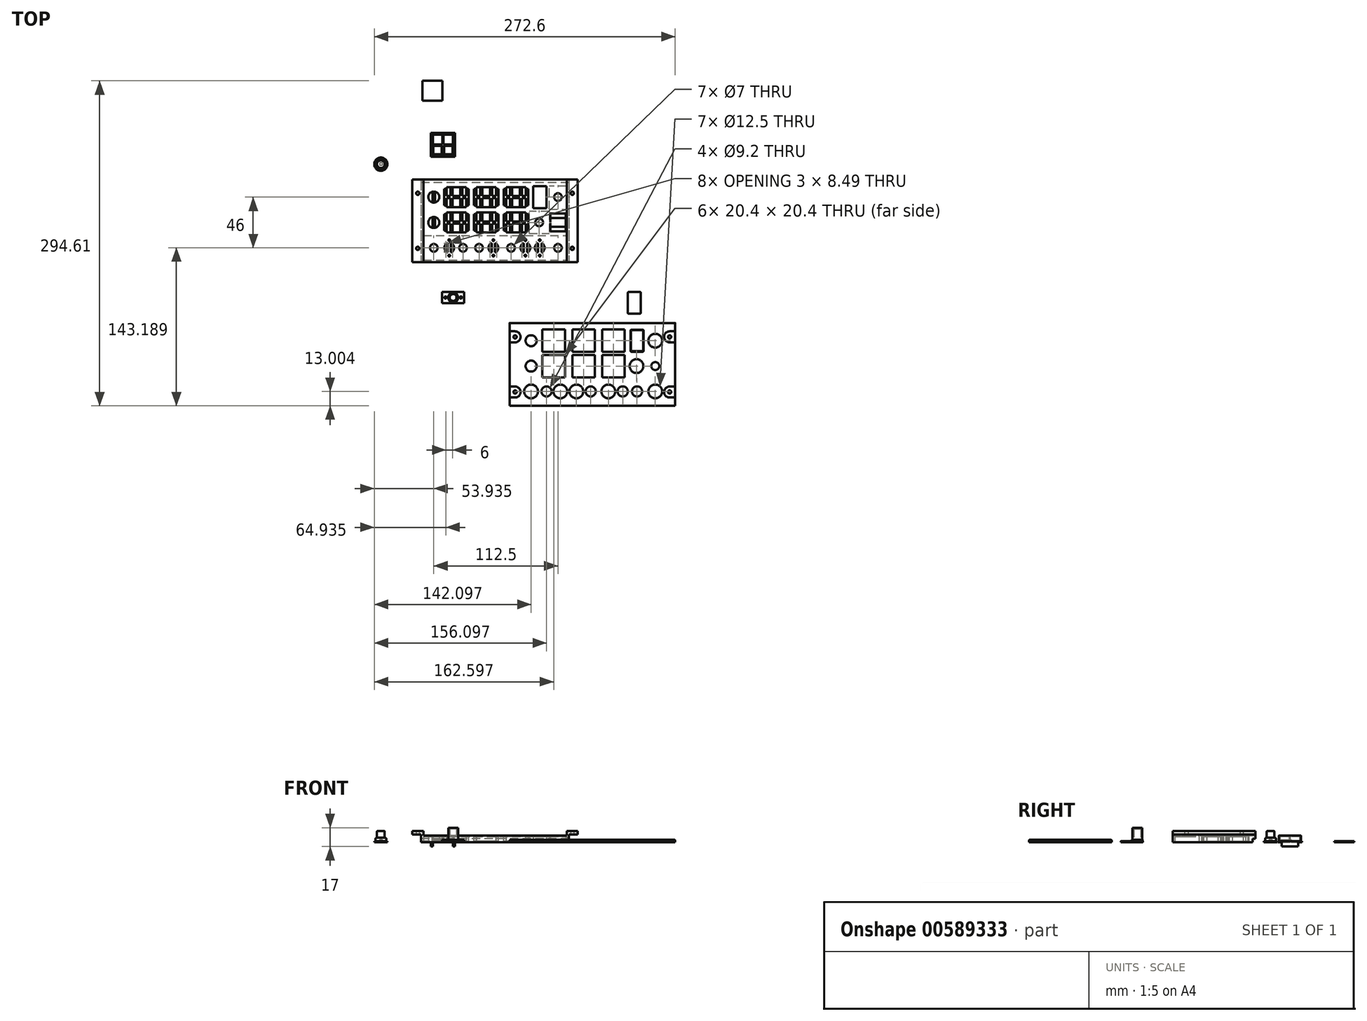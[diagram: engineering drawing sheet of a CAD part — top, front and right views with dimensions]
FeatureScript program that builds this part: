
annotation { "Feature Type Name" : "Feature", "Feature Type Description" : "" }
export const myFeature = defineFeature(function(context is Context, id is Id, definition is map)
    precondition{}
    {
        {
            var Q0;
            Q0=qCreatedBy(makeId("Top.planeOp"),FACE);
            var sketch = newSketch(context, id + "F0", { "sketchPlane" : qUnion([Q0])});
            skLineSegment(sketch, "E0.bottom", {"start": v(0.5, -57.04) * mm, "end": v(-149.5, -57.04) * mm});
            skLineSegment(sketch, "E0.top", {"start": v(0.5, 17.96) * mm, "end": v(-149.5, 17.96) * mm});
            skLineSegment(sketch, "E0.left", {"start": v(0.5, -57.04) * mm, "end": v(0.5, 17.96) * mm});
            skLineSegment(sketch, "E0.right", {"start": v(-149.5, -57.04) * mm, "end": v(-149.5, 17.96) * mm});
            skLineSegment(sketch, "E1.bottom", {"start": v(-99.5, -8.04) * mm, "end": v(-119.5, -8.04) * mm, "construction": true});
            skLineSegment(sketch, "E1.top", {"start": v(-99.5, 11.96) * mm, "end": v(-119.5, 11.96) * mm, "construction": true});
            skLineSegment(sketch, "E1.left", {"start": v(-99.5, -8.04) * mm, "end": v(-99.5, 11.96) * mm, "construction": true});
            skLineSegment(sketch, "E1.right", {"start": v(-119.5, -8.04) * mm, "end": v(-119.5, 11.96) * mm, "construction": true});
            skPoint(sketch, "E1.middle", {"position": v(-109.5, 1.96) * mm});
            skLineSegment(sketch, "E2.bottom", {"start": v(-99.5, -31.04) * mm, "end": v(-119.5, -31.04) * mm, "construction": true});
            skLineSegment(sketch, "E2.top", {"start": v(-99.5, -11.04) * mm, "end": v(-119.5, -11.04) * mm, "construction": true});
            skLineSegment(sketch, "E2.left", {"start": v(-99.5, -31.04) * mm, "end": v(-99.5, -11.04) * mm, "construction": true});
            skLineSegment(sketch, "E2.right", {"start": v(-119.5, -31.04) * mm, "end": v(-119.5, -11.04) * mm, "construction": true});
            skPoint(sketch, "E2.middle", {"position": v(-109.5, -21.04) * mm});
            skCircle(sketch, "E3", {"center": v(-103.5, -44.04) * mm, "radius": 3.5 * mm});
            skCircle(sketch, "E4", {"center": v(-89, -44.04) * mm, "radius": 3.5 * mm});
            skLineSegment(sketch, "E5.bottom", {"start": v(-149.5, 17.96) * mm, "end": v(-141.5, 17.96) * mm, "construction": true});
            skLineSegment(sketch, "E5.top", {"start": v(-149.5, -57.04) * mm, "end": v(-141.5, -57.04) * mm, "construction": true});
            skLineSegment(sketch, "E5.left", {"start": v(-149.5, 17.96) * mm, "end": v(-149.5, -57.04) * mm, "construction": true});
            skLineSegment(sketch, "E5.right", {"start": v(-141.5, 17.96) * mm, "end": v(-141.5, -57.04) * mm, "construction": true});
            skLineSegment(sketch, "E6.bottom", {"start": v(0.5, -57.04) * mm, "end": v(-7.5, -57.04) * mm, "construction": true});
            skLineSegment(sketch, "E6.top", {"start": v(0.5, 17.96) * mm, "end": v(-7.5, 17.96) * mm, "construction": true});
            skLineSegment(sketch, "E6.left", {"start": v(0.5, -57.04) * mm, "end": v(0.5, 17.96) * mm, "construction": true});
            skLineSegment(sketch, "E6.right", {"start": v(-7.5, -57.04) * mm, "end": v(-7.5, 17.96) * mm, "construction": true});
            skCircle(sketch, "E7", {"center": v(-116, -44.04) * mm, "radius": 4.5 * mm});
            skCircle(sketch, "E8", {"center": v(-76, -44.04) * mm, "radius": 4.5 * mm});
            skCircle(sketch, "E9", {"center": v(-60, -44.04) * mm, "radius": 3.5 * mm});
            skCircle(sketch, "E10", {"center": v(-47, -44.04) * mm, "radius": 4.5 * mm});
            skCircle(sketch, "E11", {"center": v(-34, -44.04) * mm, "radius": 4.5 * mm});
            skCircle(sketch, "E12", {"center": v(-17.5, -44.04) * mm, "radius": 3.5 * mm});
            skCircle(sketch, "E13", {"center": v(-34.5, -21.04) * mm, "radius": 3.5 * mm});
            skLineSegment(sketch, "E14.bottom", {"start": v(-28, -8.04) * mm, "end": v(-40, -8.04) * mm});
            skLineSegment(sketch, "E14.top", {"start": v(-28, 11.96) * mm, "end": v(-40, 11.96) * mm});
            skLineSegment(sketch, "E14.left", {"start": v(-28, -8.04) * mm, "end": v(-28, 11.96) * mm});
            skLineSegment(sketch, "E14.right", {"start": v(-40, -8.04) * mm, "end": v(-40, 11.96) * mm});
            skPoint(sketch, "E14.middle", {"position": v(-34, 1.96) * mm});
            skCircle(sketch, "E15", {"center": v(-17.5, 1.96) * mm, "radius": 3.5 * mm});
            skCircle(sketch, "E16", {"center": v(-17.5, -21.04) * mm, "radius": 5 * mm, "construction": true});
            skPoint(sketch, "E17.centerSnap0", {"position": v(-119.5, -21.04) * mm});
            skLineSegment(sketch, "E18.bottom", {"start": v(-100.5, -7.04) * mm, "end": v(-118.5, -7.04) * mm});
            skLineSegment(sketch, "E18.top", {"start": v(-100.5, 10.96) * mm, "end": v(-118.5, 10.96) * mm});
            skLineSegment(sketch, "E18.left", {"start": v(-100.5, -7.04) * mm, "end": v(-100.5, 10.96) * mm});
            skLineSegment(sketch, "E18.right", {"start": v(-118.5, -7.04) * mm, "end": v(-118.5, 10.96) * mm});
            skLineSegment(sketch, "E19.bottom", {"start": v(-100.5, -30.04) * mm, "end": v(-118.5, -30.04) * mm});
            skLineSegment(sketch, "E19.top", {"start": v(-100.5, -12.04) * mm, "end": v(-118.5, -12.04) * mm});
            skLineSegment(sketch, "E19.left", {"start": v(-100.5, -30.04) * mm, "end": v(-100.5, -12.04) * mm});
            skLineSegment(sketch, "E19.right", {"start": v(-118.5, -30.04) * mm, "end": v(-118.5, -12.04) * mm});
            skLineSegment(sketch, "E20.bottom", {"start": v(-100.5, 0.96) * mm, "end": v(-104, 0.96) * mm});
            skLineSegment(sketch, "E20.top", {"start": v(-100.5, 2.96) * mm, "end": v(-104, 2.96) * mm});
            skLineSegment(sketch, "E20.left", {"start": v(-100.5, 0.96) * mm, "end": v(-100.5, 2.96) * mm});
            skLineSegment(sketch, "E20.right", {"start": v(-118.5, 0.96) * mm, "end": v(-118.5, 2.96) * mm});
            skLineSegment(sketch, "E21.bottom", {"start": v(-113, -7.04) * mm, "end": v(-115, -7.04) * mm});
            skLineSegment(sketch, "E21.top", {"start": v(-113, 10.96) * mm, "end": v(-115, 10.96) * mm});
            skLineSegment(sketch, "E21.left", {"start": v(-113, -7.04) * mm, "end": v(-113, 0.96) * mm});
            skLineSegment(sketch, "E21.right", {"start": v(-115, -7.04) * mm, "end": v(-115, 0.96) * mm});
            skPoint(sketch, "E21.middle", {"position": v(-114, 1.96) * mm});
            skLineSegment(sketch, "E22.bottom", {"start": v(-104, -7.04) * mm, "end": v(-106, -7.04) * mm});
            skLineSegment(sketch, "E22.top", {"start": v(-104, 10.96) * mm, "end": v(-106, 10.96) * mm});
            skLineSegment(sketch, "E22.left", {"start": v(-104, -7.04) * mm, "end": v(-104, 0.96) * mm});
            skLineSegment(sketch, "E22.right", {"start": v(-106, -7.04) * mm, "end": v(-106, 0.96) * mm});
            skPoint(sketch, "E22.middle", {"position": v(-105, 1.96) * mm});
            skLineSegment(sketch, "E23.trimOffspring", {"start": v(-115, 2.96) * mm, "end": v(-115, 10.96) * mm});
            skLineSegment(sketch, "E24.trimOffspring", {"start": v(-115, 2.96) * mm, "end": v(-118.5, 2.96) * mm});
            skLineSegment(sketch, "E25.trimOffspring", {"start": v(-113, 2.96) * mm, "end": v(-113, 10.96) * mm});
            skLineSegment(sketch, "E26.trimOffspring", {"start": v(-115, 0.96) * mm, "end": v(-118.5, 0.96) * mm});
            skLineSegment(sketch, "E27.trimOffspring", {"start": v(-106, 2.96) * mm, "end": v(-106, 10.96) * mm});
            skLineSegment(sketch, "E28.trimOffspring", {"start": v(-106, 2.96) * mm, "end": v(-113, 2.96) * mm});
            skLineSegment(sketch, "E29.trimOffspring", {"start": v(-104, 2.96) * mm, "end": v(-104, 10.96) * mm});
            skLineSegment(sketch, "E30.trimOffspring", {"start": v(-106, 0.96) * mm, "end": v(-113, 0.96) * mm});
            skLineSegment(sketch, "E31.bottom", {"start": v(-100.5, -22.04) * mm, "end": v(-104, -22.04) * mm});
            skLineSegment(sketch, "E31.top", {"start": v(-100.5, -20.04) * mm, "end": v(-104, -20.04) * mm});
            skLineSegment(sketch, "E31.left", {"start": v(-100.5, -22.04) * mm, "end": v(-100.5, -20.04) * mm});
            skLineSegment(sketch, "E31.right", {"start": v(-118.5, -22.04) * mm, "end": v(-118.5, -20.04) * mm});
            skLineSegment(sketch, "E32.bottom", {"start": v(-113, -30.04) * mm, "end": v(-115, -30.04) * mm});
            skLineSegment(sketch, "E32.top", {"start": v(-113, -12.04) * mm, "end": v(-115, -12.04) * mm});
            skLineSegment(sketch, "E32.left", {"start": v(-113, -30.04) * mm, "end": v(-113, -22.04) * mm});
            skLineSegment(sketch, "E32.right", {"start": v(-115, -30.04) * mm, "end": v(-115, -22.04) * mm});
            skPoint(sketch, "E32.middle", {"position": v(-114, -21.04) * mm});
            skLineSegment(sketch, "E33.bottom", {"start": v(-104, -30.04) * mm, "end": v(-106, -30.04) * mm});
            skLineSegment(sketch, "E33.top", {"start": v(-104, -12.04) * mm, "end": v(-106, -12.04) * mm});
            skLineSegment(sketch, "E33.left", {"start": v(-104, -30.04) * mm, "end": v(-104, -22.04) * mm});
            skLineSegment(sketch, "E33.right", {"start": v(-106, -30.04) * mm, "end": v(-106, -22.04) * mm});
            skPoint(sketch, "E33.middle", {"position": v(-105, -21.04) * mm});
            skLineSegment(sketch, "E34.trimOffspring", {"start": v(-115, -20.04) * mm, "end": v(-115, -12.04) * mm});
            skLineSegment(sketch, "E35.trimOffspring", {"start": v(-115, -20.04) * mm, "end": v(-118.5, -20.04) * mm});
            skLineSegment(sketch, "E36.trimOffspring", {"start": v(-113, -20.04) * mm, "end": v(-113, -12.04) * mm});
            skLineSegment(sketch, "E37.trimOffspring", {"start": v(-115, -22.04) * mm, "end": v(-118.5, -22.04) * mm});
            skLineSegment(sketch, "E38.trimOffspring", {"start": v(-106, -20.04) * mm, "end": v(-106, -12.04) * mm});
            skLineSegment(sketch, "E39.trimOffspring", {"start": v(-106, -20.04) * mm, "end": v(-113, -20.04) * mm});
            skLineSegment(sketch, "E40.trimOffspring", {"start": v(-104, -20.04) * mm, "end": v(-104, -12.04) * mm});
            skLineSegment(sketch, "E41.trimOffspring", {"start": v(-106, -22.04) * mm, "end": v(-113, -22.04) * mm});
            skPoint(sketch, "E42.middle", {"position": v(-130, 1.96) * mm});
            skPoint(sketch, "E43.middle", {"position": v(-130, -21.04) * mm});
            skLineSegment(sketch, "E44.left", {"start": v(-129, -2.94) * mm, "end": v(-129, 6.86) * mm});
            skLineSegment(sketch, "E44.right", {"start": v(-131, -2.94) * mm, "end": v(-131, 6.86) * mm});
            skLineSegment(sketch, "E45.left", {"start": v(-129, -25.94) * mm, "end": v(-129, -16.14) * mm});
            skLineSegment(sketch, "E45.right", {"start": v(-131, -25.94) * mm, "end": v(-131, -16.14) * mm});
            skCircle(sketch, "E46", {"center": v(-144.5, 5.46) * mm, "radius": 1.5 * mm});
            skPoint(sketch, "E46.centerSnap0", {"position": v(-145.5, 17.96) * mm});
            skCircle(sketch, "E47", {"center": v(-144.5, -44.54) * mm, "radius": 1.5 * mm});
            skCircle(sketch, "E48", {"center": v(-4.5, 5.46) * mm, "radius": 1.5 * mm});
            skCircle(sketch, "E49", {"center": v(-4.5, -44.54) * mm, "radius": 1.5 * mm});
            skLineSegment(sketch, "E50.1.0.0", {"start": v(-73.5, 2.96) * mm, "end": v(-77, 2.96) * mm});
            skLineSegment(sketch, "E50.1.0.1", {"start": v(-79, -30.04) * mm, "end": v(-79, -22.04) * mm});
            skLineSegment(sketch, "E50.1.0.2", {"start": v(-79, -22.04) * mm, "end": v(-86, -22.04) * mm});
            skLineSegment(sketch, "E50.1.0.3", {"start": v(-88, -30.04) * mm, "end": v(-88, -22.04) * mm});
            skLineSegment(sketch, "E50.1.0.4", {"start": v(-72.5, -8.04) * mm, "end": v(-72.5, 11.96) * mm, "construction": true});
            skLineSegment(sketch, "E50.1.0.5", {"start": v(-72.5, -8.04) * mm, "end": v(-92.5, -8.04) * mm, "construction": true});
            skLineSegment(sketch, "E50.1.0.6", {"start": v(-72.5, -31.04) * mm, "end": v(-92.5, -31.04) * mm, "construction": true});
            skLineSegment(sketch, "E50.1.0.7", {"start": v(-73.5, -30.04) * mm, "end": v(-73.5, -12.04) * mm});
            skLineSegment(sketch, "E50.1.0.8", {"start": v(-73.5, -7.04) * mm, "end": v(-91.5, -7.04) * mm});
            skLineSegment(sketch, "E50.1.0.9", {"start": v(-79, 2.96) * mm, "end": v(-86, 2.96) * mm});
            skLineSegment(sketch, "E50.1.0.10", {"start": v(-79, -20.04) * mm, "end": v(-86, -20.04) * mm});
            skLineSegment(sketch, "E50.1.0.11", {"start": v(-88, 2.96) * mm, "end": v(-91.5, 2.96) * mm});
            skLineSegment(sketch, "E50.1.0.12", {"start": v(-77, -30.04) * mm, "end": v(-77, -22.04) * mm});
            skLineSegment(sketch, "E50.1.0.13", {"start": v(-86, 2.96) * mm, "end": v(-86, 10.96) * mm});
            skLineSegment(sketch, "E50.1.0.14", {"start": v(-77, -20.04) * mm, "end": v(-77, -12.04) * mm});
            skLineSegment(sketch, "E50.1.0.15", {"start": v(-88, -20.04) * mm, "end": v(-88, -12.04) * mm});
            skLineSegment(sketch, "E50.1.0.16", {"start": v(-79, 2.96) * mm, "end": v(-79, 10.96) * mm});
            skPoint(sketch, "E50.1.0.17", {"position": v(-82.5, -21.04) * mm});
            skLineSegment(sketch, "E50.1.0.18", {"start": v(-73.5, -22.04) * mm, "end": v(-77, -22.04) * mm});
            skLineSegment(sketch, "E50.1.0.19", {"start": v(-88, 0.96) * mm, "end": v(-91.5, 0.96) * mm});
            skLineSegment(sketch, "E50.1.0.20", {"start": v(-72.5, 11.96) * mm, "end": v(-92.5, 11.96) * mm, "construction": true});
            skLineSegment(sketch, "E50.1.0.21", {"start": v(-88, -22.04) * mm, "end": v(-91.5, -22.04) * mm});
            skLineSegment(sketch, "E50.1.0.22", {"start": v(-91.5, -7.04) * mm, "end": v(-91.5, 10.96) * mm});
            skLineSegment(sketch, "E50.1.0.23", {"start": v(-72.5, -11.04) * mm, "end": v(-92.5, -11.04) * mm, "construction": true});
            skLineSegment(sketch, "E50.1.0.24", {"start": v(-92.5, -31.04) * mm, "end": v(-92.5, -11.04) * mm, "construction": true});
            skLineSegment(sketch, "E50.1.0.25", {"start": v(-79, -20.04) * mm, "end": v(-79, -12.04) * mm});
            skLineSegment(sketch, "E50.1.0.26", {"start": v(-92.5, -8.04) * mm, "end": v(-92.5, 11.96) * mm, "construction": true});
            skLineSegment(sketch, "E50.1.0.27", {"start": v(-88, 2.96) * mm, "end": v(-88, 10.96) * mm});
            skLineSegment(sketch, "E50.1.0.28", {"start": v(-72.5, -31.04) * mm, "end": v(-72.5, -11.04) * mm, "construction": true});
            skLineSegment(sketch, "E50.1.0.29", {"start": v(-73.5, -7.04) * mm, "end": v(-73.5, 10.96) * mm});
            skLineSegment(sketch, "E50.1.0.30", {"start": v(-73.5, -30.04) * mm, "end": v(-91.5, -30.04) * mm});
            skLineSegment(sketch, "E50.1.0.31", {"start": v(-77, -7.04) * mm, "end": v(-77, 0.96) * mm});
            skLineSegment(sketch, "E50.1.0.32", {"start": v(-79, -7.04) * mm, "end": v(-79, 0.96) * mm});
            skLineSegment(sketch, "E50.1.0.33", {"start": v(-86, -20.04) * mm, "end": v(-86, -12.04) * mm});
            skLineSegment(sketch, "E50.1.0.34", {"start": v(-73.5, 0.96) * mm, "end": v(-77, 0.96) * mm});
            skLineSegment(sketch, "E50.1.0.35", {"start": v(-73.5, -12.04) * mm, "end": v(-91.5, -12.04) * mm});
            skLineSegment(sketch, "E50.1.0.36", {"start": v(-86, -30.04) * mm, "end": v(-86, -22.04) * mm});
            skLineSegment(sketch, "E50.1.0.37", {"start": v(-77, 2.96) * mm, "end": v(-77, 10.96) * mm});
            skLineSegment(sketch, "E50.1.0.38", {"start": v(-88, -7.04) * mm, "end": v(-88, 0.96) * mm});
            skLineSegment(sketch, "E50.1.0.39", {"start": v(-91.5, -30.04) * mm, "end": v(-91.5, -12.04) * mm});
            skLineSegment(sketch, "E50.1.0.40", {"start": v(-73.5, 10.96) * mm, "end": v(-91.5, 10.96) * mm});
            skLineSegment(sketch, "E50.1.0.41", {"start": v(-73.5, -20.04) * mm, "end": v(-77, -20.04) * mm});
            skPoint(sketch, "E50.1.0.42", {"position": v(-82.5, 1.96) * mm});
            skPoint(sketch, "E50.1.0.43", {"position": v(-92.5, -21.04) * mm});
            skLineSegment(sketch, "E50.1.0.44", {"start": v(-79, 0.96) * mm, "end": v(-86, 0.96) * mm});
            skLineSegment(sketch, "E50.1.0.45", {"start": v(-86, -7.04) * mm, "end": v(-86, 0.96) * mm});
            skLineSegment(sketch, "E50.1.0.46", {"start": v(-73.5, -12.04) * mm, "end": v(-91.5, -12.04) * mm});
            skLineSegment(sketch, "E50.1.0.47", {"start": v(-73.5, -30.04) * mm, "end": v(-73.5, -12.04) * mm});
            skLineSegment(sketch, "E50.1.0.48", {"start": v(-73.5, -30.04) * mm, "end": v(-91.5, -30.04) * mm});
            skPoint(sketch, "E50.1.0.49", {"position": v(-82.5, -21.04) * mm});
            skPoint(sketch, "E50.1.0.50", {"position": v(-82.5, 1.96) * mm});
            skLineSegment(sketch, "E50.1.0.51", {"start": v(-88, -20.04) * mm, "end": v(-91.5, -20.04) * mm});
            skLineSegment(sketch, "E50.1.0.52", {"start": v(-91.5, -30.04) * mm, "end": v(-91.5, -12.04) * mm});
            skPoint(sketch, "E50.1.0.53", {"position": v(-87, 1.96) * mm});
            skLineSegment(sketch, "E50.1.0.54", {"start": v(-91.5, -22.04) * mm, "end": v(-91.5, -20.04) * mm});
            skLineSegment(sketch, "E50.1.0.55", {"start": v(-86, -12.04) * mm, "end": v(-88, -12.04) * mm});
            skLineSegment(sketch, "E50.1.0.56", {"start": v(-91.5, 0.96) * mm, "end": v(-91.5, 2.96) * mm});
            skLineSegment(sketch, "E50.1.0.57", {"start": v(-86, 10.96) * mm, "end": v(-88, 10.96) * mm});
            skLineSegment(sketch, "E50.1.0.58", {"start": v(-86, -30.04) * mm, "end": v(-88, -30.04) * mm});
            skLineSegment(sketch, "E50.1.0.59", {"start": v(-73.5, -22.04) * mm, "end": v(-73.5, -20.04) * mm});
            skPoint(sketch, "E50.1.0.60", {"position": v(-78, -21.04) * mm});
            skLineSegment(sketch, "E50.1.0.61", {"start": v(-77, -7.04) * mm, "end": v(-79, -7.04) * mm});
            skPoint(sketch, "E50.1.0.62", {"position": v(-87, -21.04) * mm});
            skPoint(sketch, "E50.1.0.63", {"position": v(-82.5, -21.04) * mm});
            skLineSegment(sketch, "E50.1.0.64", {"start": v(-77, -30.04) * mm, "end": v(-79, -30.04) * mm});
            skLineSegment(sketch, "E50.1.0.65", {"start": v(-73.5, 0.96) * mm, "end": v(-73.5, 2.96) * mm});
            skPoint(sketch, "E50.1.0.66", {"position": v(-82.5, 1.96) * mm});
            skLineSegment(sketch, "E50.1.0.67", {"start": v(-86, -7.04) * mm, "end": v(-88, -7.04) * mm});
            skLineSegment(sketch, "E50.1.0.68", {"start": v(-77, 10.96) * mm, "end": v(-79, 10.96) * mm});
            skPoint(sketch, "E50.1.0.69", {"position": v(-78, 1.96) * mm});
            skLineSegment(sketch, "E50.1.0.70", {"start": v(-77, -12.04) * mm, "end": v(-79, -12.04) * mm});
            skPoint(sketch, "E50.1.0.71", {"position": v(-82.5, -21.04) * mm});
            skPoint(sketch, "E50.1.0.72", {"position": v(-82.5, -21.04) * mm});
            skLineSegment(sketch, "E50.2.0.0", {"start": v(-46.5, 2.96) * mm, "end": v(-50, 2.96) * mm});
            skLineSegment(sketch, "E50.2.0.1", {"start": v(-52, -30.04) * mm, "end": v(-52, -22.04) * mm});
            skLineSegment(sketch, "E50.2.0.2", {"start": v(-52, -22.04) * mm, "end": v(-59, -22.04) * mm});
            skLineSegment(sketch, "E50.2.0.3", {"start": v(-61, -30.04) * mm, "end": v(-61, -22.04) * mm});
            skLineSegment(sketch, "E50.2.0.4", {"start": v(-45.5, -8.04) * mm, "end": v(-45.5, 11.96) * mm, "construction": true});
            skLineSegment(sketch, "E50.2.0.5", {"start": v(-45.5, -8.04) * mm, "end": v(-65.5, -8.04) * mm, "construction": true});
            skLineSegment(sketch, "E50.2.0.6", {"start": v(-45.5, -31.04) * mm, "end": v(-65.5, -31.04) * mm, "construction": true});
            skLineSegment(sketch, "E50.2.0.7", {"start": v(-46.5, -30.04) * mm, "end": v(-46.5, -12.04) * mm});
            skLineSegment(sketch, "E50.2.0.8", {"start": v(-46.5, -7.04) * mm, "end": v(-64.5, -7.04) * mm});
            skLineSegment(sketch, "E50.2.0.9", {"start": v(-52, 2.96) * mm, "end": v(-59, 2.96) * mm});
            skLineSegment(sketch, "E50.2.0.10", {"start": v(-52, -20.04) * mm, "end": v(-59, -20.04) * mm});
            skLineSegment(sketch, "E50.2.0.11", {"start": v(-61, 2.96) * mm, "end": v(-64.5, 2.96) * mm});
            skLineSegment(sketch, "E50.2.0.12", {"start": v(-50, -30.04) * mm, "end": v(-50, -22.04) * mm});
            skLineSegment(sketch, "E50.2.0.13", {"start": v(-59, 2.96) * mm, "end": v(-59, 10.96) * mm});
            skLineSegment(sketch, "E50.2.0.14", {"start": v(-50, -20.04) * mm, "end": v(-50, -12.04) * mm});
            skLineSegment(sketch, "E50.2.0.15", {"start": v(-61, -20.04) * mm, "end": v(-61, -12.04) * mm});
            skLineSegment(sketch, "E50.2.0.16", {"start": v(-52, 2.96) * mm, "end": v(-52, 10.96) * mm});
            skPoint(sketch, "E50.2.0.17", {"position": v(-55.5, -21.04) * mm});
            skLineSegment(sketch, "E50.2.0.18", {"start": v(-46.5, -22.04) * mm, "end": v(-50, -22.04) * mm});
            skLineSegment(sketch, "E50.2.0.19", {"start": v(-61, 0.96) * mm, "end": v(-64.5, 0.96) * mm});
            skLineSegment(sketch, "E50.2.0.20", {"start": v(-45.5, 11.96) * mm, "end": v(-65.5, 11.96) * mm, "construction": true});
            skLineSegment(sketch, "E50.2.0.21", {"start": v(-61, -22.04) * mm, "end": v(-64.5, -22.04) * mm});
            skLineSegment(sketch, "E50.2.0.22", {"start": v(-64.5, -7.04) * mm, "end": v(-64.5, 10.96) * mm});
            skLineSegment(sketch, "E50.2.0.23", {"start": v(-45.5, -11.04) * mm, "end": v(-65.5, -11.04) * mm, "construction": true});
            skLineSegment(sketch, "E50.2.0.24", {"start": v(-65.5, -31.04) * mm, "end": v(-65.5, -11.04) * mm, "construction": true});
            skLineSegment(sketch, "E50.2.0.25", {"start": v(-52, -20.04) * mm, "end": v(-52, -12.04) * mm});
            skLineSegment(sketch, "E50.2.0.26", {"start": v(-65.5, -8.04) * mm, "end": v(-65.5, 11.96) * mm, "construction": true});
            skLineSegment(sketch, "E50.2.0.27", {"start": v(-61, 2.96) * mm, "end": v(-61, 10.96) * mm});
            skLineSegment(sketch, "E50.2.0.28", {"start": v(-45.5, -31.04) * mm, "end": v(-45.5, -11.04) * mm, "construction": true});
            skLineSegment(sketch, "E50.2.0.29", {"start": v(-46.5, -7.04) * mm, "end": v(-46.5, 10.96) * mm});
            skLineSegment(sketch, "E50.2.0.30", {"start": v(-46.5, -30.04) * mm, "end": v(-64.5, -30.04) * mm});
            skLineSegment(sketch, "E50.2.0.31", {"start": v(-50, -7.04) * mm, "end": v(-50, 0.96) * mm});
            skLineSegment(sketch, "E50.2.0.32", {"start": v(-52, -7.04) * mm, "end": v(-52, 0.96) * mm});
            skLineSegment(sketch, "E50.2.0.33", {"start": v(-59, -20.04) * mm, "end": v(-59, -12.04) * mm});
            skLineSegment(sketch, "E50.2.0.34", {"start": v(-46.5, 0.96) * mm, "end": v(-50, 0.96) * mm});
            skLineSegment(sketch, "E50.2.0.35", {"start": v(-46.5, -12.04) * mm, "end": v(-64.5, -12.04) * mm});
            skLineSegment(sketch, "E50.2.0.36", {"start": v(-59, -30.04) * mm, "end": v(-59, -22.04) * mm});
            skLineSegment(sketch, "E50.2.0.37", {"start": v(-50, 2.96) * mm, "end": v(-50, 10.96) * mm});
            skLineSegment(sketch, "E50.2.0.38", {"start": v(-61, -7.04) * mm, "end": v(-61, 0.96) * mm});
            skLineSegment(sketch, "E50.2.0.39", {"start": v(-64.5, -30.04) * mm, "end": v(-64.5, -12.04) * mm});
            skLineSegment(sketch, "E50.2.0.40", {"start": v(-46.5, 10.96) * mm, "end": v(-64.5, 10.96) * mm});
            skLineSegment(sketch, "E50.2.0.41", {"start": v(-46.5, -20.04) * mm, "end": v(-50, -20.04) * mm});
            skPoint(sketch, "E50.2.0.42", {"position": v(-55.5, 1.96) * mm});
            skPoint(sketch, "E50.2.0.43", {"position": v(-65.5, -21.04) * mm});
            skLineSegment(sketch, "E50.2.0.44", {"start": v(-52, 0.96) * mm, "end": v(-59, 0.96) * mm});
            skLineSegment(sketch, "E50.2.0.45", {"start": v(-59, -7.04) * mm, "end": v(-59, 0.96) * mm});
            skLineSegment(sketch, "E50.2.0.46", {"start": v(-46.5, -12.04) * mm, "end": v(-64.5, -12.04) * mm});
            skLineSegment(sketch, "E50.2.0.47", {"start": v(-46.5, -30.04) * mm, "end": v(-46.5, -12.04) * mm});
            skLineSegment(sketch, "E50.2.0.48", {"start": v(-46.5, -30.04) * mm, "end": v(-64.5, -30.04) * mm});
            skPoint(sketch, "E50.2.0.49", {"position": v(-55.5, -21.04) * mm});
            skPoint(sketch, "E50.2.0.50", {"position": v(-55.5, 1.96) * mm});
            skLineSegment(sketch, "E50.2.0.51", {"start": v(-61, -20.04) * mm, "end": v(-64.5, -20.04) * mm});
            skLineSegment(sketch, "E50.2.0.52", {"start": v(-64.5, -30.04) * mm, "end": v(-64.5, -12.04) * mm});
            skPoint(sketch, "E50.2.0.53", {"position": v(-60, 1.96) * mm});
            skLineSegment(sketch, "E50.2.0.54", {"start": v(-64.5, -22.04) * mm, "end": v(-64.5, -20.04) * mm});
            skLineSegment(sketch, "E50.2.0.55", {"start": v(-59, -12.04) * mm, "end": v(-61, -12.04) * mm});
            skLineSegment(sketch, "E50.2.0.56", {"start": v(-64.5, 0.96) * mm, "end": v(-64.5, 2.96) * mm});
            skLineSegment(sketch, "E50.2.0.57", {"start": v(-59, 10.96) * mm, "end": v(-61, 10.96) * mm});
            skLineSegment(sketch, "E50.2.0.58", {"start": v(-59, -30.04) * mm, "end": v(-61, -30.04) * mm});
            skLineSegment(sketch, "E50.2.0.59", {"start": v(-46.5, -22.04) * mm, "end": v(-46.5, -20.04) * mm});
            skPoint(sketch, "E50.2.0.60", {"position": v(-51, -21.04) * mm});
            skLineSegment(sketch, "E50.2.0.61", {"start": v(-50, -7.04) * mm, "end": v(-52, -7.04) * mm});
            skPoint(sketch, "E50.2.0.62", {"position": v(-60, -21.04) * mm});
            skPoint(sketch, "E50.2.0.63", {"position": v(-55.5, -21.04) * mm});
            skLineSegment(sketch, "E50.2.0.64", {"start": v(-50, -30.04) * mm, "end": v(-52, -30.04) * mm});
            skLineSegment(sketch, "E50.2.0.65", {"start": v(-46.5, 0.96) * mm, "end": v(-46.5, 2.96) * mm});
            skPoint(sketch, "E50.2.0.66", {"position": v(-55.5, 1.96) * mm});
            skLineSegment(sketch, "E50.2.0.67", {"start": v(-59, -7.04) * mm, "end": v(-61, -7.04) * mm});
            skLineSegment(sketch, "E50.2.0.68", {"start": v(-50, 10.96) * mm, "end": v(-52, 10.96) * mm});
            skPoint(sketch, "E50.2.0.69", {"position": v(-51, 1.96) * mm});
            skLineSegment(sketch, "E50.2.0.70", {"start": v(-50, -12.04) * mm, "end": v(-52, -12.04) * mm});
            skPoint(sketch, "E50.2.0.71", {"position": v(-55.5, -21.04) * mm});
            skPoint(sketch, "E50.2.0.72", {"position": v(-55.5, -21.04) * mm});
            skLineSegment(sketch, "E50.direction1", {"start": v(-119.5, -31.04) * mm, "end": v(-92.5, -31.04) * mm, "construction": true});
            skCircle(sketch, "E51", {"center": v(-130, 1.96) * mm, "radius": 5 * mm});
            skCircle(sketch, "E52", {"center": v(-130, -21.04) * mm, "radius": 5 * mm});
            skLineSegment(sketch, "E53.bottom", {"start": v(-32.5, -8.04) * mm, "end": v(-35.5, -8.04) * mm});
            skLineSegment(sketch, "E53.top", {"start": v(-32.5, 11.96) * mm, "end": v(-35.5, 11.96) * mm});
            skLineSegment(sketch, "E53.left", {"start": v(-32.5, -8.04) * mm, "end": v(-32.5, 11.96) * mm});
            skLineSegment(sketch, "E53.right", {"start": v(-35.5, -8.04) * mm, "end": v(-35.5, 11.96) * mm});
            skLineSegment(sketch, "E54.bottom", {"start": v(-10.5, -29.04) * mm, "end": v(-24.5, -29.04) * mm});
            skLineSegment(sketch, "E54.top", {"start": v(-10.5, -13.04) * mm, "end": v(-24.5, -13.04) * mm});
            skLineSegment(sketch, "E54.left", {"start": v(-10.5, -29.04) * mm, "end": v(-10.5, -13.04) * mm});
            skLineSegment(sketch, "E54.right", {"start": v(-24.5, -29.04) * mm, "end": v(-24.5, -13.04) * mm});
            skLineSegment(sketch, "E55.bottom", {"start": v(-10.5, -25.04) * mm, "end": v(-24.5, -25.04) * mm});
            skLineSegment(sketch, "E55.top", {"start": v(-10.5, -17.04) * mm, "end": v(-24.5, -17.04) * mm});
            skLineSegment(sketch, "E55.left", {"start": v(-10.5, -25.04) * mm, "end": v(-10.5, -17.04) * mm});
            skLineSegment(sketch, "E55.right", {"start": v(-24.5, -25.04) * mm, "end": v(-24.5, -17.04) * mm});
            skLineSegment(sketch, "E56.bottom", {"start": v(-27.5, -28.04) * mm, "end": v(-41.5, -28.04) * mm, "construction": true});
            skLineSegment(sketch, "E56.top", {"start": v(-27.5, -14.04) * mm, "end": v(-41.5, -14.04) * mm, "construction": true});
            skLineSegment(sketch, "E56.left", {"start": v(-27.5, -28.04) * mm, "end": v(-27.5, -14.04) * mm, "construction": true});
            skLineSegment(sketch, "E56.right", {"start": v(-41.5, -28.04) * mm, "end": v(-41.5, -14.04) * mm, "construction": true});
            skCircle(sketch, "E57", {"center": v(-34.5, -21.04) * mm, "radius": 6.25 * mm, "construction": true});
            skLineSegment(sketch, "E58.bottom", {"start": v(-10.5, 8.96) * mm, "end": v(-24.5, 8.96) * mm, "construction": true});
            skLineSegment(sketch, "E58.top", {"start": v(-10.5, -5.04) * mm, "end": v(-24.5, -5.04) * mm, "construction": true});
            skLineSegment(sketch, "E58.left", {"start": v(-10.5, 8.96) * mm, "end": v(-10.5, -5.04) * mm, "construction": true});
            skLineSegment(sketch, "E58.right", {"start": v(-24.5, 8.96) * mm, "end": v(-24.5, -5.04) * mm, "construction": true});
            skLineSegment(sketch, "E59.bottom", {"start": v(-111, -54.04) * mm, "end": v(-121, -54.04) * mm, "construction": true});
            skLineSegment(sketch, "E59.top", {"start": v(-111, -34.04) * mm, "end": v(-121, -34.04) * mm, "construction": true});
            skLineSegment(sketch, "E59.left", {"start": v(-111, -54.04) * mm, "end": v(-111, -34.04) * mm, "construction": true});
            skLineSegment(sketch, "E59.right", {"start": v(-121, -54.04) * mm, "end": v(-121, -34.04) * mm, "construction": true});
            skCircle(sketch, "E60", {"center": v(-116, -37.04) * mm, "radius": 0.8 * mm});
            skCircle(sketch, "E61", {"center": v(-116, -51.04) * mm, "radius": 0.8 * mm});
            skLineSegment(sketch, "E62.bottom", {"start": v(-71, -54.04) * mm, "end": v(-81, -54.04) * mm, "construction": true});
            skLineSegment(sketch, "E62.top", {"start": v(-71, -34.04) * mm, "end": v(-81, -34.04) * mm, "construction": true});
            skLineSegment(sketch, "E62.left", {"start": v(-71, -54.04) * mm, "end": v(-71, -34.04) * mm, "construction": true});
            skLineSegment(sketch, "E62.right", {"start": v(-81, -54.04) * mm, "end": v(-81, -34.04) * mm, "construction": true});
            skCircle(sketch, "E63", {"center": v(-76, -37.04) * mm, "radius": 0.8 * mm});
            skCircle(sketch, "E64", {"center": v(-76, -51.04) * mm, "radius": 0.8 * mm});
            skLineSegment(sketch, "E65.bottom", {"start": v(-42, -54.04) * mm, "end": v(-52, -54.04) * mm, "construction": true});
            skLineSegment(sketch, "E65.top", {"start": v(-42, -34.04) * mm, "end": v(-52, -34.04) * mm, "construction": true});
            skLineSegment(sketch, "E65.left", {"start": v(-42, -54.04) * mm, "end": v(-42, -34.04) * mm, "construction": true});
            skLineSegment(sketch, "E65.right", {"start": v(-52, -54.04) * mm, "end": v(-52, -34.04) * mm, "construction": true});
            skCircle(sketch, "E66", {"center": v(-47, -37.04) * mm, "radius": 0.8 * mm});
            skCircle(sketch, "E67", {"center": v(-47, -51.04) * mm, "radius": 0.8 * mm});
            skLineSegment(sketch, "E68.bottom", {"start": v(-29, -54.04) * mm, "end": v(-39, -54.04) * mm, "construction": true});
            skLineSegment(sketch, "E68.top", {"start": v(-29, -34.04) * mm, "end": v(-39, -34.04) * mm, "construction": true});
            skLineSegment(sketch, "E68.left", {"start": v(-29, -54.04) * mm, "end": v(-29, -34.04) * mm, "construction": true});
            skLineSegment(sketch, "E68.right", {"start": v(-39, -54.04) * mm, "end": v(-39, -34.04) * mm, "construction": true});
            skCircle(sketch, "E69", {"center": v(-34, -37.04) * mm, "radius": 0.8 * mm});
            skCircle(sketch, "E70", {"center": v(-34, -51.04) * mm, "radius": 0.8 * mm});
            skCircle(sketch, "E71", {"center": v(-130, -44.04) * mm, "radius": 3.5 * mm});
            skLineSegment(sketch, "E72.bottom", {"start": v(-126.5, -50.54) * mm, "end": v(-133.5, -50.54) * mm, "construction": true});
            skLineSegment(sketch, "E72.top", {"start": v(-126.5, -37.54) * mm, "end": v(-133.5, -37.54) * mm, "construction": true});
            skLineSegment(sketch, "E72.left", {"start": v(-126.5, -50.54) * mm, "end": v(-126.5, -37.54) * mm, "construction": true});
            skLineSegment(sketch, "E72.right", {"start": v(-133.5, -50.54) * mm, "end": v(-133.5, -37.54) * mm, "construction": true});
            skSolve(sketch);
        }
        {
            var Q0;
            Q0=qCreatedBy(makeId("Top.planeOp"),FACE);
            var sketch = newSketch(context, id + "F1", { "sketchPlane" : qUnion([Q0])});
            skLineSegment(sketch, "E73.bottom", {"start": v(88.66, -187.23) * mm, "end": v(-61.34, -187.23) * mm});
            skLineSegment(sketch, "E73.top", {"start": v(88.66, -112.23) * mm, "end": v(-61.34, -112.23) * mm});
            skLineSegment(sketch, "E73.left", {"start": v(88.66, -187.23) * mm, "end": v(88.66, -112.23) * mm});
            skLineSegment(sketch, "E73.right", {"start": v(-61.34, -187.23) * mm, "end": v(-61.34, -112.23) * mm});
            skLineSegment(sketch, "E74.bottom", {"start": v(-11.14, -138.43) * mm, "end": v(-31.54, -138.43) * mm});
            skLineSegment(sketch, "E74.top", {"start": v(-11.14, -118.03) * mm, "end": v(-31.54, -118.03) * mm});
            skLineSegment(sketch, "E74.left", {"start": v(-11.14, -138.43) * mm, "end": v(-11.14, -118.03) * mm});
            skLineSegment(sketch, "E74.right", {"start": v(-31.54, -138.43) * mm, "end": v(-31.54, -118.03) * mm});
            skLineSegment(sketch, "E75.bottom", {"start": v(-11.14, -161.43) * mm, "end": v(-31.54, -161.43) * mm});
            skLineSegment(sketch, "E75.top", {"start": v(-11.14, -141.03) * mm, "end": v(-31.54, -141.03) * mm});
            skLineSegment(sketch, "E75.left", {"start": v(-11.14, -161.43) * mm, "end": v(-11.14, -141.03) * mm});
            skLineSegment(sketch, "E75.right", {"start": v(-31.54, -161.43) * mm, "end": v(-31.54, -141.03) * mm});
            skCircle(sketch, "E76", {"center": v(-15.34, -174.23) * mm, "radius": 3.5 * mm, "construction": true});
            skCircle(sketch, "E77", {"center": v(-0.84, -174.23) * mm, "radius": 3.5 * mm, "construction": true});
            skLineSegment(sketch, "E78.bottom", {"start": v(-61.34, -112.23) * mm, "end": v(-53.34, -112.23) * mm, "construction": true});
            skLineSegment(sketch, "E78.top", {"start": v(-61.34, -187.23) * mm, "end": v(-53.34, -187.23) * mm, "construction": true});
            skLineSegment(sketch, "E78.left", {"start": v(-61.34, -112.23) * mm, "end": v(-61.34, -187.23) * mm, "construction": true});
            skLineSegment(sketch, "E78.right", {"start": v(-53.34, -112.23) * mm, "end": v(-53.34, -187.23) * mm, "construction": true});
            skLineSegment(sketch, "E79.bottom", {"start": v(88.66, -187.23) * mm, "end": v(80.66, -187.23) * mm, "construction": true});
            skLineSegment(sketch, "E79.top", {"start": v(88.66, -112.23) * mm, "end": v(80.66, -112.23) * mm, "construction": true});
            skLineSegment(sketch, "E79.left", {"start": v(88.66, -187.23) * mm, "end": v(88.66, -112.23) * mm, "construction": true});
            skLineSegment(sketch, "E79.right", {"start": v(80.66, -187.23) * mm, "end": v(80.66, -112.23) * mm, "construction": true});
            skCircle(sketch, "E80", {"center": v(-27.84, -174.23) * mm, "radius": 4.6 * mm});
            skCircle(sketch, "E81", {"center": v(12.16, -174.23) * mm, "radius": 4.6 * mm});
            skCircle(sketch, "E82", {"center": v(28.16, -174.23) * mm, "radius": 3.5 * mm, "construction": true});
            skCircle(sketch, "E83", {"center": v(41.16, -174.23) * mm, "radius": 4.6 * mm});
            skCircle(sketch, "E84", {"center": v(54.16, -174.23) * mm, "radius": 4.6 * mm});
            skCircle(sketch, "E85", {"center": v(70.66, -174.23) * mm, "radius": 3.5 * mm, "construction": true});
            skCircle(sketch, "E86", {"center": v(53.66, -151.23) * mm, "radius": 3.5 * mm, "construction": true});
            skLineSegment(sketch, "E87.bottom", {"start": v(60.16, -138.23) * mm, "end": v(48.16, -138.23) * mm});
            skLineSegment(sketch, "E87.top", {"start": v(60.16, -118.23) * mm, "end": v(48.16, -118.23) * mm});
            skLineSegment(sketch, "E87.left", {"start": v(60.16, -138.23) * mm, "end": v(60.16, -118.23) * mm});
            skLineSegment(sketch, "E87.right", {"start": v(48.16, -138.23) * mm, "end": v(48.16, -118.23) * mm});
            skPoint(sketch, "E87.middle", {"position": v(54.16, -128.23) * mm});
            skCircle(sketch, "E88", {"center": v(70.66, -128.23) * mm, "radius": 3.5 * mm, "construction": true});
            skCircle(sketch, "E89", {"center": v(70.66, -151.23) * mm, "radius": 3.6 * mm});
            skLineSegment(sketch, "E90.bottom", {"start": v(-36.84, -133.23) * mm, "end": v(-46.84, -133.23) * mm, "construction": true});
            skLineSegment(sketch, "E90.top", {"start": v(-36.84, -123.23) * mm, "end": v(-46.84, -123.23) * mm, "construction": true});
            skLineSegment(sketch, "E90.left", {"start": v(-36.84, -133.23) * mm, "end": v(-36.84, -123.23) * mm, "construction": true});
            skLineSegment(sketch, "E90.right", {"start": v(-46.84, -133.23) * mm, "end": v(-46.84, -123.23) * mm, "construction": true});
            skPoint(sketch, "E90.middle", {"position": v(-41.84, -128.23) * mm});
            skLineSegment(sketch, "E91.bottom", {"start": v(-40.84, -133.23) * mm, "end": v(-42.84, -133.23) * mm});
            skLineSegment(sketch, "E91.top", {"start": v(-40.84, -123.23) * mm, "end": v(-42.84, -123.23) * mm});
            skLineSegment(sketch, "E91.left", {"start": v(-40.84, -133.23) * mm, "end": v(-40.84, -123.23) * mm});
            skLineSegment(sketch, "E91.right", {"start": v(-42.84, -133.23) * mm, "end": v(-42.84, -123.23) * mm});
            skCircle(sketch, "E92", {"center": v(-56.34, -124.73) * mm, "radius": 1.5 * mm});
            skPoint(sketch, "E92.centerSnap0", {"position": v(-57.34, -112.23) * mm});
            skCircle(sketch, "E93", {"center": v(-41.84, -128.23) * mm, "radius": 5 * mm});
            skCircle(sketch, "E94", {"center": v(-15.34, -174.23) * mm, "radius": 6.25 * mm});
            skCircle(sketch, "E95", {"center": v(-0.84, -174.23) * mm, "radius": 6.25 * mm});
            skCircle(sketch, "E96", {"center": v(28.16, -174.23) * mm, "radius": 6.25 * mm});
            skCircle(sketch, "E97", {"center": v(70.66, -174.23) * mm, "radius": 6.25 * mm});
            skCircle(sketch, "E98", {"center": v(53.66, -151.23) * mm, "radius": 6.25 * mm});
            skCircle(sketch, "E99", {"center": v(70.66, -128.23) * mm, "radius": 6.25 * mm});
            skCircle(sketch, "E100", {"center": v(-56.34, -174.73) * mm, "radius": 1.5 * mm});
            skCircle(sketch, "E101", {"center": v(83.66, -124.73) * mm, "radius": 1.5 * mm});
            skCircle(sketch, "E102", {"center": v(83.66, -174.73) * mm, "radius": 1.5 * mm});
            skLineSegment(sketch, "E103.bottom", {"start": v(-53.34, -112.23) * mm, "end": v(-51.34, -112.23) * mm, "construction": true});
            skLineSegment(sketch, "E103.top", {"start": v(-53.34, -187.23) * mm, "end": v(-51.34, -187.23) * mm, "construction": true});
            skLineSegment(sketch, "E103.right", {"start": v(-51.34, -112.23) * mm, "end": v(-51.34, -187.23) * mm, "construction": true});
            skLineSegment(sketch, "E104.bottom", {"start": v(80.66, -112.23) * mm, "end": v(78.66, -112.23) * mm, "construction": true});
            skLineSegment(sketch, "E104.top", {"start": v(80.66, -187.23) * mm, "end": v(78.66, -187.23) * mm, "construction": true});
            skLineSegment(sketch, "E104.left", {"start": v(80.66, -112.23) * mm, "end": v(80.66, -187.23) * mm, "construction": true});
            skLineSegment(sketch, "E104.right", {"start": v(78.66, -112.23) * mm, "end": v(78.66, -187.23) * mm, "construction": true});
            skLineSegment(sketch, "E105.1.0.0", {"start": v(15.86, -138.43) * mm, "end": v(-4.54, -138.43) * mm});
            skLineSegment(sketch, "E105.1.0.1", {"start": v(15.86, -118.03) * mm, "end": v(-4.54, -118.03) * mm});
            skLineSegment(sketch, "E105.1.0.2", {"start": v(15.86, -138.43) * mm, "end": v(15.86, -118.03) * mm});
            skLineSegment(sketch, "E105.1.0.3", {"start": v(-4.54, -138.43) * mm, "end": v(-4.54, -118.03) * mm});
            skLineSegment(sketch, "E105.2.0.0", {"start": v(42.86, -138.43) * mm, "end": v(22.46, -138.43) * mm});
            skLineSegment(sketch, "E105.2.0.1", {"start": v(42.86, -118.03) * mm, "end": v(22.46, -118.03) * mm});
            skLineSegment(sketch, "E105.2.0.2", {"start": v(42.86, -138.43) * mm, "end": v(42.86, -118.03) * mm});
            skLineSegment(sketch, "E105.2.0.3", {"start": v(22.46, -138.43) * mm, "end": v(22.46, -118.03) * mm});
            skLineSegment(sketch, "E105.direction1", {"start": v(-31.54, -138.43) * mm, "end": v(-4.54, -138.43) * mm, "construction": true});
            skLineSegment(sketch, "E106.1.0.0", {"start": v(-4.54, -161.43) * mm, "end": v(-4.54, -141.03) * mm});
            skLineSegment(sketch, "E106.1.0.1", {"start": v(15.86, -161.43) * mm, "end": v(15.86, -141.03) * mm});
            skLineSegment(sketch, "E106.1.0.2", {"start": v(15.86, -141.03) * mm, "end": v(-4.54, -141.03) * mm});
            skLineSegment(sketch, "E106.1.0.3", {"start": v(15.86, -161.43) * mm, "end": v(-4.54, -161.43) * mm});
            skLineSegment(sketch, "E106.2.0.0", {"start": v(22.46, -161.43) * mm, "end": v(22.46, -141.03) * mm});
            skLineSegment(sketch, "E106.2.0.1", {"start": v(42.86, -161.43) * mm, "end": v(42.86, -141.03) * mm});
            skLineSegment(sketch, "E106.2.0.2", {"start": v(42.86, -141.03) * mm, "end": v(22.46, -141.03) * mm});
            skLineSegment(sketch, "E106.2.0.3", {"start": v(42.86, -161.43) * mm, "end": v(22.46, -161.43) * mm});
            skLineSegment(sketch, "E106.direction1", {"start": v(-31.54, -161.43) * mm, "end": v(-4.54, -161.43) * mm, "construction": true});
            skPoint(sketch, "E107", {"position": v(32.66, -151.23) * mm});
            skPoint(sketch, "E107.positionSnap0", {"position": v(32.66, -141.03) * mm});
            skPoint(sketch, "E107.positionSnap1", {"position": v(22.46, -151.23) * mm});
            skPoint(sketch, "E108", {"position": v(32.66, -128.23) * mm});
            skPoint(sketch, "E108.positionSnap0", {"position": v(32.66, -118.03) * mm});
            skPoint(sketch, "E108.positionSnap1", {"position": v(42.86, -128.23) * mm});
            skCircle(sketch, "E109", {"center": v(-41.84, -174.23) * mm, "radius": 6.25 * mm});
            skCircle(sketch, "E110", {"center": v(-41.84, -151.23) * mm, "radius": 5 * mm});
            skLineSegment(sketch, "E111.bottom", {"start": v(-40.84, -156.13) * mm, "end": v(-42.84, -156.13) * mm});
            skLineSegment(sketch, "E111.top", {"start": v(-40.84, -146.33) * mm, "end": v(-42.84, -146.33) * mm});
            skLineSegment(sketch, "E111.left", {"start": v(-40.84, -156.13) * mm, "end": v(-40.84, -146.33) * mm});
            skLineSegment(sketch, "E111.right", {"start": v(-42.84, -156.13) * mm, "end": v(-42.84, -146.33) * mm});
            skLineSegment(sketch, "E112", {"start": v(-61.34, -98.05) * mm, "end": v(-61.34, -82.14) * mm, "construction": true});
            skSolve(sketch);
        }
        {
            var Q0;
            Q0=makeQuery(id+"F0.imprint","IMPRINT",FACE,{"disambiguationData":[TD([[makeQuery(id+"F0.imprint","IMPRINT",EDGE,{"derivedFrom":sQuery(id+"F0.wireOp",EDGE,"E0.bottom")}),-1.0]])]});
            var Q1;
            Q1=makeQuery(id+"F0.imprint","IMPRINT",FACE,{"disambiguationData":[TD([[makeQuery(id+"F0.imprint","IMPRINT",EDGE,{"derivedFrom":sQuery(id+"F0.wireOp",EDGE,"E20.bottom")}),-1.0]])]});
            var Q2;
            Q2=makeQuery(id+"F0.imprint","IMPRINT",FACE,{"disambiguationData":[TD([[makeQuery(id+"F0.imprint","IMPRINT",EDGE,{"derivedFrom":sQuery(id+"F0.wireOp",EDGE,"E31.bottom")}),-1.0]])]});
            var Q3;
            Q3=makeQuery(id+"F0.imprint","IMPRINT",FACE,{"disambiguationData":[TD([[makeQuery(id+"F0.imprint","IMPRINT",EDGE,{"derivedFrom":sQuery(id+"F0.wireOp",EDGE,"7093700b-8509-4908-bad7-ce82e1b1d340.1.0.0")}),-1.0]])]});
            var Q4;
            Q4=makeQuery(id+"F0.imprint","IMPRINT",FACE,{"disambiguationData":[TD([[makeQuery(id+"F0.imprint","IMPRINT",EDGE,{"derivedFrom":sQuery(id+"F0.wireOp",EDGE,"7093700b-8509-4908-bad7-ce82e1b1d340.2.0.0")}),-1.0]])]});
            var Q5;
            {var subQ3=sQuery(id+"F0.wireOp",EDGE,"c973f7c2-3bf7-4545-afce-7af64f458de9.2.0.0");Q5=makeQuery(id+"F0.imprint","IMPRINT",FACE,{"disambiguationData":[TD([[makeQuery(id+"F0.imprint","IMPRINT",EDGE,{"derivedFrom":subQ3}),1.0]])]});}
            var Q6;
            {var subQ3=sQuery(id+"F0.wireOp",EDGE,"c973f7c2-3bf7-4545-afce-7af64f458de9.1.0.0");Q6=makeQuery(id+"F0.imprint","IMPRINT",FACE,{"disambiguationData":[TD([[makeQuery(id+"F0.imprint","IMPRINT",EDGE,{"derivedFrom":subQ3}),1.0]])]});}
            var Q7;
            Q7=makeQuery(id+"F0.imprint","IMPRINT",FACE,{"disambiguationData":[TD([[makeQuery(id+"F0.imprint","IMPRINT",EDGE,{"derivedFrom":sQuery(id+"F0.wireOp",EDGE,"E44.bottom")}),-1.0]])]});
            var Q8;
            Q8=makeQuery(id+"F0.imprint","IMPRINT",FACE,{"disambiguationData":[TD([[makeQuery(id+"F0.imprint","IMPRINT",EDGE,{"derivedFrom":sQuery(id+"F0.wireOp",EDGE,"E45.bottom")}),-1.0]])]});
            var Q9;
            {var subQ0=sQuery(id+"F0.wireOp",EDGE,"E44.left");Q9=makeQuery(id+"F0.imprint","IMPRINT",FACE,{"disambiguationData":[TD([[makeQuery(id+"F0.imprint","IMPRINT",EDGE,{"derivedFrom":subQ0}),1.0]])]});}
            var Q10;
            {var subQ0=sQuery(id+"F0.wireOp",EDGE,"E45.left");Q10=makeQuery(id+"F0.imprint","IMPRINT",FACE,{"disambiguationData":[TD([[makeQuery(id+"F0.imprint","IMPRINT",EDGE,{"derivedFrom":subQ0}),1.0]])]});}
            var Q11;
            Q11=makeQuery(id+"F0.imprint","IMPRINT",FACE,{"disambiguationData":[TD([[makeQuery(id+"F0.imprint","IMPRINT",EDGE,{"derivedFrom":sQuery(id+"F0.wireOp",EDGE,"E50.1.0.0")}),1.0]])]});
            var Q12;
            Q12=makeQuery(id+"F0.imprint","IMPRINT",FACE,{"disambiguationData":[TD([[makeQuery(id+"F0.imprint","IMPRINT",EDGE,{"derivedFrom":sQuery(id+"F0.wireOp",EDGE,"E50.1.0.1")}),-1.0]])]});
            var Q13;
            Q13=makeQuery(id+"F0.imprint","IMPRINT",FACE,{"disambiguationData":[TD([[makeQuery(id+"F0.imprint","IMPRINT",EDGE,{"derivedFrom":sQuery(id+"F0.wireOp",EDGE,"E50.2.0.0")}),1.0]])]});
            var Q14;
            Q14=makeQuery(id+"F0.imprint","IMPRINT",FACE,{"disambiguationData":[TD([[makeQuery(id+"F0.imprint","IMPRINT",EDGE,{"derivedFrom":sQuery(id+"F0.wireOp",EDGE,"E50.2.0.1")}),-1.0]])]});
            var Q15;
            Q15=makeQuery(id+"F0.imprint","IMPRINT",FACE,{"disambiguationData":[TD([[makeQuery(id+"F0.imprint","IMPRINT",EDGE,{"derivedFrom":sQuery(id+"F0.wireOp",EDGE,"E53.bottom")}),-1.0]])]});
            var Q16;
            Q16=makeQuery(id+"F0.imprint","IMPRINT",FACE,{"disambiguationData":[TD([[makeQuery(id+"F0.imprint","IMPRINT",EDGE,{"derivedFrom":sQuery(id+"F0.wireOp",EDGE,"E55.bottom")}),-1.0]])]});
            extrude(context, id + "F2", {"entities" : qUnion([Q0, Q1, Q2, Q3, Q4, Q5, Q6, Q7, Q8, Q9, Q10, Q11, Q12, Q13, Q14, Q15, Q16]), "depth" : 1 * mm});
        }
        {
            var Q0;
            Q0=makeQuery(id+"F2.opExtrude","CAP_FACE",FACE,{"disambiguationData":[OSD([sQuery(id+"F0.wireOp",EDGE,"E0.bottom"),sQuery(id+"F0.wireOp",EDGE,"E0.top"),sQuery(id+"F0.wireOp",EDGE,"E0.left"),sQuery(id+"F0.wireOp",EDGE,"E0.right"),sQuery(id+"F0.wireOp",EDGE,"6XQCNLW2-68Wz-nC9p-wT4x-b90YEvEmSNLj"),sQuery(id+"F0.wireOp",EDGE,"E3"),sQuery(id+"F0.wireOp",EDGE,"E4"),sQuery(id+"F0.wireOp",EDGE,"E7"),sQuery(id+"F0.wireOp",EDGE,"E8"),sQuery(id+"F0.wireOp",EDGE,"E9"),sQuery(id+"F0.wireOp",EDGE,"E10"),sQuery(id+"F0.wireOp",EDGE,"E11"),sQuery(id+"F0.wireOp",EDGE,"E12"),sQuery(id+"F0.wireOp",EDGE,"E13"),sQuery(id+"F0.wireOp",EDGE,"E14.bottom"),sQuery(id+"F0.wireOp",EDGE,"E14.top"),sQuery(id+"F0.wireOp",EDGE,"E14.left"),sQuery(id+"F0.wireOp",EDGE,"E14.right"),sQuery(id+"F0.wireOp",EDGE,"E15"),sQuery(id+"F0.wireOp",EDGE,"E16"),sQuery(id+"F0.wireOp",EDGE,"E18.bottom"),sQuery(id+"F0.wireOp",EDGE,"E18.top"),sQuery(id+"F0.wireOp",EDGE,"E18.left"),sQuery(id+"F0.wireOp",EDGE,"E18.right"),sQuery(id+"F0.wireOp",EDGE,"E20.bottom"),sQuery(id+"F0.wireOp",EDGE,"E20.top"),sQuery(id+"F0.wireOp",EDGE,"E21.left"),sQuery(id+"F0.wireOp",EDGE,"E21.right"),sQuery(id+"F0.wireOp",EDGE,"E22.left"),sQuery(id+"F0.wireOp",EDGE,"E22.right"),sQuery(id+"F0.wireOp",EDGE,"E23.trimOffspring"),sQuery(id+"F0.wireOp",EDGE,"E24.trimOffspring"),sQuery(id+"F0.wireOp",EDGE,"E25.trimOffspring"),sQuery(id+"F0.wireOp",EDGE,"E26.trimOffspring"),sQuery(id+"F0.wireOp",EDGE,"E27.trimOffspring"),sQuery(id+"F0.wireOp",EDGE,"E28.trimOffspring"),sQuery(id+"F0.wireOp",EDGE,"E29.trimOffspring"),sQuery(id+"F0.wireOp",EDGE,"E30.trimOffspring"),sQuery(id+"F0.wireOp",EDGE,"E19.bottom"),sQuery(id+"F0.wireOp",EDGE,"E19.top"),sQuery(id+"F0.wireOp",EDGE,"E19.left"),sQuery(id+"F0.wireOp",EDGE,"E19.right"),sQuery(id+"F0.wireOp",EDGE,"E31.bottom"),sQuery(id+"F0.wireOp",EDGE,"E31.top"),sQuery(id+"F0.wireOp",EDGE,"E32.left"),sQuery(id+"F0.wireOp",EDGE,"E32.right"),sQuery(id+"F0.wireOp",EDGE,"E33.left"),sQuery(id+"F0.wireOp",EDGE,"E33.right"),sQuery(id+"F0.wireOp",EDGE,"E34.trimOffspring"),sQuery(id+"F0.wireOp",EDGE,"E35.trimOffspring"),sQuery(id+"F0.wireOp",EDGE,"E36.trimOffspring"),sQuery(id+"F0.wireOp",EDGE,"E37.trimOffspring"),sQuery(id+"F0.wireOp",EDGE,"E38.trimOffspring"),sQuery(id+"F0.wireOp",EDGE,"E39.trimOffspring"),sQuery(id+"F0.wireOp",EDGE,"E40.trimOffspring"),sQuery(id+"F0.wireOp",EDGE,"E41.trimOffspring"),sQuery(id+"F0.wireOp",EDGE,"E42.bottom"),sQuery(id+"F0.wireOp",EDGE,"E42.top"),sQuery(id+"F0.wireOp",EDGE,"E42.left"),sQuery(id+"F0.wireOp",EDGE,"E42.right"),sQuery(id+"F0.wireOp",EDGE,"E43.bottom"),sQuery(id+"F0.wireOp",EDGE,"E43.top"),sQuery(id+"F0.wireOp",EDGE,"E43.left"),sQuery(id+"F0.wireOp",EDGE,"E43.right"),sQuery(id+"F0.wireOp",EDGE,"7093700b-8509-4908-bad7-ce82e1b1d340.1.0.0"),sQuery(id+"F0.wireOp",EDGE,"7093700b-8509-4908-bad7-ce82e1b1d340.1.0.2"),sQuery(id+"F0.wireOp",EDGE,"7093700b-8509-4908-bad7-ce82e1b1d340.1.0.3"),sQuery(id+"F0.wireOp",EDGE,"7093700b-8509-4908-bad7-ce82e1b1d340.1.0.5"),sQuery(id+"F0.wireOp",EDGE,"7093700b-8509-4908-bad7-ce82e1b1d340.1.0.6"),sQuery(id+"F0.wireOp",EDGE,"7093700b-8509-4908-bad7-ce82e1b1d340.1.0.7"),sQuery(id+"F0.wireOp",EDGE,"7093700b-8509-4908-bad7-ce82e1b1d340.1.0.8"),sQuery(id+"F0.wireOp",EDGE,"7093700b-8509-4908-bad7-ce82e1b1d340.1.0.9"),sQuery(id+"F0.wireOp",EDGE,"7093700b-8509-4908-bad7-ce82e1b1d340.1.0.12"),sQuery(id+"F0.wireOp",EDGE,"7093700b-8509-4908-bad7-ce82e1b1d340.1.0.13"),sQuery(id+"F0.wireOp",EDGE,"7093700b-8509-4908-bad7-ce82e1b1d340.1.0.14"),sQuery(id+"F0.wireOp",EDGE,"7093700b-8509-4908-bad7-ce82e1b1d340.1.0.15"),sQuery(id+"F0.wireOp",EDGE,"7093700b-8509-4908-bad7-ce82e1b1d340.1.0.16"),sQuery(id+"F0.wireOp",EDGE,"7093700b-8509-4908-bad7-ce82e1b1d340.1.0.17"),sQuery(id+"F0.wireOp",EDGE,"7093700b-8509-4908-bad7-ce82e1b1d340.1.0.18"),sQuery(id+"F0.wireOp",EDGE,"7093700b-8509-4908-bad7-ce82e1b1d340.1.0.19"),sQuery(id+"F0.wireOp",EDGE,"7093700b-8509-4908-bad7-ce82e1b1d340.1.0.20"),sQuery(id+"F0.wireOp",EDGE,"7093700b-8509-4908-bad7-ce82e1b1d340.1.0.21"),sQuery(id+"F0.wireOp",EDGE,"7093700b-8509-4908-bad7-ce82e1b1d340.2.0.0"),sQuery(id+"F0.wireOp",EDGE,"7093700b-8509-4908-bad7-ce82e1b1d340.2.0.2"),sQuery(id+"F0.wireOp",EDGE,"7093700b-8509-4908-bad7-ce82e1b1d340.2.0.3"),sQuery(id+"F0.wireOp",EDGE,"7093700b-8509-4908-bad7-ce82e1b1d340.2.0.5"),sQuery(id+"F0.wireOp",EDGE,"7093700b-8509-4908-bad7-ce82e1b1d340.2.0.6"),sQuery(id+"F0.wireOp",EDGE,"7093700b-8509-4908-bad7-ce82e1b1d340.2.0.7"),sQuery(id+"F0.wireOp",EDGE,"7093700b-8509-4908-bad7-ce82e1b1d340.2.0.8"),sQuery(id+"F0.wireOp",EDGE,"7093700b-8509-4908-bad7-ce82e1b1d340.2.0.9"),sQuery(id+"F0.wireOp",EDGE,"7093700b-8509-4908-bad7-ce82e1b1d340.2.0.12"),sQuery(id+"F0.wireOp",EDGE,"7093700b-8509-4908-bad7-ce82e1b1d340.2.0.13"),sQuery(id+"F0.wireOp",EDGE,"7093700b-8509-4908-bad7-ce82e1b1d340.2.0.14"),sQuery(id+"F0.wireOp",EDGE,"7093700b-8509-4908-bad7-ce82e1b1d340.2.0.15"),sQuery(id+"F0.wireOp",EDGE,"7093700b-8509-4908-bad7-ce82e1b1d340.2.0.16"),sQuery(id+"F0.wireOp",EDGE,"7093700b-8509-4908-bad7-ce82e1b1d340.2.0.17"),sQuery(id+"F0.wireOp",EDGE,"7093700b-8509-4908-bad7-ce82e1b1d340.2.0.18"),sQuery(id+"F0.wireOp",EDGE,"7093700b-8509-4908-bad7-ce82e1b1d340.2.0.19"),sQuery(id+"F0.wireOp",EDGE,"7093700b-8509-4908-bad7-ce82e1b1d340.2.0.20"),sQuery(id+"F0.wireOp",EDGE,"7093700b-8509-4908-bad7-ce82e1b1d340.2.0.21"),sQuery(id+"F0.wireOp",EDGE,"c973f7c2-3bf7-4545-afce-7af64f458de9.1.0.0"),sQuery(id+"F0.wireOp",EDGE,"c973f7c2-3bf7-4545-afce-7af64f458de9.1.0.1"),sQuery(id+"F0.wireOp",EDGE,"c973f7c2-3bf7-4545-afce-7af64f458de9.1.0.2"),sQuery(id+"F0.wireOp",EDGE,"c973f7c2-3bf7-4545-afce-7af64f458de9.1.0.4"),sQuery(id+"F0.wireOp",EDGE,"c973f7c2-3bf7-4545-afce-7af64f458de9.1.0.6"),sQuery(id+"F0.wireOp",EDGE,"c973f7c2-3bf7-4545-afce-7af64f458de9.1.0.7"),sQuery(id+"F0.wireOp",EDGE,"c973f7c2-3bf7-4545-afce-7af64f458de9.1.0.9"),sQuery(id+"F0.wireOp",EDGE,"c973f7c2-3bf7-4545-afce-7af64f458de9.1.0.10"),sQuery(id+"F0.wireOp",EDGE,"c973f7c2-3bf7-4545-afce-7af64f458de9.1.0.12"),sQuery(id+"F0.wireOp",EDGE,"c973f7c2-3bf7-4545-afce-7af64f458de9.1.0.14"),sQuery(id+"F0.wireOp",EDGE,"c973f7c2-3bf7-4545-afce-7af64f458de9.1.0.16"),sQuery(id+"F0.wireOp",EDGE,"c973f7c2-3bf7-4545-afce-7af64f458de9.1.0.18"),sQuery(id+"F0.wireOp",EDGE,"c973f7c2-3bf7-4545-afce-7af64f458de9.1.0.19"),sQuery(id+"F0.wireOp",EDGE,"c973f7c2-3bf7-4545-afce-7af64f458de9.1.0.20"),sQuery(id+"F0.wireOp",EDGE,"c973f7c2-3bf7-4545-afce-7af64f458de9.1.0.26"),sQuery(id+"F0.wireOp",EDGE,"c973f7c2-3bf7-4545-afce-7af64f458de9.1.0.28"),sQuery(id+"F0.wireOp",EDGE,"c973f7c2-3bf7-4545-afce-7af64f458de9.1.0.29"),sQuery(id+"F0.wireOp",EDGE,"c973f7c2-3bf7-4545-afce-7af64f458de9.1.0.30"),sQuery(id+"F0.wireOp",EDGE,"c973f7c2-3bf7-4545-afce-7af64f458de9.2.0.0"),sQuery(id+"F0.wireOp",EDGE,"c973f7c2-3bf7-4545-afce-7af64f458de9.2.0.1"),sQuery(id+"F0.wireOp",EDGE,"c973f7c2-3bf7-4545-afce-7af64f458de9.2.0.2"),sQuery(id+"F0.wireOp",EDGE,"c973f7c2-3bf7-4545-afce-7af64f458de9.2.0.4"),sQuery(id+"F0.wireOp",EDGE,"c973f7c2-3bf7-4545-afce-7af64f458de9.2.0.6"),sQuery(id+"F0.wireOp",EDGE,"c973f7c2-3bf7-4545-afce-7af64f458de9.2.0.7"),sQuery(id+"F0.wireOp",EDGE,"c973f7c2-3bf7-4545-afce-7af64f458de9.2.0.9"),sQuery(id+"F0.wireOp",EDGE,"c973f7c2-3bf7-4545-afce-7af64f458de9.2.0.10"),sQuery(id+"F0.wireOp",EDGE,"c973f7c2-3bf7-4545-afce-7af64f458de9.2.0.12"),sQuery(id+"F0.wireOp",EDGE,"c973f7c2-3bf7-4545-afce-7af64f458de9.2.0.14"),sQuery(id+"F0.wireOp",EDGE,"c973f7c2-3bf7-4545-afce-7af64f458de9.2.0.16"),sQuery(id+"F0.wireOp",EDGE,"c973f7c2-3bf7-4545-afce-7af64f458de9.2.0.18"),sQuery(id+"F0.wireOp",EDGE,"c973f7c2-3bf7-4545-afce-7af64f458de9.2.0.19"),sQuery(id+"F0.wireOp",EDGE,"c973f7c2-3bf7-4545-afce-7af64f458de9.2.0.20"),sQuery(id+"F0.wireOp",EDGE,"c973f7c2-3bf7-4545-afce-7af64f458de9.2.0.26"),sQuery(id+"F0.wireOp",EDGE,"c973f7c2-3bf7-4545-afce-7af64f458de9.2.0.28"),sQuery(id+"F0.wireOp",EDGE,"c973f7c2-3bf7-4545-afce-7af64f458de9.2.0.29"),sQuery(id+"F0.wireOp",EDGE,"c973f7c2-3bf7-4545-afce-7af64f458de9.2.0.30")])],"isStart":false});
            var Q1;
            {var subQ0=sQuery(id+"F0.wireOp",EDGE,"rYwyOBXD-m5LK-rnKL-k3sO-ogXxKnliiuRN.left");Q1=makeQuery(id+"F0.imprint","IMPRINT",FACE,{"disambiguationData":[TD([[makeQuery(id+"F0.imprint","IMPRINT",EDGE,{"derivedFrom":subQ0}),1.0]])]});}
            var Q2;
            {var subQ0=sQuery(id+"F0.wireOp",EDGE,"PkneSYUR-leV3-Pqg6-8MYA-ygIsKwYRT98A.left");Q2=makeQuery(id+"F0.imprint","IMPRINT",FACE,{"disambiguationData":[TD([[makeQuery(id+"F0.imprint","IMPRINT",EDGE,{"derivedFrom":subQ0}),1.0]])]});}
            var Q3;
            {var subQ0=sQuery(id+"F0.wireOp",EDGE,"vsiTGSYA-5vz3-LSdH-l7PB-eDLQVEbj46oE.left");Q3=makeQuery(id+"F0.imprint","IMPRINT",FACE,{"disambiguationData":[TD([[makeQuery(id+"F0.imprint","IMPRINT",EDGE,{"derivedFrom":subQ0}),1.0]])]});}
            var Q4;
            {var subQ0=sQuery(id+"F0.wireOp",EDGE,"qxe8J46x-YBAU-1gLG-RRm6-GLdHy8YKuxwO.left");Q4=makeQuery(id+"F0.imprint","IMPRINT",FACE,{"disambiguationData":[TD([[makeQuery(id+"F0.imprint","IMPRINT",EDGE,{"derivedFrom":subQ0}),1.0]])]});}
            var Q5;
            Q5=makeQuery(id+"F0.imprint","IMPRINT",FACE,{"disambiguationData":[TD([[makeQuery(id+"F0.imprint","IMPRINT",EDGE,{"derivedFrom":sQuery(id+"F0.wireOp",EDGE,"E53.bottom")}),-1.0]])]});
            var Q6;
            Q6=makeQuery(id+"F0.imprint","IMPRINT",FACE,{"disambiguationData":[TD([[makeQuery(id+"F0.imprint","IMPRINT",EDGE,{"derivedFrom":sQuery(id+"F0.wireOp",EDGE,"E50.1.0.0")}),1.0]])]});
            var Q7;
            Q7=makeQuery(id+"F0.imprint","IMPRINT",FACE,{"disambiguationData":[TD([[makeQuery(id+"F0.imprint","IMPRINT",EDGE,{"derivedFrom":sQuery(id+"F0.wireOp",EDGE,"E50.1.0.1")}),-1.0]])]});
            var Q8;
            Q8=makeQuery(id+"F0.imprint","IMPRINT",FACE,{"disambiguationData":[TD([[makeQuery(id+"F0.imprint","IMPRINT",EDGE,{"derivedFrom":sQuery(id+"F0.wireOp",EDGE,"E50.2.0.1")}),-1.0]])]});
            var Q9;
            Q9=makeQuery(id+"F0.imprint","IMPRINT",FACE,{"disambiguationData":[TD([[makeQuery(id+"F0.imprint","IMPRINT",EDGE,{"derivedFrom":sQuery(id+"F0.wireOp",EDGE,"E50.2.0.0")}),1.0]])]});
            extrude(context, id + "F3", {"entities" : qUnion([Q0, Q1, Q2, Q3, Q4, Q5, Q6, Q7, Q8, Q9]), "operationType" : NewBodyOperationType.ADD, "depth" : 5 * mm});
        }
        {
            var Q0;
            Q0=makeQuery(id+"F3.opExtrude","CAP_FACE",FACE,{"disambiguationData":[OSD([sQuery(id+"F0.wireOp",EDGE,"E0.bottom"),sQuery(id+"F0.wireOp",EDGE,"E0.top"),sQuery(id+"F0.wireOp",EDGE,"E0.left"),sQuery(id+"F0.wireOp",EDGE,"E0.right"),sQuery(id+"F0.wireOp",EDGE,"6XQCNLW2-68Wz-nC9p-wT4x-b90YEvEmSNLj"),sQuery(id+"F0.wireOp",EDGE,"E3"),sQuery(id+"F0.wireOp",EDGE,"E4"),sQuery(id+"F0.wireOp",EDGE,"E7"),sQuery(id+"F0.wireOp",EDGE,"E8"),sQuery(id+"F0.wireOp",EDGE,"E9"),sQuery(id+"F0.wireOp",EDGE,"E10"),sQuery(id+"F0.wireOp",EDGE,"E11"),sQuery(id+"F0.wireOp",EDGE,"E12"),sQuery(id+"F0.wireOp",EDGE,"E13"),sQuery(id+"F0.wireOp",EDGE,"E14.bottom"),sQuery(id+"F0.wireOp",EDGE,"E14.top"),sQuery(id+"F0.wireOp",EDGE,"E14.left"),sQuery(id+"F0.wireOp",EDGE,"E14.right"),sQuery(id+"F0.wireOp",EDGE,"E15"),sQuery(id+"F0.wireOp",EDGE,"E16"),sQuery(id+"F0.wireOp",EDGE,"E18.bottom"),sQuery(id+"F0.wireOp",EDGE,"E18.top"),sQuery(id+"F0.wireOp",EDGE,"E18.left"),sQuery(id+"F0.wireOp",EDGE,"E18.right"),sQuery(id+"F0.wireOp",EDGE,"E20.bottom"),sQuery(id+"F0.wireOp",EDGE,"E20.top"),sQuery(id+"F0.wireOp",EDGE,"E21.left"),sQuery(id+"F0.wireOp",EDGE,"E21.right"),sQuery(id+"F0.wireOp",EDGE,"E22.left"),sQuery(id+"F0.wireOp",EDGE,"E22.right"),sQuery(id+"F0.wireOp",EDGE,"E23.trimOffspring"),sQuery(id+"F0.wireOp",EDGE,"E24.trimOffspring"),sQuery(id+"F0.wireOp",EDGE,"E25.trimOffspring"),sQuery(id+"F0.wireOp",EDGE,"E26.trimOffspring"),sQuery(id+"F0.wireOp",EDGE,"E27.trimOffspring"),sQuery(id+"F0.wireOp",EDGE,"E28.trimOffspring"),sQuery(id+"F0.wireOp",EDGE,"E29.trimOffspring"),sQuery(id+"F0.wireOp",EDGE,"E30.trimOffspring"),sQuery(id+"F0.wireOp",EDGE,"E19.bottom"),sQuery(id+"F0.wireOp",EDGE,"E19.top"),sQuery(id+"F0.wireOp",EDGE,"E19.left"),sQuery(id+"F0.wireOp",EDGE,"E19.right"),sQuery(id+"F0.wireOp",EDGE,"E31.bottom"),sQuery(id+"F0.wireOp",EDGE,"E31.top"),sQuery(id+"F0.wireOp",EDGE,"E32.left"),sQuery(id+"F0.wireOp",EDGE,"E32.right"),sQuery(id+"F0.wireOp",EDGE,"E33.left"),sQuery(id+"F0.wireOp",EDGE,"E33.right"),sQuery(id+"F0.wireOp",EDGE,"E34.trimOffspring"),sQuery(id+"F0.wireOp",EDGE,"E35.trimOffspring"),sQuery(id+"F0.wireOp",EDGE,"E36.trimOffspring"),sQuery(id+"F0.wireOp",EDGE,"E37.trimOffspring"),sQuery(id+"F0.wireOp",EDGE,"E38.trimOffspring"),sQuery(id+"F0.wireOp",EDGE,"E39.trimOffspring"),sQuery(id+"F0.wireOp",EDGE,"E40.trimOffspring"),sQuery(id+"F0.wireOp",EDGE,"E41.trimOffspring"),sQuery(id+"F0.wireOp",EDGE,"E42.bottom"),sQuery(id+"F0.wireOp",EDGE,"E42.top"),sQuery(id+"F0.wireOp",EDGE,"E42.left"),sQuery(id+"F0.wireOp",EDGE,"E42.right"),sQuery(id+"F0.wireOp",EDGE,"E43.bottom"),sQuery(id+"F0.wireOp",EDGE,"E43.top"),sQuery(id+"F0.wireOp",EDGE,"E43.left"),sQuery(id+"F0.wireOp",EDGE,"E43.right"),sQuery(id+"F0.wireOp",EDGE,"7093700b-8509-4908-bad7-ce82e1b1d340.1.0.0"),sQuery(id+"F0.wireOp",EDGE,"7093700b-8509-4908-bad7-ce82e1b1d340.1.0.2"),sQuery(id+"F0.wireOp",EDGE,"7093700b-8509-4908-bad7-ce82e1b1d340.1.0.3"),sQuery(id+"F0.wireOp",EDGE,"7093700b-8509-4908-bad7-ce82e1b1d340.1.0.5"),sQuery(id+"F0.wireOp",EDGE,"7093700b-8509-4908-bad7-ce82e1b1d340.1.0.6"),sQuery(id+"F0.wireOp",EDGE,"7093700b-8509-4908-bad7-ce82e1b1d340.1.0.7"),sQuery(id+"F0.wireOp",EDGE,"7093700b-8509-4908-bad7-ce82e1b1d340.1.0.8"),sQuery(id+"F0.wireOp",EDGE,"7093700b-8509-4908-bad7-ce82e1b1d340.1.0.9"),sQuery(id+"F0.wireOp",EDGE,"7093700b-8509-4908-bad7-ce82e1b1d340.1.0.12"),sQuery(id+"F0.wireOp",EDGE,"7093700b-8509-4908-bad7-ce82e1b1d340.1.0.13"),sQuery(id+"F0.wireOp",EDGE,"7093700b-8509-4908-bad7-ce82e1b1d340.1.0.14"),sQuery(id+"F0.wireOp",EDGE,"7093700b-8509-4908-bad7-ce82e1b1d340.1.0.15"),sQuery(id+"F0.wireOp",EDGE,"7093700b-8509-4908-bad7-ce82e1b1d340.1.0.16"),sQuery(id+"F0.wireOp",EDGE,"7093700b-8509-4908-bad7-ce82e1b1d340.1.0.17"),sQuery(id+"F0.wireOp",EDGE,"7093700b-8509-4908-bad7-ce82e1b1d340.1.0.18"),sQuery(id+"F0.wireOp",EDGE,"7093700b-8509-4908-bad7-ce82e1b1d340.1.0.19"),sQuery(id+"F0.wireOp",EDGE,"7093700b-8509-4908-bad7-ce82e1b1d340.1.0.20"),sQuery(id+"F0.wireOp",EDGE,"7093700b-8509-4908-bad7-ce82e1b1d340.1.0.21"),sQuery(id+"F0.wireOp",EDGE,"7093700b-8509-4908-bad7-ce82e1b1d340.2.0.0"),sQuery(id+"F0.wireOp",EDGE,"7093700b-8509-4908-bad7-ce82e1b1d340.2.0.2"),sQuery(id+"F0.wireOp",EDGE,"7093700b-8509-4908-bad7-ce82e1b1d340.2.0.3"),sQuery(id+"F0.wireOp",EDGE,"7093700b-8509-4908-bad7-ce82e1b1d340.2.0.5"),sQuery(id+"F0.wireOp",EDGE,"7093700b-8509-4908-bad7-ce82e1b1d340.2.0.6"),sQuery(id+"F0.wireOp",EDGE,"7093700b-8509-4908-bad7-ce82e1b1d340.2.0.7"),sQuery(id+"F0.wireOp",EDGE,"7093700b-8509-4908-bad7-ce82e1b1d340.2.0.8"),sQuery(id+"F0.wireOp",EDGE,"7093700b-8509-4908-bad7-ce82e1b1d340.2.0.9"),sQuery(id+"F0.wireOp",EDGE,"7093700b-8509-4908-bad7-ce82e1b1d340.2.0.12"),sQuery(id+"F0.wireOp",EDGE,"7093700b-8509-4908-bad7-ce82e1b1d340.2.0.13"),sQuery(id+"F0.wireOp",EDGE,"7093700b-8509-4908-bad7-ce82e1b1d340.2.0.14"),sQuery(id+"F0.wireOp",EDGE,"7093700b-8509-4908-bad7-ce82e1b1d340.2.0.15"),sQuery(id+"F0.wireOp",EDGE,"7093700b-8509-4908-bad7-ce82e1b1d340.2.0.16"),sQuery(id+"F0.wireOp",EDGE,"7093700b-8509-4908-bad7-ce82e1b1d340.2.0.17"),sQuery(id+"F0.wireOp",EDGE,"7093700b-8509-4908-bad7-ce82e1b1d340.2.0.18"),sQuery(id+"F0.wireOp",EDGE,"7093700b-8509-4908-bad7-ce82e1b1d340.2.0.19"),sQuery(id+"F0.wireOp",EDGE,"7093700b-8509-4908-bad7-ce82e1b1d340.2.0.20"),sQuery(id+"F0.wireOp",EDGE,"7093700b-8509-4908-bad7-ce82e1b1d340.2.0.21"),sQuery(id+"F0.wireOp",EDGE,"c973f7c2-3bf7-4545-afce-7af64f458de9.1.0.0"),sQuery(id+"F0.wireOp",EDGE,"c973f7c2-3bf7-4545-afce-7af64f458de9.1.0.1"),sQuery(id+"F0.wireOp",EDGE,"c973f7c2-3bf7-4545-afce-7af64f458de9.1.0.2"),sQuery(id+"F0.wireOp",EDGE,"c973f7c2-3bf7-4545-afce-7af64f458de9.1.0.4"),sQuery(id+"F0.wireOp",EDGE,"c973f7c2-3bf7-4545-afce-7af64f458de9.1.0.6"),sQuery(id+"F0.wireOp",EDGE,"c973f7c2-3bf7-4545-afce-7af64f458de9.1.0.7"),sQuery(id+"F0.wireOp",EDGE,"c973f7c2-3bf7-4545-afce-7af64f458de9.1.0.9"),sQuery(id+"F0.wireOp",EDGE,"c973f7c2-3bf7-4545-afce-7af64f458de9.1.0.10"),sQuery(id+"F0.wireOp",EDGE,"c973f7c2-3bf7-4545-afce-7af64f458de9.1.0.12"),sQuery(id+"F0.wireOp",EDGE,"c973f7c2-3bf7-4545-afce-7af64f458de9.1.0.14"),sQuery(id+"F0.wireOp",EDGE,"c973f7c2-3bf7-4545-afce-7af64f458de9.1.0.16"),sQuery(id+"F0.wireOp",EDGE,"c973f7c2-3bf7-4545-afce-7af64f458de9.1.0.18"),sQuery(id+"F0.wireOp",EDGE,"c973f7c2-3bf7-4545-afce-7af64f458de9.1.0.19"),sQuery(id+"F0.wireOp",EDGE,"c973f7c2-3bf7-4545-afce-7af64f458de9.1.0.20"),sQuery(id+"F0.wireOp",EDGE,"c973f7c2-3bf7-4545-afce-7af64f458de9.1.0.26"),sQuery(id+"F0.wireOp",EDGE,"c973f7c2-3bf7-4545-afce-7af64f458de9.1.0.28"),sQuery(id+"F0.wireOp",EDGE,"c973f7c2-3bf7-4545-afce-7af64f458de9.1.0.29"),sQuery(id+"F0.wireOp",EDGE,"c973f7c2-3bf7-4545-afce-7af64f458de9.1.0.30"),sQuery(id+"F0.wireOp",EDGE,"c973f7c2-3bf7-4545-afce-7af64f458de9.2.0.0"),sQuery(id+"F0.wireOp",EDGE,"c973f7c2-3bf7-4545-afce-7af64f458de9.2.0.1"),sQuery(id+"F0.wireOp",EDGE,"c973f7c2-3bf7-4545-afce-7af64f458de9.2.0.2"),sQuery(id+"F0.wireOp",EDGE,"c973f7c2-3bf7-4545-afce-7af64f458de9.2.0.4"),sQuery(id+"F0.wireOp",EDGE,"c973f7c2-3bf7-4545-afce-7af64f458de9.2.0.6"),sQuery(id+"F0.wireOp",EDGE,"c973f7c2-3bf7-4545-afce-7af64f458de9.2.0.7"),sQuery(id+"F0.wireOp",EDGE,"c973f7c2-3bf7-4545-afce-7af64f458de9.2.0.9"),sQuery(id+"F0.wireOp",EDGE,"c973f7c2-3bf7-4545-afce-7af64f458de9.2.0.10"),sQuery(id+"F0.wireOp",EDGE,"c973f7c2-3bf7-4545-afce-7af64f458de9.2.0.12"),sQuery(id+"F0.wireOp",EDGE,"c973f7c2-3bf7-4545-afce-7af64f458de9.2.0.14"),sQuery(id+"F0.wireOp",EDGE,"c973f7c2-3bf7-4545-afce-7af64f458de9.2.0.16"),sQuery(id+"F0.wireOp",EDGE,"c973f7c2-3bf7-4545-afce-7af64f458de9.2.0.18"),sQuery(id+"F0.wireOp",EDGE,"c973f7c2-3bf7-4545-afce-7af64f458de9.2.0.19"),sQuery(id+"F0.wireOp",EDGE,"c973f7c2-3bf7-4545-afce-7af64f458de9.2.0.20"),sQuery(id+"F0.wireOp",EDGE,"c973f7c2-3bf7-4545-afce-7af64f458de9.2.0.26"),sQuery(id+"F0.wireOp",EDGE,"c973f7c2-3bf7-4545-afce-7af64f458de9.2.0.28"),sQuery(id+"F0.wireOp",EDGE,"c973f7c2-3bf7-4545-afce-7af64f458de9.2.0.29"),sQuery(id+"F0.wireOp",EDGE,"c973f7c2-3bf7-4545-afce-7af64f458de9.2.0.30")])],"isStart":false});
            var sketch = newSketch(context, id + "F4", { "sketchPlane" : qUnion([Q0])});
            skPoint(sketch, "E113.0", {"position": v(-109.5, 1.96) * mm});
            skLineSegment(sketch, "E114.bottom", {"start": v(-100.5, -7.04) * mm, "end": v(-118.5, -7.04) * mm});
            skLineSegment(sketch, "E114.top", {"start": v(-100.5, 10.96) * mm, "end": v(-118.5, 10.96) * mm});
            skLineSegment(sketch, "E114.left", {"start": v(-100.5, -7.04) * mm, "end": v(-100.5, 10.96) * mm});
            skLineSegment(sketch, "E114.right", {"start": v(-118.5, -7.04) * mm, "end": v(-118.5, 10.96) * mm});
            skPoint(sketch, "E115.0", {"position": v(-109.5, -21.04) * mm});
            skLineSegment(sketch, "E116.bottom", {"start": v(-100.5, -30.04) * mm, "end": v(-118.5, -30.04) * mm});
            skLineSegment(sketch, "E116.top", {"start": v(-100.5, -12.04) * mm, "end": v(-118.5, -12.04) * mm});
            skLineSegment(sketch, "E116.left", {"start": v(-100.5, -30.04) * mm, "end": v(-100.5, -12.04) * mm});
            skLineSegment(sketch, "E116.right", {"start": v(-118.5, -30.04) * mm, "end": v(-118.5, -12.04) * mm});
            skPoint(sketch, "E117.0", {"position": v(-119.5, -21.04) * mm});
            skPoint(sketch, "E117.1", {"position": v(-119.5, 1.96) * mm});
            skLineSegment(sketch, "E118.bottom", {"start": v(-118.5, -5.54) * mm, "end": v(-120.5, -5.54) * mm});
            skLineSegment(sketch, "E118.top", {"start": v(-118.5, 9.46) * mm, "end": v(-120.5, 9.46) * mm});
            skLineSegment(sketch, "E118.left", {"start": v(-118.5, -5.54) * mm, "end": v(-118.5, 9.46) * mm});
            skLineSegment(sketch, "E118.right", {"start": v(-120.5, -5.54) * mm, "end": v(-120.5, 9.46) * mm});
            skPoint(sketch, "E119.0", {"position": v(-99.5, 1.96) * mm});
            skLineSegment(sketch, "E120.bottom", {"start": v(-100.5, -5.54) * mm, "end": v(-98.5, -5.54) * mm});
            skLineSegment(sketch, "E120.top", {"start": v(-100.5, 9.46) * mm, "end": v(-98.5, 9.46) * mm});
            skLineSegment(sketch, "E120.left", {"start": v(-100.5, -5.54) * mm, "end": v(-100.5, 9.46) * mm});
            skLineSegment(sketch, "E120.right", {"start": v(-98.5, -5.54) * mm, "end": v(-98.5, 9.46) * mm});
            skPoint(sketch, "E121.0", {"position": v(-99.5, -21.04) * mm});
            skPoint(sketch, "E122.0", {"position": v(-130, 1.96) * mm});
            skPoint(sketch, "E122.1", {"position": v(-130, -21.04) * mm});
            skCircle(sketch, "E123", {"center": v(-130, 1.96) * mm, "radius": 5 * mm});
            skCircle(sketch, "E124", {"center": v(-130, -21.04) * mm, "radius": 5 * mm});
            skLineSegment(sketch, "E125.bottom", {"start": v(-118.5, -28.54) * mm, "end": v(-120.5, -28.54) * mm});
            skLineSegment(sketch, "E125.top", {"start": v(-118.5, -13.54) * mm, "end": v(-120.5, -13.54) * mm});
            skLineSegment(sketch, "E125.left", {"start": v(-118.5, -28.54) * mm, "end": v(-118.5, -13.54) * mm});
            skLineSegment(sketch, "E125.right", {"start": v(-120.5, -28.54) * mm, "end": v(-120.5, -13.54) * mm});
            skLineSegment(sketch, "E126.bottom", {"start": v(-98.5, -28.54) * mm, "end": v(-100.5, -28.54) * mm});
            skLineSegment(sketch, "E126.top", {"start": v(-98.5, -13.54) * mm, "end": v(-100.5, -13.54) * mm});
            skLineSegment(sketch, "E126.left", {"start": v(-98.5, -28.54) * mm, "end": v(-98.5, -13.54) * mm});
            skLineSegment(sketch, "E126.right", {"start": v(-100.5, -28.54) * mm, "end": v(-100.5, -13.54) * mm});
            skLineSegment(sketch, "E127.1.0.0", {"start": v(-91.5, -5.54) * mm, "end": v(-93.5, -5.54) * mm});
            skLineSegment(sketch, "E127.1.0.1", {"start": v(-91.5, 9.46) * mm, "end": v(-93.5, 9.46) * mm});
            skLineSegment(sketch, "E127.1.0.2", {"start": v(-73.5, 9.46) * mm, "end": v(-71.5, 9.46) * mm});
            skPoint(sketch, "E127.1.0.3", {"position": v(-82.5, 1.96) * mm});
            skLineSegment(sketch, "E127.1.0.4", {"start": v(-73.5, -5.54) * mm, "end": v(-71.5, -5.54) * mm});
            skPoint(sketch, "E127.1.0.5", {"position": v(-72.5, 1.96) * mm});
            skLineSegment(sketch, "E127.1.0.6", {"start": v(-71.5, -5.54) * mm, "end": v(-71.5, 9.46) * mm});
            skLineSegment(sketch, "E127.1.0.7", {"start": v(-91.5, -7.04) * mm, "end": v(-91.5, 10.96) * mm});
            skPoint(sketch, "E127.1.0.8", {"position": v(-92.5, 1.96) * mm});
            skLineSegment(sketch, "E127.1.0.9", {"start": v(-73.5, 10.96) * mm, "end": v(-91.5, 10.96) * mm});
            skLineSegment(sketch, "E127.1.0.10", {"start": v(-73.5, -7.04) * mm, "end": v(-91.5, -7.04) * mm});
            skLineSegment(sketch, "E127.1.0.11", {"start": v(-93.5, -5.54) * mm, "end": v(-93.5, 9.46) * mm});
            skLineSegment(sketch, "E127.1.0.12", {"start": v(-73.5, -7.04) * mm, "end": v(-73.5, 10.96) * mm});
            skPoint(sketch, "E127.1.0.13", {"position": v(-92.5, 1.96) * mm});
            skLineSegment(sketch, "E127.1.0.14", {"start": v(-73.5, -5.54) * mm, "end": v(-73.5, 9.46) * mm});
            skPoint(sketch, "E127.1.0.15", {"position": v(-82.5, 1.96) * mm});
            skLineSegment(sketch, "E127.1.0.16", {"start": v(-91.5, -5.54) * mm, "end": v(-91.5, 9.46) * mm});
            skPoint(sketch, "E127.1.0.17", {"position": v(-72.5, 1.96) * mm});
            skLineSegment(sketch, "E127.2.0.0", {"start": v(-64.5, -5.54) * mm, "end": v(-66.5, -5.54) * mm});
            skLineSegment(sketch, "E127.2.0.1", {"start": v(-64.5, 9.46) * mm, "end": v(-66.5, 9.46) * mm});
            skLineSegment(sketch, "E127.2.0.2", {"start": v(-46.5, 9.46) * mm, "end": v(-44.5, 9.46) * mm});
            skPoint(sketch, "E127.2.0.3", {"position": v(-55.5, 1.96) * mm});
            skLineSegment(sketch, "E127.2.0.4", {"start": v(-46.5, -5.54) * mm, "end": v(-44.5, -5.54) * mm});
            skPoint(sketch, "E127.2.0.5", {"position": v(-45.5, 1.96) * mm});
            skLineSegment(sketch, "E127.2.0.6", {"start": v(-44.5, -5.54) * mm, "end": v(-44.5, 9.46) * mm});
            skLineSegment(sketch, "E127.2.0.7", {"start": v(-64.5, -7.04) * mm, "end": v(-64.5, 10.96) * mm});
            skPoint(sketch, "E127.2.0.8", {"position": v(-65.5, 1.96) * mm});
            skLineSegment(sketch, "E127.2.0.9", {"start": v(-46.5, 10.96) * mm, "end": v(-64.5, 10.96) * mm});
            skLineSegment(sketch, "E127.2.0.10", {"start": v(-46.5, -7.04) * mm, "end": v(-64.5, -7.04) * mm});
            skLineSegment(sketch, "E127.2.0.11", {"start": v(-66.5, -5.54) * mm, "end": v(-66.5, 9.46) * mm});
            skLineSegment(sketch, "E127.2.0.12", {"start": v(-46.5, -7.04) * mm, "end": v(-46.5, 10.96) * mm});
            skPoint(sketch, "E127.2.0.13", {"position": v(-65.5, 1.96) * mm});
            skLineSegment(sketch, "E127.2.0.14", {"start": v(-46.5, -5.54) * mm, "end": v(-46.5, 9.46) * mm});
            skPoint(sketch, "E127.2.0.15", {"position": v(-55.5, 1.96) * mm});
            skLineSegment(sketch, "E127.2.0.16", {"start": v(-64.5, -5.54) * mm, "end": v(-64.5, 9.46) * mm});
            skPoint(sketch, "E127.2.0.17", {"position": v(-45.5, 1.96) * mm});
            skLineSegment(sketch, "E127.direction1", {"start": v(-120.5, -5.54) * mm, "end": v(-93.5, -5.54) * mm, "construction": true});
            skLineSegment(sketch, "E128.1.0.0", {"start": v(-71.5, -13.54) * mm, "end": v(-73.5, -13.54) * mm});
            skLineSegment(sketch, "E128.1.0.1", {"start": v(-71.5, -28.54) * mm, "end": v(-73.5, -28.54) * mm});
            skLineSegment(sketch, "E128.1.0.2", {"start": v(-91.5, -13.54) * mm, "end": v(-93.5, -13.54) * mm});
            skLineSegment(sketch, "E128.1.0.3", {"start": v(-73.5, -12.04) * mm, "end": v(-91.5, -12.04) * mm});
            skLineSegment(sketch, "E128.1.0.4", {"start": v(-71.5, -28.54) * mm, "end": v(-71.5, -13.54) * mm});
            skLineSegment(sketch, "E128.1.0.5", {"start": v(-73.5, -30.04) * mm, "end": v(-73.5, -12.04) * mm});
            skLineSegment(sketch, "E128.1.0.6", {"start": v(-93.5, -28.54) * mm, "end": v(-93.5, -13.54) * mm});
            skLineSegment(sketch, "E128.1.0.7", {"start": v(-91.5, -28.54) * mm, "end": v(-93.5, -28.54) * mm});
            skLineSegment(sketch, "E128.1.0.8", {"start": v(-73.5, -30.04) * mm, "end": v(-91.5, -30.04) * mm});
            skPoint(sketch, "E128.1.0.9", {"position": v(-92.5, -21.04) * mm});
            skPoint(sketch, "E128.1.0.10", {"position": v(-72.5, -21.04) * mm});
            skLineSegment(sketch, "E128.1.0.11", {"start": v(-91.5, -30.04) * mm, "end": v(-91.5, -12.04) * mm});
            skPoint(sketch, "E128.1.0.12", {"position": v(-82.5, -21.04) * mm});
            skPoint(sketch, "E128.1.0.13", {"position": v(-72.5, -21.04) * mm});
            skPoint(sketch, "E128.1.0.14", {"position": v(-92.5, -21.04) * mm});
            skPoint(sketch, "E128.1.0.15", {"position": v(-82.5, -21.04) * mm});
            skLineSegment(sketch, "E128.1.0.16", {"start": v(-91.5, -28.54) * mm, "end": v(-91.5, -13.54) * mm});
            skLineSegment(sketch, "E128.1.0.17", {"start": v(-73.5, -28.54) * mm, "end": v(-73.5, -13.54) * mm});
            skPoint(sketch, "E128.1.0.18", {"position": v(-72.5, -21.04) * mm});
            skPoint(sketch, "E128.1.0.19", {"position": v(-92.5, -21.04) * mm});
            skLineSegment(sketch, "E128.2.0.0", {"start": v(-44.5, -13.54) * mm, "end": v(-46.5, -13.54) * mm});
            skLineSegment(sketch, "E128.2.0.1", {"start": v(-44.5, -28.54) * mm, "end": v(-46.5, -28.54) * mm});
            skLineSegment(sketch, "E128.2.0.2", {"start": v(-64.5, -13.54) * mm, "end": v(-66.5, -13.54) * mm});
            skLineSegment(sketch, "E128.2.0.3", {"start": v(-46.5, -12.04) * mm, "end": v(-64.5, -12.04) * mm});
            skLineSegment(sketch, "E128.2.0.4", {"start": v(-44.5, -28.54) * mm, "end": v(-44.5, -13.54) * mm});
            skLineSegment(sketch, "E128.2.0.5", {"start": v(-46.5, -30.04) * mm, "end": v(-46.5, -12.04) * mm});
            skLineSegment(sketch, "E128.2.0.6", {"start": v(-66.5, -28.54) * mm, "end": v(-66.5, -13.54) * mm});
            skLineSegment(sketch, "E128.2.0.7", {"start": v(-64.5, -28.54) * mm, "end": v(-66.5, -28.54) * mm});
            skLineSegment(sketch, "E128.2.0.8", {"start": v(-46.5, -30.04) * mm, "end": v(-64.5, -30.04) * mm});
            skPoint(sketch, "E128.2.0.9", {"position": v(-65.5, -21.04) * mm});
            skPoint(sketch, "E128.2.0.10", {"position": v(-45.5, -21.04) * mm});
            skLineSegment(sketch, "E128.2.0.11", {"start": v(-64.5, -30.04) * mm, "end": v(-64.5, -12.04) * mm});
            skPoint(sketch, "E128.2.0.12", {"position": v(-55.5, -21.04) * mm});
            skPoint(sketch, "E128.2.0.13", {"position": v(-45.5, -21.04) * mm});
            skPoint(sketch, "E128.2.0.14", {"position": v(-65.5, -21.04) * mm});
            skPoint(sketch, "E128.2.0.15", {"position": v(-55.5, -21.04) * mm});
            skLineSegment(sketch, "E128.2.0.16", {"start": v(-64.5, -28.54) * mm, "end": v(-64.5, -13.54) * mm});
            skLineSegment(sketch, "E128.2.0.17", {"start": v(-46.5, -28.54) * mm, "end": v(-46.5, -13.54) * mm});
            skPoint(sketch, "E128.2.0.18", {"position": v(-45.5, -21.04) * mm});
            skPoint(sketch, "E128.2.0.19", {"position": v(-65.5, -21.04) * mm});
            skLineSegment(sketch, "E128.direction1", {"start": v(-120.5, -28.54) * mm, "end": v(-93.5, -28.54) * mm, "construction": true});
            skSolve(sketch);
        }
        {
            var Q0;
            Q0=qSketchRegion(id+"F4",true);
            extrude(context, id + "F5", {"entities" : qUnion([Q0]), "operationType" : NewBodyOperationType.REMOVE, "oppositeDirection" : true, "depth" : 5 * mm});
        }
        {
            var Q0;
            Q0=qCreatedBy(makeId("Top.planeOp"),FACE);
            var sketch = newSketch(context, id + "F6", { "sketchPlane" : qUnion([Q0])});
            skLineSegment(sketch, "E129.bottom", {"start": v(-106.79, 77.03) * mm, "end": v(-126.79, 77.03) * mm});
            skLineSegment(sketch, "E129.top", {"start": v(-106.79, 97.03) * mm, "end": v(-126.79, 97.03) * mm});
            skLineSegment(sketch, "E129.left", {"start": v(-106.79, 77.03) * mm, "end": v(-106.79, 97.03) * mm});
            skLineSegment(sketch, "E129.right", {"start": v(-126.79, 77.03) * mm, "end": v(-126.79, 97.03) * mm});
            skPoint(sketch, "E129.middle", {"position": v(-116.79, 87.03) * mm});
            skLineSegment(sketch, "E130.bottom", {"start": v(-105.79, 82.03) * mm, "end": v(-107.79, 82.03) * mm});
            skLineSegment(sketch, "E130.top", {"start": v(-105.79, 92.03) * mm, "end": v(-107.79, 92.03) * mm});
            skLineSegment(sketch, "E130.left", {"start": v(-105.79, 82.03) * mm, "end": v(-105.79, 92.03) * mm});
            skLineSegment(sketch, "E130.right", {"start": v(-107.79, 82.03) * mm, "end": v(-107.79, 92.03) * mm});
            skPoint(sketch, "E130.middle", {"position": v(-106.79, 87.03) * mm});
            skLineSegment(sketch, "E131.bottom", {"start": v(-125.79, 82.03) * mm, "end": v(-127.79, 82.03) * mm});
            skLineSegment(sketch, "E131.top", {"start": v(-125.79, 92.03) * mm, "end": v(-127.79, 92.03) * mm});
            skLineSegment(sketch, "E131.left", {"start": v(-125.79, 82.03) * mm, "end": v(-125.79, 92.03) * mm});
            skLineSegment(sketch, "E131.right", {"start": v(-127.79, 82.03) * mm, "end": v(-127.79, 92.03) * mm});
            skPoint(sketch, "E131.middle", {"position": v(-126.79, 87.03) * mm});
            skLineSegment(sketch, "E132.bottom", {"start": v(-107.79, 78.03) * mm, "end": v(-125.79, 78.03) * mm});
            skLineSegment(sketch, "E132.top", {"start": v(-107.79, 96.03) * mm, "end": v(-125.79, 96.03) * mm});
            skLineSegment(sketch, "E132.left", {"start": v(-107.79, 78.03) * mm, "end": v(-107.79, 96.03) * mm});
            skLineSegment(sketch, "E132.right", {"start": v(-125.79, 78.03) * mm, "end": v(-125.79, 96.03) * mm});
            skLineSegment(sketch, "E133.bottom", {"start": v(-107.79, 86.53) * mm, "end": v(-125.79, 86.53) * mm});
            skLineSegment(sketch, "E133.top", {"start": v(-107.79, 87.53) * mm, "end": v(-125.79, 87.53) * mm});
            skLineSegment(sketch, "E133.left", {"start": v(-107.79, 86.53) * mm, "end": v(-107.79, 87.53) * mm});
            skLineSegment(sketch, "E133.right", {"start": v(-125.79, 86.53) * mm, "end": v(-125.79, 87.53) * mm});
            skLineSegment(sketch, "E134.bottom", {"start": v(-115.79, 85.78) * mm, "end": v(-117.79, 85.78) * mm, "construction": true});
            skLineSegment(sketch, "E134.top", {"start": v(-115.79, 88.28) * mm, "end": v(-117.79, 88.28) * mm, "construction": true});
            skLineSegment(sketch, "E134.left", {"start": v(-115.79, 85.78) * mm, "end": v(-115.79, 88.28) * mm, "construction": true});
            skLineSegment(sketch, "E134.right", {"start": v(-117.79, 85.78) * mm, "end": v(-117.79, 88.28) * mm, "construction": true});
            skLineSegment(sketch, "E135.bottom", {"start": v(-110.82, 38.4) * mm, "end": v(-132.62, 38.4) * mm});
            skLineSegment(sketch, "E135.top", {"start": v(-110.82, 60.2) * mm, "end": v(-132.62, 60.2) * mm});
            skLineSegment(sketch, "E135.left", {"start": v(-110.82, 38.4) * mm, "end": v(-110.82, 60.2) * mm});
            skLineSegment(sketch, "E135.right", {"start": v(-132.62, 38.4) * mm, "end": v(-132.62, 60.2) * mm});
            skPoint(sketch, "E135.middle", {"position": v(-121.72, 49.3) * mm});
            skLineSegment(sketch, "E136.bottom", {"start": v(-110.82, 41.9) * mm, "end": v(-112.62, 41.9) * mm});
            skLineSegment(sketch, "E136.top", {"start": v(-110.82, 56.7) * mm, "end": v(-112.62, 56.7) * mm});
            skLineSegment(sketch, "E136.left", {"start": v(-110.82, 41.9) * mm, "end": v(-110.82, 56.7) * mm});
            skLineSegment(sketch, "E136.right", {"start": v(-112.62, 41.9) * mm, "end": v(-112.62, 56.7) * mm});
            skPoint(sketch, "E136.middle", {"position": v(-111.72, 49.3) * mm});
            skLineSegment(sketch, "E137.bottom", {"start": v(-130.82, 41.9) * mm, "end": v(-132.62, 41.9) * mm});
            skLineSegment(sketch, "E137.top", {"start": v(-130.82, 56.7) * mm, "end": v(-132.62, 56.7) * mm});
            skLineSegment(sketch, "E137.left", {"start": v(-130.82, 41.9) * mm, "end": v(-130.82, 56.7) * mm});
            skLineSegment(sketch, "E137.right", {"start": v(-132.62, 41.9) * mm, "end": v(-132.62, 56.7) * mm});
            skPoint(sketch, "E137.middle", {"position": v(-131.72, 49.3) * mm});
            skLineSegment(sketch, "E138.bottom", {"start": v(-112.62, 40.2) * mm, "end": v(-130.82, 40.2) * mm});
            skLineSegment(sketch, "E138.top", {"start": v(-112.62, 58.4) * mm, "end": v(-130.82, 58.4) * mm});
            skLineSegment(sketch, "E138.left", {"start": v(-112.62, 40.2) * mm, "end": v(-112.62, 58.4) * mm});
            skLineSegment(sketch, "E138.right", {"start": v(-130.82, 40.2) * mm, "end": v(-130.82, 58.4) * mm});
            skSolve(sketch);
        }
        {
            var Q0;
            {var subQ11=sQuery(id+"F6.wireOp",EDGE,"E135.bottom");Q0=makeQuery(id+"F6.imprint","IMPRINT",FACE,{"disambiguationData":[TD([[makeQuery(id+"F6.imprint","IMPRINT",EDGE,{"derivedFrom":subQ11}),-1.0]])]});}
            var Q1;
            {var subQ5=sQuery(id+"F6.wireOp",EDGE,"E136.right");Q1=makeQuery(id+"F6.imprint","IMPRINT",FACE,{"disambiguationData":[TD([[makeQuery(id+"F6.imprint","IMPRINT",EDGE,{"derivedFrom":subQ5}),-1.0]])]});}
            var Q2;
            {var subQ5=sQuery(id+"F6.wireOp",EDGE,"E137.left");Q2=makeQuery(id+"F6.imprint","IMPRINT",FACE,{"disambiguationData":[TD([[makeQuery(id+"F6.imprint","IMPRINT",EDGE,{"derivedFrom":subQ5}),1.0]])]});}
            var Q3;
            {var subQ0=sQuery(id+"F6.wireOp",EDGE,"E137.bottom");Q3=makeQuery(id+"F6.imprint","IMPRINT",FACE,{"disambiguationData":[TD([[makeQuery(id+"F6.imprint","IMPRINT",EDGE,{"derivedFrom":subQ0}),-1.0]])]});}
            var Q4;
            {var subQ2=sQuery(id+"F6.wireOp",EDGE,"E135.top");Q4=makeQuery(id+"F6.imprint","IMPRINT",FACE,{"disambiguationData":[TD([[makeQuery(id+"F6.imprint","IMPRINT",EDGE,{"derivedFrom":subQ2}),1.0]])]});}
            var Q5;
            {var subQ0=sQuery(id+"F6.wireOp",EDGE,"E136.bottom");Q5=makeQuery(id+"F6.imprint","IMPRINT",FACE,{"disambiguationData":[TD([[makeQuery(id+"F6.imprint","IMPRINT",EDGE,{"derivedFrom":subQ0}),-1.0]])]});}
            extrude(context, id + "F7", {"entities" : qUnion([Q0, Q1, Q2, Q3, Q4, Q5]), "depth" : 1 * mm});
        }
        {
            var Q0;
            {var subQ5=sQuery(id+"F6.wireOp",EDGE,"E137.right");Q0=makeQuery(id+"F6.imprint","IMPRINT",FACE,{"disambiguationData":[TD([[makeQuery(id+"F6.imprint","IMPRINT",EDGE,{"derivedFrom":subQ5}),-1.0]])]});}
            var Q1;
            {var subQ5=sQuery(id+"F6.wireOp",EDGE,"E137.left");Q1=makeQuery(id+"F6.imprint","IMPRINT",FACE,{"disambiguationData":[TD([[makeQuery(id+"F6.imprint","IMPRINT",EDGE,{"derivedFrom":subQ5}),1.0]])]});}
            var Q2;
            {var subQ5=sQuery(id+"F6.wireOp",EDGE,"E136.right");Q2=makeQuery(id+"F6.imprint","IMPRINT",FACE,{"disambiguationData":[TD([[makeQuery(id+"F6.imprint","IMPRINT",EDGE,{"derivedFrom":subQ5}),-1.0]])]});}
            var Q3;
            {var subQ5=sQuery(id+"F6.wireOp",EDGE,"E136.left");Q3=makeQuery(id+"F6.imprint","IMPRINT",FACE,{"disambiguationData":[TD([[makeQuery(id+"F6.imprint","IMPRINT",EDGE,{"derivedFrom":subQ5}),1.0]])]});}
            extrude(context, id + "F8", {"entities" : qUnion([Q0, Q1, Q2, Q3]), "operationType" : NewBodyOperationType.ADD, "oppositeDirection" : true, "depth" : 4 * mm});
        }
        {
            var Q0;
            Q0=makeQuery(id+"F7.opExtrude","CAP_FACE",FACE,{"disambiguationData":[OSD([sQuery(id+"F6.wireOp",EDGE,"E135.bottom"),sQuery(id+"F6.wireOp",EDGE,"E135.top"),sQuery(id+"F6.wireOp",EDGE,"E135.left"),sQuery(id+"F6.wireOp",EDGE,"E135.right"),sQuery(id+"F6.wireOp",EDGE,"E136.left"),sQuery(id+"F6.wireOp",EDGE,"E137.right"),sQuery(id+"F6.wireOp",EDGE,"E138.bottom"),sQuery(id+"F6.wireOp",EDGE,"E138.top"),sQuery(id+"F6.wireOp",EDGE,"E138.left"),sQuery(id+"F6.wireOp",EDGE,"E138.right")])],"isStart":false});
            var sketch = newSketch(context, id + "F9", { "sketchPlane" : qUnion([Q0])});
            skPoint(sketch, "E139.0", {"position": v(-121.72, 49.3) * mm});
            skLineSegment(sketch, "E140.bottom", {"start": v(-112.62, 40.2) * mm, "end": v(-130.82, 40.2) * mm});
            skLineSegment(sketch, "E140.top", {"start": v(-112.62, 58.4) * mm, "end": v(-130.82, 58.4) * mm});
            skLineSegment(sketch, "E140.left", {"start": v(-112.62, 40.2) * mm, "end": v(-112.62, 58.4) * mm});
            skLineSegment(sketch, "E140.right", {"start": v(-130.82, 40.2) * mm, "end": v(-130.82, 58.4) * mm});
            skLineSegment(sketch, "E141.0", {"start": v(-131.82, 39.2) * mm, "end": v(-131.82, 59.4) * mm});
            skLineSegment(sketch, "E141.1", {"start": v(-111.62, 39.2) * mm, "end": v(-131.82, 39.2) * mm});
            skLineSegment(sketch, "E141.2", {"start": v(-111.62, 39.2) * mm, "end": v(-111.62, 59.4) * mm});
            skLineSegment(sketch, "E141.3", {"start": v(-111.62, 59.4) * mm, "end": v(-131.82, 59.4) * mm});
            skSolve(sketch);
        }
        {
            var Q0;
            Q0=makeQuery(id+"F9.imprint","IMPRINT",FACE,{"disambiguationData":[TD([[makeQuery(id+"F9.imprint","IMPRINT",EDGE,{"derivedFrom":sQuery(id+"F9.wireOp",EDGE,"E140.bottom")}),1.0]])]});
            extrude(context, id + "F10", {"entities" : qUnion([Q0]), "operationType" : NewBodyOperationType.ADD, "depth" : 5 * mm});
        }
        {
            var Q0;
            Q0=makeQuery(id+"F10.opExtrude","CAP_FACE",FACE,{"disambiguationData":[OSD([sQuery(id+"F9.wireOp",EDGE,"E140.bottom"),sQuery(id+"F9.wireOp",EDGE,"E140.top"),sQuery(id+"F9.wireOp",EDGE,"E140.left"),sQuery(id+"F9.wireOp",EDGE,"E140.right"),sQuery(id+"F9.wireOp",EDGE,"E141.0"),sQuery(id+"F9.wireOp",EDGE,"E141.1"),sQuery(id+"F9.wireOp",EDGE,"E141.2"),sQuery(id+"F9.wireOp",EDGE,"E141.3")])],"isStart":false});
            var sketch = newSketch(context, id + "F11", { "sketchPlane" : qUnion([Q0])});
            skPoint(sketch, "E142.0", {"position": v(-121.72, 49.3) * mm});
            skLineSegment(sketch, "E143.bottom", {"start": v(-112.62, 48.8) * mm, "end": v(-130.82, 48.8) * mm});
            skLineSegment(sketch, "E143.top", {"start": v(-112.62, 49.8) * mm, "end": v(-130.82, 49.8) * mm});
            skLineSegment(sketch, "E143.left", {"start": v(-112.62, 48.8) * mm, "end": v(-112.62, 49.8) * mm});
            skLineSegment(sketch, "E143.right", {"start": v(-130.82, 48.8) * mm, "end": v(-130.82, 49.8) * mm});
            skLineSegment(sketch, "E144.bottom", {"start": v(-121.22, 40.2) * mm, "end": v(-122.22, 40.2) * mm});
            skLineSegment(sketch, "E144.top", {"start": v(-121.22, 58.4) * mm, "end": v(-122.22, 58.4) * mm});
            skLineSegment(sketch, "E144.left", {"start": v(-121.22, 40.2) * mm, "end": v(-121.22, 58.4) * mm});
            skLineSegment(sketch, "E144.right", {"start": v(-122.22, 40.2) * mm, "end": v(-122.22, 58.4) * mm});
            skSolve(sketch);
        }
        {
            var Q0;
            Q0=makeQuery(id+"FvrxBWBR3NFs59h_1.boolean.opBoolean","MERGE",FACE,{"derivedFrom":[makeQuery(id+"F5.boolean.opBoolean","COPY",FACE,{"derivedFrom":makeQuery(id+"F5.opExtrude","CAP_FACE",FACE,{"disambiguationData":[OSD([sQuery(id+"F4.wireOp",EDGE,"E114.bottom"),sQuery(id+"F4.wireOp",EDGE,"E114.top"),sQuery(id+"F4.wireOp",EDGE,"E114.left"),sQuery(id+"F4.wireOp",EDGE,"E114.right")])],"isStart":false})}),makeQuery(id+"FvrxBWBR3NFs59h_1.opExtrude","CAP_FACE",FACE,{"disambiguationData":[OSD([sQuery(id+"FOyiDT4y5zkIJA3_1.wireOp",EDGE,"oN5qgFBu-MPa5-jxRP-8K83-Y7W6XuHjnRPn.bottom"),sQuery(id+"FOyiDT4y5zkIJA3_1.wireOp",EDGE,"oN5qgFBu-MPa5-jxRP-8K83-Y7W6XuHjnRPn.top"),sQuery(id+"FOyiDT4y5zkIJA3_1.wireOp",EDGE,"oN5qgFBu-MPa5-jxRP-8K83-Y7W6XuHjnRPn.left"),sQuery(id+"FOyiDT4y5zkIJA3_1.wireOp",EDGE,"oN5qgFBu-MPa5-jxRP-8K83-Y7W6XuHjnRPn.right")])],"isStart":false}),makeQuery(id+"FvrxBWBR3NFs59h_1.opExtrude","CAP_FACE",FACE,{"disambiguationData":[OSD([sQuery(id+"FOyiDT4y5zkIJA3_1.wireOp",EDGE,"if443p5T-YKs4-1gVt-ORIe-qeo7ftMrQxsQ.bottom"),sQuery(id+"FOyiDT4y5zkIJA3_1.wireOp",EDGE,"if443p5T-YKs4-1gVt-ORIe-qeo7ftMrQxsQ.top"),sQuery(id+"FOyiDT4y5zkIJA3_1.wireOp",EDGE,"if443p5T-YKs4-1gVt-ORIe-qeo7ftMrQxsQ.left"),sQuery(id+"FOyiDT4y5zkIJA3_1.wireOp",EDGE,"if443p5T-YKs4-1gVt-ORIe-qeo7ftMrQxsQ.right")])],"isStart":false})]});
            var sketch = newSketch(context, id + "F12", { "sketchPlane" : qUnion([Q0])});
            skPoint(sketch, "E145.0", {"position": v(-109.5, 1.96) * mm});
            skLineSegment(sketch, "E146.bottom", {"start": v(-106.5, -1.04) * mm, "end": v(-112.5, -1.04) * mm});
            skLineSegment(sketch, "E146.top", {"start": v(-106.5, 4.96) * mm, "end": v(-112.5, 4.96) * mm});
            skLineSegment(sketch, "E146.left", {"start": v(-106.5, -1.04) * mm, "end": v(-106.5, 4.96) * mm});
            skLineSegment(sketch, "E146.right", {"start": v(-112.5, -1.04) * mm, "end": v(-112.5, 4.96) * mm});
            skLineSegment(sketch, "E147.bottom", {"start": v(-129, -1.04) * mm, "end": v(-135, -1.04) * mm});
            skLineSegment(sketch, "E147.top", {"start": v(-129, 4.96) * mm, "end": v(-135, 4.96) * mm});
            skLineSegment(sketch, "E147.left", {"start": v(-129, -1.04) * mm, "end": v(-129, 4.96) * mm});
            skLineSegment(sketch, "E147.right", {"start": v(-135, -1.04) * mm, "end": v(-135, 4.96) * mm});
            skPoint(sketch, "E147.middle", {"position": v(-132, 1.96) * mm});
            skSolve(sketch);
        }
        {
            var Q0;
            Q0=qSketchRegion(id+"F11",true);
            extrude(context, id + "F13", {"entities" : qUnion([Q0]), "operationType" : NewBodyOperationType.ADD, "oppositeDirection" : true, "depth" : 6 * mm});
        }
        {
            var Q0;
            Q0=makeQuery(id+"F13.boolean.opBoolean","MERGE",FACE,{"derivedFrom":[makeQuery(id+"F10.opExtrude","CAP_FACE",FACE,{"disambiguationData":[OSD([sQuery(id+"F9.wireOp",EDGE,"E140.bottom"),sQuery(id+"F9.wireOp",EDGE,"E140.top"),sQuery(id+"F9.wireOp",EDGE,"E140.left"),sQuery(id+"F9.wireOp",EDGE,"E140.right"),sQuery(id+"F9.wireOp",EDGE,"E141.0"),sQuery(id+"F9.wireOp",EDGE,"E141.1"),sQuery(id+"F9.wireOp",EDGE,"E141.2"),sQuery(id+"F9.wireOp",EDGE,"E141.3")])],"isStart":false}),makeQuery(id+"F13.opExtrude","CAP_FACE",FACE,{"disambiguationData":[OSD([sQuery(id+"F11.wireOp",EDGE,"E143.bottom"),sQuery(id+"F11.wireOp",EDGE,"E143.top"),sQuery(id+"F11.wireOp",EDGE,"E143.left"),sQuery(id+"F11.wireOp",EDGE,"E143.right"),sQuery(id+"F11.wireOp",EDGE,"E144.bottom"),sQuery(id+"F11.wireOp",EDGE,"E144.top"),sQuery(id+"F11.wireOp",EDGE,"E144.left"),sQuery(id+"F11.wireOp",EDGE,"E144.right")])],"isStart":true})]});
            var sketch = newSketch(context, id + "F14", { "sketchPlane" : qUnion([Q0])});
            skPoint(sketch, "E148.0", {"position": v(-130.82, 58.4) * mm});
            skPoint(sketch, "E148.1", {"position": v(-112.62, 40.2) * mm});
            skLineSegment(sketch, "E149.bottom", {"start": v(-130.82, 58.4) * mm, "end": v(-112.62, 58.4) * mm});
            skLineSegment(sketch, "E149.top", {"start": v(-130.82, 40.2) * mm, "end": v(-112.62, 40.2) * mm});
            skLineSegment(sketch, "E149.left", {"start": v(-130.82, 58.4) * mm, "end": v(-130.82, 40.2) * mm});
            skLineSegment(sketch, "E149.right", {"start": v(-112.62, 58.4) * mm, "end": v(-112.62, 40.2) * mm});
            skSolve(sketch);
        }
        {
            var Q0;
            Q0=qSketchRegion(id+"F14",true);
            extrude(context, id + "F15", {"entities" : qUnion([Q0]), "operationType" : NewBodyOperationType.REMOVE, "oppositeDirection" : true, "depth" : 1 * mm});
        }
        {
            var Q0;
            {var subQ0=sQuery(id+"F6.wireOp",EDGE,"E137.right");var subQ2=sQuery(id+"F6.wireOp",EDGE,"E138.right");var subQ4=sQuery(id+"F6.wireOp",EDGE,"E136.left");var subQ6=sQuery(id+"F6.wireOp",EDGE,"E138.left");var subQ8=sQuery(id+"F6.wireOp",EDGE,"E135.top");var subQ9=sQuery(id+"F6.wireOp",EDGE,"E135.left");var subQ11=sQuery(id+"F6.wireOp",EDGE,"E135.right");var subQ13=sQuery(id+"F6.wireOp",EDGE,"E138.top");var subQ16=sQuery(id+"F6.wireOp",EDGE,"E138.bottom");var subQ17=sQuery(id+"F6.wireOp",EDGE,"E135.bottom");var subQ18=makeQuery(id+"F7.opExtrude","CAP_FACE",FACE,{"disambiguationData":[OSD([subQ17,subQ8,subQ9,subQ11,subQ4,subQ0,subQ16,subQ13,subQ6,subQ2])],"isStart":true});Q0=makeQuery(id+"F13.boolean.opBoolean","MERGE",FACE,{"derivedFrom":[makeQuery(id+"F8.boolean.opBoolean","SPLIT",FACE,{"disambiguationData":[TD([makeQuery(id+"F7.opExtrude","SWEPT_FACE",FACE,{"disambiguationData":[OSD([subQ17])]})])],"derivedFrom":subQ18}),makeQuery(id+"F8.boolean.opBoolean","SPLIT",FACE,{"disambiguationData":[TD([makeQuery(id+"F7.opExtrude","SWEPT_FACE",FACE,{"disambiguationData":[OSD([subQ8])]})])],"derivedFrom":subQ18}),makeQuery(id+"F13.opExtrude","CAP_FACE",FACE,{"disambiguationData":[OSD([sQuery(id+"F11.wireOp",EDGE,"E143.bottom"),sQuery(id+"F11.wireOp",EDGE,"E143.top"),sQuery(id+"F11.wireOp",EDGE,"E143.left"),sQuery(id+"F11.wireOp",EDGE,"E143.right"),sQuery(id+"F11.wireOp",EDGE,"E144.bottom"),sQuery(id+"F11.wireOp",EDGE,"E144.top"),sQuery(id+"F11.wireOp",EDGE,"E144.left"),sQuery(id+"F11.wireOp",EDGE,"E144.right")])],"isStart":false})]});}
            var sketch = newSketch(context, id + "F16", { "sketchPlane" : qUnion([Q0])});
            skPoint(sketch, "E150.0", {"position": v(-121.72, -40.2) * mm});
            skLineSegment(sketch, "E151.bottom", {"start": v(-120.47, -50.3) * mm, "end": v(-122.97, -50.3) * mm});
            skLineSegment(sketch, "E151.top", {"start": v(-120.47, -48.3) * mm, "end": v(-122.97, -48.3) * mm});
            skLineSegment(sketch, "E151.left", {"start": v(-120.47, -50.3) * mm, "end": v(-120.47, -48.3) * mm});
            skLineSegment(sketch, "E151.right", {"start": v(-122.97, -50.3) * mm, "end": v(-122.97, -48.3) * mm});
            skPoint(sketch, "E151.middle", {"position": v(-121.72, -49.3) * mm});
            skPoint(sketch, "E151.middle.positionSnap0", {"position": v(-130.82, -49.3) * mm});
            skPoint(sketch, "E151.centerSnap0", {"position": v(-130.82, -49.3) * mm});
            skSolve(sketch);
        }
        {
            var Q0;
            Q0=makeQuery(id+"FOl8yoey8HPPjfu_3.opExtrude","CAP_FACE",FACE,{"disambiguationData":[OSD([sQuery(id+"F12.wireOp",EDGE,"E146.bottom"),sQuery(id+"F12.wireOp",EDGE,"E146.top"),sQuery(id+"F12.wireOp",EDGE,"E146.left"),sQuery(id+"F12.wireOp",EDGE,"E146.right")])],"isStart":false});
            var sketch = newSketch(context, id + "F17", { "sketchPlane" : qUnion([Q0])});
            skPoint(sketch, "E152.0", {"position": v(-111.5, 3.96) * mm});
            skLineSegment(sketch, "E153.bottom", {"start": v(-108.5, 0.7) * mm, "end": v(-110.5, 0.7) * mm});
            skLineSegment(sketch, "E153.top", {"start": v(-108.5, 3.2) * mm, "end": v(-110.5, 3.2) * mm});
            skLineSegment(sketch, "E153.left", {"start": v(-108.5, 0.7) * mm, "end": v(-108.5, 3.2) * mm});
            skLineSegment(sketch, "E153.right", {"start": v(-110.5, 0.7) * mm, "end": v(-110.5, 3.2) * mm});
            skPoint(sketch, "E153.middle", {"position": v(-109.5, 1.96) * mm});
            skPoint(sketch, "E154.1", {"position": v(-132, 4.96) * mm});
            skPoint(sketch, "E155.0", {"position": v(-135, 1.96) * mm});
            skLineSegment(sketch, "E156.bottom", {"start": v(-131, 0.7) * mm, "end": v(-133, 0.7) * mm});
            skLineSegment(sketch, "E156.top", {"start": v(-131, 3.2) * mm, "end": v(-133, 3.2) * mm});
            skLineSegment(sketch, "E156.left", {"start": v(-131, 0.7) * mm, "end": v(-131, 3.2) * mm});
            skLineSegment(sketch, "E156.right", {"start": v(-133, 0.7) * mm, "end": v(-133, 3.2) * mm});
            skPoint(sketch, "E156.middle", {"position": v(-132, 1.96) * mm});
            skSolve(sketch);
        }
        {
            var Q0;
            {var subQ0=sQuery(id+"F11.wireOp",EDGE,"E143.right");var subQ1=sQuery(id+"F11.wireOp",EDGE,"E143.bottom");var subQ4=sQuery(id+"F11.wireOp",EDGE,"E144.right");var subQ5=sQuery(id+"F6.wireOp",EDGE,"E138.right");var subQ8=sQuery(id+"F11.wireOp",EDGE,"E143.top");var subQ9=sQuery(id+"F6.wireOp",EDGE,"E137.right");var subQ11=sQuery(id+"F6.wireOp",EDGE,"E136.left");var subQ13=sQuery(id+"F6.wireOp",EDGE,"E138.left");var subQ15=sQuery(id+"F6.wireOp",EDGE,"E135.top");var subQ16=sQuery(id+"F6.wireOp",EDGE,"E135.left");var subQ18=sQuery(id+"F6.wireOp",EDGE,"E135.right");var subQ20=sQuery(id+"F6.wireOp",EDGE,"E138.top");var subQ22=sQuery(id+"F6.wireOp",EDGE,"E138.bottom");var subQ23=sQuery(id+"F6.wireOp",EDGE,"E135.bottom");var subQ24=makeQuery(id+"F7.opExtrude","CAP_FACE",FACE,{"disambiguationData":[OSD([subQ23,subQ15,subQ16,subQ18,subQ11,subQ9,subQ22,subQ20,subQ13,subQ5])],"isStart":true});Q0=makeQuery(id+"F20.boolean.opBoolean","SPLIT",FACE,{"disambiguationData":[TD([makeQuery(id+"F20.opExtrude","SWEPT_FACE",FACE,{"disambiguationData":[OSD([sQuery(id+"F16.wireOp",EDGE,"E151.right")])]})])],"derivedFrom":makeQuery(id+"F13.boolean.opBoolean","MERGE",FACE,{"derivedFrom":[makeQuery(id+"F8.boolean.opBoolean","SPLIT",FACE,{"disambiguationData":[TD([makeQuery(id+"F7.opExtrude","SWEPT_FACE",FACE,{"disambiguationData":[OSD([subQ23])]})])],"derivedFrom":subQ24}),makeQuery(id+"F8.boolean.opBoolean","SPLIT",FACE,{"disambiguationData":[TD([makeQuery(id+"F7.opExtrude","SWEPT_FACE",FACE,{"disambiguationData":[OSD([subQ15])]})])],"derivedFrom":subQ24}),makeQuery(id+"F13.opExtrude","CAP_FACE",FACE,{"disambiguationData":[OSD([subQ1,subQ8,sQuery(id+"F11.wireOp",EDGE,"E143.left"),subQ0,sQuery(id+"F11.wireOp",EDGE,"E144.bottom"),sQuery(id+"F11.wireOp",EDGE,"E144.top"),sQuery(id+"F11.wireOp",EDGE,"E144.left"),subQ4])],"isStart":false})]})});}
            var sketch = newSketch(context, id + "F18", { "sketchPlane" : qUnion([Q0])});
            skPoint(sketch, "E157.0", {"position": v(-126.52, -48.8) * mm});
            skPoint(sketch, "E158.0", {"position": v(-122.22, -44.5) * mm});
            skPoint(sketch, "E159.0", {"position": v(-122.22, -40.2) * mm});
            skLineSegment(sketch, "E160.bottom", {"start": v(-122.22, -40.2) * mm, "end": v(-130.82, -40.2) * mm});
            skLineSegment(sketch, "E160.top", {"start": v(-122.22, -48.8) * mm, "end": v(-130.82, -48.8) * mm});
            skLineSegment(sketch, "E160.left", {"start": v(-122.22, -40.2) * mm, "end": v(-122.22, -48.8) * mm});
            skLineSegment(sketch, "E160.right", {"start": v(-130.82, -40.2) * mm, "end": v(-130.82, -48.8) * mm});
            skPoint(sketch, "E160.middle", {"position": v(-126.52, -44.5) * mm});
            skLineSegment(sketch, "E161.bottom", {"start": v(-122.72, -40.7) * mm, "end": v(-130.32, -40.7) * mm});
            skLineSegment(sketch, "E161.top", {"start": v(-122.72, -48.3) * mm, "end": v(-130.32, -48.3) * mm});
            skLineSegment(sketch, "E161.left", {"start": v(-122.72, -40.7) * mm, "end": v(-122.72, -48.3) * mm});
            skLineSegment(sketch, "E161.right", {"start": v(-130.32, -40.7) * mm, "end": v(-130.32, -48.3) * mm});
            skLineSegment(sketch, "E162.direction1", {"start": v(-130.82, -48.8) * mm, "end": v(-121.22, -48.8) * mm, "construction": true});
            skLineSegment(sketch, "E163.0.1.0", {"start": v(-113.12, -40.7) * mm, "end": v(-120.72, -40.7) * mm});
            skLineSegment(sketch, "E163.3.1.0", {"start": v(-112.62, -40.2) * mm, "end": v(-121.22, -40.2) * mm});
            skLineSegment(sketch, "E163.6.1.0", {"start": v(-112.62, -48.8) * mm, "end": v(-121.22, -48.8) * mm});
            skLineSegment(sketch, "E163.9.1.0", {"start": v(-112.62, -40.2) * mm, "end": v(-112.62, -48.8) * mm});
            skPoint(sketch, "E163.12.1.0", {"position": v(-116.92, -44.5) * mm});
            skLineSegment(sketch, "E163.13.1.0", {"start": v(-113.12, -40.7) * mm, "end": v(-113.12, -48.3) * mm});
            skLineSegment(sketch, "E163.16.1.0", {"start": v(-120.72, -40.7) * mm, "end": v(-120.72, -48.3) * mm});
            skLineSegment(sketch, "E163.19.1.0", {"start": v(-121.22, -40.2) * mm, "end": v(-121.22, -48.8) * mm});
            skPoint(sketch, "E163.22.1.0", {"position": v(-112.62, -44.5) * mm});
            skPoint(sketch, "E163.23.1.0", {"position": v(-112.62, -40.2) * mm});
            skLineSegment(sketch, "E163.24.1.0", {"start": v(-113.12, -48.3) * mm, "end": v(-120.72, -48.3) * mm});
            skPoint(sketch, "E163.27.1.0", {"position": v(-116.92, -48.8) * mm});
            skPoint(sketch, "E163.28.1.0", {"position": v(-116.92, -44.5) * mm});
            skSolve(sketch);
        }
        {
            var Q0;
            Q0=qSketchRegion(id+"F18",true);
            extrude(context, id + "F19", {"entities" : qUnion([Q0]), "operationType" : NewBodyOperationType.ADD, "oppositeDirection" : true, "depth" : 2 * mm});
        }
        {
            var Q0;
            Q0=qSketchRegion(id+"F16",true);
            extrude(context, id + "F20", {"entities" : qUnion([Q0]), "operationType" : NewBodyOperationType.REMOVE, "oppositeDirection" : true, "depth" : 2 * mm});
        }
        {
            var Q0;
            Q0=makeQuery(id+"F0.imprint","IMPRINT",FACE,{"disambiguationData":[TD([[makeQuery(id+"F0.imprint","IMPRINT",EDGE,{"derivedFrom":sQuery(id+"F0.wireOp",EDGE,"E0.bottom")}),-1.0]])]});
            var sketch = newSketch(context, id + "F21", { "sketchPlane" : qUnion([Q0])});
            skLineSegment(sketch, "E164.top", {"start": v(-139.5, -33.04) * mm, "end": v(-43.5, -33.04) * mm});
            skLineSegment(sketch, "E164.left", {"start": v(-139.5, -55.04) * mm, "end": v(-139.5, -33.04) * mm});
            skLineSegment(sketch, "E165.top", {"start": v(-25.5, -11.04) * mm, "end": v(-43.5, -11.04) * mm});
            skLineSegment(sketch, "E165.right", {"start": v(-43.5, -33.04) * mm, "end": v(-43.5, -11.04) * mm});
            skLineSegment(sketch, "E166.top", {"start": v(-9.5, 11.96) * mm, "end": v(-25.5, 11.96) * mm});
            skLineSegment(sketch, "E166.right", {"start": v(-25.5, -11.04) * mm, "end": v(-25.5, 11.96) * mm});
            skLineSegment(sketch, "E167", {"start": v(-9.5, 11.96) * mm, "end": v(-9.5, -55.04) * mm});
            skLineSegment(sketch, "E168", {"start": v(-139.5, -55.04) * mm, "end": v(-9.5, -55.04) * mm});
            skLineSegment(sketch, "E169.bottom", {"start": v(-43.5, -33.04) * mm, "end": v(-9.5, -33.04) * mm});
            skLineSegment(sketch, "E169.top", {"start": v(-43.5, -31.04) * mm, "end": v(-9.5, -31.04) * mm});
            skLineSegment(sketch, "E169.left", {"start": v(-43.5, -33.04) * mm, "end": v(-43.5, -31.04) * mm});
            skLineSegment(sketch, "E169.right", {"start": v(-9.5, -33.04) * mm, "end": v(-9.5, -31.04) * mm});
            skLineSegment(sketch, "E170.bottom", {"start": v(-25.5, -11.04) * mm, "end": v(-9.5, -11.04) * mm});
            skLineSegment(sketch, "E170.top", {"start": v(-25.5, -9.04) * mm, "end": v(-9.5, -9.04) * mm});
            skLineSegment(sketch, "E170.left", {"start": v(-25.5, -11.04) * mm, "end": v(-25.5, -9.04) * mm});
            skLineSegment(sketch, "E170.right", {"start": v(-9.5, -11.04) * mm, "end": v(-9.5, -9.04) * mm});
            skLineSegment(sketch, "E171", {"start": v(-25.5, -11.04) * mm, "end": v(-25.5, -31.04) * mm});
            skSolve(sketch);
        }
        {
            var Q0;
            Q0=makeQuery(id+"F21.imprint","IMPRINT",FACE,{"disambiguationData":[TD([[makeQuery(id+"F21.imprint","IMPRINT",EDGE,{"derivedFrom":makeQuery(id+"F0.imprint","IMPRINT",EDGE,{"derivedFrom":sQuery(id+"F0.wireOp",EDGE,"6XQCNLW2-68Wz-nC9p-wT4x-b90YEvEmSNLj")})}),1.0]])]});
            var Q1;
            Q1=makeQuery(id+"F21.imprint","IMPRINT",FACE,{"disambiguationData":[TD([[makeQuery(id+"F21.imprint","IMPRINT",EDGE,{"derivedFrom":makeQuery(id+"F0.imprint","IMPRINT",EDGE,{"derivedFrom":sQuery(id+"F0.wireOp",EDGE,"E3")})}),1.0]])]});
            var Q2;
            Q2=makeQuery(id+"F21.imprint","IMPRINT",FACE,{"disambiguationData":[TD([[makeQuery(id+"F21.imprint","IMPRINT",EDGE,{"derivedFrom":makeQuery(id+"F0.imprint","IMPRINT",EDGE,{"derivedFrom":sQuery(id+"F0.wireOp",EDGE,"E4")})}),1.0]])]});
            var Q3;
            Q3=makeQuery(id+"F21.imprint","IMPRINT",FACE,{"disambiguationData":[TD([[makeQuery(id+"F21.imprint","IMPRINT",EDGE,{"derivedFrom":makeQuery(id+"F0.imprint","IMPRINT",EDGE,{"derivedFrom":sQuery(id+"F0.wireOp",EDGE,"E7")})}),1.0]])]});
            var Q4;
            Q4=makeQuery(id+"F21.imprint","IMPRINT",FACE,{"disambiguationData":[TD([[makeQuery(id+"F21.imprint","IMPRINT",EDGE,{"derivedFrom":makeQuery(id+"F0.imprint","IMPRINT",EDGE,{"derivedFrom":sQuery(id+"F0.wireOp",EDGE,"E8")})}),1.0]])]});
            var Q5;
            Q5=makeQuery(id+"F21.imprint","IMPRINT",FACE,{"disambiguationData":[TD([[makeQuery(id+"F21.imprint","IMPRINT",EDGE,{"derivedFrom":makeQuery(id+"F0.imprint","IMPRINT",EDGE,{"derivedFrom":sQuery(id+"F0.wireOp",EDGE,"E9")})}),1.0]])]});
            var Q6;
            Q6=makeQuery(id+"F21.imprint","IMPRINT",FACE,{"disambiguationData":[TD([[makeQuery(id+"F21.imprint","IMPRINT",EDGE,{"derivedFrom":makeQuery(id+"F0.imprint","IMPRINT",EDGE,{"derivedFrom":sQuery(id+"F0.wireOp",EDGE,"E10")})}),1.0]])]});
            var Q7;
            Q7=makeQuery(id+"F21.imprint","IMPRINT",FACE,{"disambiguationData":[TD([[makeQuery(id+"F21.imprint","IMPRINT",EDGE,{"derivedFrom":makeQuery(id+"F0.imprint","IMPRINT",EDGE,{"derivedFrom":sQuery(id+"F0.wireOp",EDGE,"E11")})}),1.0]])]});
            var Q8;
            Q8=makeQuery(id+"F21.imprint","IMPRINT",FACE,{"disambiguationData":[TD([[makeQuery(id+"F21.imprint","IMPRINT",EDGE,{"derivedFrom":makeQuery(id+"F0.imprint","IMPRINT",EDGE,{"derivedFrom":sQuery(id+"F0.wireOp",EDGE,"E12")})}),1.0]])]});
            var Q9;
            Q9=makeQuery(id+"F21.imprint","IMPRINT",FACE,{"disambiguationData":[TD([[makeQuery(id+"F21.imprint","IMPRINT",EDGE,{"derivedFrom":makeQuery(id+"F0.imprint","IMPRINT",EDGE,{"derivedFrom":sQuery(id+"F0.wireOp",EDGE,"E13")})}),1.0]])]});
            var Q10;
            Q10=makeQuery(id+"F21.imprint","IMPRINT",FACE,{"disambiguationData":[TD([[makeQuery(id+"F21.imprint","IMPRINT",EDGE,{"derivedFrom":makeQuery(id+"F0.imprint","IMPRINT",EDGE,{"derivedFrom":sQuery(id+"F0.wireOp",EDGE,"E15")})}),1.0]])]});
            var Q11;
            Q11=makeQuery(id+"F21.imprint","IMPRINT",FACE,{"disambiguationData":[TD([[makeQuery(id+"F21.imprint","IMPRINT",EDGE,{"derivedFrom":makeQuery(id+"F0.imprint","IMPRINT",EDGE,{"derivedFrom":sQuery(id+"F0.wireOp",EDGE,"E16")})}),1.0]])]});
            var Q12;
            {var subQ1=sQuery(id+"F21.wireOp",EDGE,"E166.top");Q12=makeQuery(id+"F21.imprint","IMPRINT",FACE,{"disambiguationData":[TD([[makeQuery(id+"F21.imprint","IMPRINT",EDGE,{"derivedFrom":subQ1}),1.0]])]});}
            var Q13;
            Q13=makeQuery(id+"F21.imprint","IMPRINT",FACE,{"disambiguationData":[TD([[makeQuery(id+"F21.imprint","IMPRINT",EDGE,{"derivedFrom":sQuery(id+"F21.wireOp",EDGE,"E165.top")}),1.0]])]});
            var Q14;
            Q14=makeQuery(id+"F21.imprint","IMPRINT",FACE,{"disambiguationData":[TD([[makeQuery(id+"F21.imprint","IMPRINT",EDGE,{"derivedFrom":sQuery(id+"F21.wireOp",EDGE,"E164.top")}),-1.0]])]});
            extrude(context, id + "F22", {"entities" : qUnion([Q0, Q1, Q2, Q3, Q4, Q5, Q6, Q7, Q8, Q9, Q10, Q11, Q12, Q13, Q14]), "operationType" : NewBodyOperationType.REMOVE, "depth" : 5 * mm});
        }
        {
            var Q0;
            Q0=makeQuery(id+"F1.imprint","IMPRINT",FACE,{"disambiguationData":[TD([[makeQuery(id+"F1.imprint","IMPRINT",EDGE,{"derivedFrom":sQuery(id+"F1.wireOp",EDGE,"E73.bottom")}),-1.0]])]});
            var Q1;
            {var subQ0=sQuery(id+"F1.wireOp",EDGE,"564e7f7f-852e-44c8-adaa-80bbbea6a7a0.right");var subQ1=sQuery(id+"F1.wireOp",EDGE,"564e7f7f-852e-44c8-adaa-80bbbea6a7a0.top");var subQ2=makeQuery(id+"F1.imprint","INTERSECT",VERTEX,{"derivedFrom":[subQ1,subQ0]});Q1=makeQuery(id+"F1.imprint","IMPRINT",FACE,{"disambiguationData":[TD([[makeQuery(id+"F1.imprint","IMPRINT",EDGE,{"disambiguationData":[TD([[subQ2,1.0]])],"derivedFrom":subQ1}),1.0]])]});}
            var Q2;
            {var subQ0=sQuery(id+"F1.wireOp",EDGE,"564e7f7f-852e-44c8-adaa-80bbbea6a7a0.left");var subQ1=sQuery(id+"F1.wireOp",EDGE,"564e7f7f-852e-44c8-adaa-80bbbea6a7a0.top");var subQ2=makeQuery(id+"F1.imprint","INTERSECT",VERTEX,{"derivedFrom":[subQ1,subQ0]});Q2=makeQuery(id+"F1.imprint","IMPRINT",FACE,{"disambiguationData":[TD([[makeQuery(id+"F1.imprint","IMPRINT",EDGE,{"disambiguationData":[TD([[subQ2,-1.0]])],"derivedFrom":subQ1}),1.0]])]});}
            var Q3;
            {var subQ0=sQuery(id+"F1.wireOp",EDGE,"564e7f7f-852e-44c8-adaa-80bbbea6a7a0.right");var subQ1=sQuery(id+"F1.wireOp",EDGE,"564e7f7f-852e-44c8-adaa-80bbbea6a7a0.bottom");var subQ2=makeQuery(id+"F1.imprint","INTERSECT",VERTEX,{"derivedFrom":[subQ1,subQ0]});Q3=makeQuery(id+"F1.imprint","IMPRINT",FACE,{"disambiguationData":[TD([[makeQuery(id+"F1.imprint","IMPRINT",EDGE,{"disambiguationData":[TD([[subQ2,1.0]])],"derivedFrom":subQ1}),-1.0]])]});}
            var Q4;
            {var subQ0=sQuery(id+"F1.wireOp",EDGE,"564e7f7f-852e-44c8-adaa-80bbbea6a7a0.left");var subQ1=sQuery(id+"F1.wireOp",EDGE,"564e7f7f-852e-44c8-adaa-80bbbea6a7a0.bottom");var subQ2=makeQuery(id+"F1.imprint","INTERSECT",VERTEX,{"derivedFrom":[subQ1,subQ0]});Q4=makeQuery(id+"F1.imprint","IMPRINT",FACE,{"disambiguationData":[TD([[makeQuery(id+"F1.imprint","IMPRINT",EDGE,{"disambiguationData":[TD([[subQ2,-1.0]])],"derivedFrom":subQ1}),-1.0]])]});}
            var Q5;
            {var subQ0=sQuery(id+"F1.wireOp",EDGE,"E91.right");var subQ1=sQuery(id+"F1.wireOp",EDGE,"E91.top");var subQ2=makeQuery(id+"F1.imprint","INTERSECT",VERTEX,{"derivedFrom":[subQ1,subQ0]});Q5=makeQuery(id+"F1.imprint","IMPRINT",FACE,{"disambiguationData":[TD([[makeQuery(id+"F1.imprint","IMPRINT",EDGE,{"disambiguationData":[TD([[subQ2,1.0]])],"derivedFrom":subQ1}),1.0]])]});}
            var Q6;
            {var subQ0=sQuery(id+"F1.wireOp",EDGE,"E91.left");var subQ1=sQuery(id+"F1.wireOp",EDGE,"E91.top");var subQ2=makeQuery(id+"F1.imprint","INTERSECT",VERTEX,{"derivedFrom":[subQ1,subQ0]});Q6=makeQuery(id+"F1.imprint","IMPRINT",FACE,{"disambiguationData":[TD([[makeQuery(id+"F1.imprint","IMPRINT",EDGE,{"disambiguationData":[TD([[subQ2,-1.0]])],"derivedFrom":subQ1}),1.0]])]});}
            var Q7;
            {var subQ0=sQuery(id+"F1.wireOp",EDGE,"E91.right");var subQ1=sQuery(id+"F1.wireOp",EDGE,"E91.bottom");var subQ2=makeQuery(id+"F1.imprint","INTERSECT",VERTEX,{"derivedFrom":[subQ1,subQ0]});Q7=makeQuery(id+"F1.imprint","IMPRINT",FACE,{"disambiguationData":[TD([[makeQuery(id+"F1.imprint","IMPRINT",EDGE,{"disambiguationData":[TD([[subQ2,1.0]])],"derivedFrom":subQ1}),-1.0]])]});}
            var Q8;
            {var subQ0=sQuery(id+"F1.wireOp",EDGE,"E91.left");var subQ1=sQuery(id+"F1.wireOp",EDGE,"E91.bottom");var subQ2=makeQuery(id+"F1.imprint","INTERSECT",VERTEX,{"derivedFrom":[subQ1,subQ0]});Q8=makeQuery(id+"F1.imprint","IMPRINT",FACE,{"disambiguationData":[TD([[makeQuery(id+"F1.imprint","IMPRINT",EDGE,{"disambiguationData":[TD([[subQ2,-1.0]])],"derivedFrom":subQ1}),-1.0]])]});}
            extrude(context, id + "F23", {"entities" : qUnion([Q0, Q1, Q2, Q3, Q4, Q5, Q6, Q7, Q8]), "depth" : 2 * mm});
        }
        {
            var Q0;
            Q0=makeQuery(id+"F3.opExtrude","CAP_FACE",FACE,{"disambiguationData":[OSD([sQuery(id+"F0.wireOp",EDGE,"E0.bottom"),sQuery(id+"F0.wireOp",EDGE,"E0.top"),sQuery(id+"F0.wireOp",EDGE,"E0.left"),sQuery(id+"F0.wireOp",EDGE,"E0.right"),sQuery(id+"F0.wireOp",EDGE,"6XQCNLW2-68Wz-nC9p-wT4x-b90YEvEmSNLj"),sQuery(id+"F0.wireOp",EDGE,"E3"),sQuery(id+"F0.wireOp",EDGE,"E4"),sQuery(id+"F0.wireOp",EDGE,"E7"),sQuery(id+"F0.wireOp",EDGE,"E8"),sQuery(id+"F0.wireOp",EDGE,"E9"),sQuery(id+"F0.wireOp",EDGE,"E10"),sQuery(id+"F0.wireOp",EDGE,"E11"),sQuery(id+"F0.wireOp",EDGE,"E12"),sQuery(id+"F0.wireOp",EDGE,"E13"),sQuery(id+"F0.wireOp",EDGE,"E14.bottom"),sQuery(id+"F0.wireOp",EDGE,"E14.top"),sQuery(id+"F0.wireOp",EDGE,"E14.left"),sQuery(id+"F0.wireOp",EDGE,"E14.right"),sQuery(id+"F0.wireOp",EDGE,"E15"),sQuery(id+"F0.wireOp",EDGE,"E16"),sQuery(id+"F0.wireOp",EDGE,"E18.bottom"),sQuery(id+"F0.wireOp",EDGE,"E18.top"),sQuery(id+"F0.wireOp",EDGE,"E18.left"),sQuery(id+"F0.wireOp",EDGE,"E18.right"),sQuery(id+"F0.wireOp",EDGE,"E20.bottom"),sQuery(id+"F0.wireOp",EDGE,"E20.top"),sQuery(id+"F0.wireOp",EDGE,"E21.left"),sQuery(id+"F0.wireOp",EDGE,"E21.right"),sQuery(id+"F0.wireOp",EDGE,"E22.left"),sQuery(id+"F0.wireOp",EDGE,"E22.right"),sQuery(id+"F0.wireOp",EDGE,"E23.trimOffspring"),sQuery(id+"F0.wireOp",EDGE,"E24.trimOffspring"),sQuery(id+"F0.wireOp",EDGE,"E25.trimOffspring"),sQuery(id+"F0.wireOp",EDGE,"E26.trimOffspring"),sQuery(id+"F0.wireOp",EDGE,"E27.trimOffspring"),sQuery(id+"F0.wireOp",EDGE,"E28.trimOffspring"),sQuery(id+"F0.wireOp",EDGE,"E29.trimOffspring"),sQuery(id+"F0.wireOp",EDGE,"E30.trimOffspring"),sQuery(id+"F0.wireOp",EDGE,"E19.bottom"),sQuery(id+"F0.wireOp",EDGE,"E19.top"),sQuery(id+"F0.wireOp",EDGE,"E19.left"),sQuery(id+"F0.wireOp",EDGE,"E19.right"),sQuery(id+"F0.wireOp",EDGE,"E31.bottom"),sQuery(id+"F0.wireOp",EDGE,"E31.top"),sQuery(id+"F0.wireOp",EDGE,"E32.left"),sQuery(id+"F0.wireOp",EDGE,"E32.right"),sQuery(id+"F0.wireOp",EDGE,"E33.left"),sQuery(id+"F0.wireOp",EDGE,"E33.right"),sQuery(id+"F0.wireOp",EDGE,"E34.trimOffspring"),sQuery(id+"F0.wireOp",EDGE,"E35.trimOffspring"),sQuery(id+"F0.wireOp",EDGE,"E36.trimOffspring"),sQuery(id+"F0.wireOp",EDGE,"E37.trimOffspring"),sQuery(id+"F0.wireOp",EDGE,"E38.trimOffspring"),sQuery(id+"F0.wireOp",EDGE,"E39.trimOffspring"),sQuery(id+"F0.wireOp",EDGE,"E40.trimOffspring"),sQuery(id+"F0.wireOp",EDGE,"E41.trimOffspring"),sQuery(id+"F0.wireOp",EDGE,"E42.bottom"),sQuery(id+"F0.wireOp",EDGE,"E42.top"),sQuery(id+"F0.wireOp",EDGE,"E42.left"),sQuery(id+"F0.wireOp",EDGE,"E42.right"),sQuery(id+"F0.wireOp",EDGE,"E43.bottom"),sQuery(id+"F0.wireOp",EDGE,"E43.top"),sQuery(id+"F0.wireOp",EDGE,"E43.left"),sQuery(id+"F0.wireOp",EDGE,"E43.right"),sQuery(id+"F0.wireOp",EDGE,"7093700b-8509-4908-bad7-ce82e1b1d340.1.0.0"),sQuery(id+"F0.wireOp",EDGE,"7093700b-8509-4908-bad7-ce82e1b1d340.1.0.2"),sQuery(id+"F0.wireOp",EDGE,"7093700b-8509-4908-bad7-ce82e1b1d340.1.0.3"),sQuery(id+"F0.wireOp",EDGE,"7093700b-8509-4908-bad7-ce82e1b1d340.1.0.5"),sQuery(id+"F0.wireOp",EDGE,"7093700b-8509-4908-bad7-ce82e1b1d340.1.0.6"),sQuery(id+"F0.wireOp",EDGE,"7093700b-8509-4908-bad7-ce82e1b1d340.1.0.7"),sQuery(id+"F0.wireOp",EDGE,"7093700b-8509-4908-bad7-ce82e1b1d340.1.0.8"),sQuery(id+"F0.wireOp",EDGE,"7093700b-8509-4908-bad7-ce82e1b1d340.1.0.9"),sQuery(id+"F0.wireOp",EDGE,"7093700b-8509-4908-bad7-ce82e1b1d340.1.0.12"),sQuery(id+"F0.wireOp",EDGE,"7093700b-8509-4908-bad7-ce82e1b1d340.1.0.13"),sQuery(id+"F0.wireOp",EDGE,"7093700b-8509-4908-bad7-ce82e1b1d340.1.0.14"),sQuery(id+"F0.wireOp",EDGE,"7093700b-8509-4908-bad7-ce82e1b1d340.1.0.15"),sQuery(id+"F0.wireOp",EDGE,"7093700b-8509-4908-bad7-ce82e1b1d340.1.0.16"),sQuery(id+"F0.wireOp",EDGE,"7093700b-8509-4908-bad7-ce82e1b1d340.1.0.17"),sQuery(id+"F0.wireOp",EDGE,"7093700b-8509-4908-bad7-ce82e1b1d340.1.0.18"),sQuery(id+"F0.wireOp",EDGE,"7093700b-8509-4908-bad7-ce82e1b1d340.1.0.19"),sQuery(id+"F0.wireOp",EDGE,"7093700b-8509-4908-bad7-ce82e1b1d340.1.0.20"),sQuery(id+"F0.wireOp",EDGE,"7093700b-8509-4908-bad7-ce82e1b1d340.1.0.21"),sQuery(id+"F0.wireOp",EDGE,"7093700b-8509-4908-bad7-ce82e1b1d340.2.0.0"),sQuery(id+"F0.wireOp",EDGE,"7093700b-8509-4908-bad7-ce82e1b1d340.2.0.2"),sQuery(id+"F0.wireOp",EDGE,"7093700b-8509-4908-bad7-ce82e1b1d340.2.0.3"),sQuery(id+"F0.wireOp",EDGE,"7093700b-8509-4908-bad7-ce82e1b1d340.2.0.5"),sQuery(id+"F0.wireOp",EDGE,"7093700b-8509-4908-bad7-ce82e1b1d340.2.0.6"),sQuery(id+"F0.wireOp",EDGE,"7093700b-8509-4908-bad7-ce82e1b1d340.2.0.7"),sQuery(id+"F0.wireOp",EDGE,"7093700b-8509-4908-bad7-ce82e1b1d340.2.0.8"),sQuery(id+"F0.wireOp",EDGE,"7093700b-8509-4908-bad7-ce82e1b1d340.2.0.9"),sQuery(id+"F0.wireOp",EDGE,"7093700b-8509-4908-bad7-ce82e1b1d340.2.0.12"),sQuery(id+"F0.wireOp",EDGE,"7093700b-8509-4908-bad7-ce82e1b1d340.2.0.13"),sQuery(id+"F0.wireOp",EDGE,"7093700b-8509-4908-bad7-ce82e1b1d340.2.0.14"),sQuery(id+"F0.wireOp",EDGE,"7093700b-8509-4908-bad7-ce82e1b1d340.2.0.15"),sQuery(id+"F0.wireOp",EDGE,"7093700b-8509-4908-bad7-ce82e1b1d340.2.0.16"),sQuery(id+"F0.wireOp",EDGE,"7093700b-8509-4908-bad7-ce82e1b1d340.2.0.17"),sQuery(id+"F0.wireOp",EDGE,"7093700b-8509-4908-bad7-ce82e1b1d340.2.0.18"),sQuery(id+"F0.wireOp",EDGE,"7093700b-8509-4908-bad7-ce82e1b1d340.2.0.19"),sQuery(id+"F0.wireOp",EDGE,"7093700b-8509-4908-bad7-ce82e1b1d340.2.0.20"),sQuery(id+"F0.wireOp",EDGE,"7093700b-8509-4908-bad7-ce82e1b1d340.2.0.21"),sQuery(id+"F0.wireOp",EDGE,"c973f7c2-3bf7-4545-afce-7af64f458de9.1.0.0"),sQuery(id+"F0.wireOp",EDGE,"c973f7c2-3bf7-4545-afce-7af64f458de9.1.0.1"),sQuery(id+"F0.wireOp",EDGE,"c973f7c2-3bf7-4545-afce-7af64f458de9.1.0.2"),sQuery(id+"F0.wireOp",EDGE,"c973f7c2-3bf7-4545-afce-7af64f458de9.1.0.4"),sQuery(id+"F0.wireOp",EDGE,"c973f7c2-3bf7-4545-afce-7af64f458de9.1.0.6"),sQuery(id+"F0.wireOp",EDGE,"c973f7c2-3bf7-4545-afce-7af64f458de9.1.0.7"),sQuery(id+"F0.wireOp",EDGE,"c973f7c2-3bf7-4545-afce-7af64f458de9.1.0.9"),sQuery(id+"F0.wireOp",EDGE,"c973f7c2-3bf7-4545-afce-7af64f458de9.1.0.10"),sQuery(id+"F0.wireOp",EDGE,"c973f7c2-3bf7-4545-afce-7af64f458de9.1.0.12"),sQuery(id+"F0.wireOp",EDGE,"c973f7c2-3bf7-4545-afce-7af64f458de9.1.0.14"),sQuery(id+"F0.wireOp",EDGE,"c973f7c2-3bf7-4545-afce-7af64f458de9.1.0.16"),sQuery(id+"F0.wireOp",EDGE,"c973f7c2-3bf7-4545-afce-7af64f458de9.1.0.18"),sQuery(id+"F0.wireOp",EDGE,"c973f7c2-3bf7-4545-afce-7af64f458de9.1.0.19"),sQuery(id+"F0.wireOp",EDGE,"c973f7c2-3bf7-4545-afce-7af64f458de9.1.0.20"),sQuery(id+"F0.wireOp",EDGE,"c973f7c2-3bf7-4545-afce-7af64f458de9.1.0.26"),sQuery(id+"F0.wireOp",EDGE,"c973f7c2-3bf7-4545-afce-7af64f458de9.1.0.28"),sQuery(id+"F0.wireOp",EDGE,"c973f7c2-3bf7-4545-afce-7af64f458de9.1.0.29"),sQuery(id+"F0.wireOp",EDGE,"c973f7c2-3bf7-4545-afce-7af64f458de9.1.0.30"),sQuery(id+"F0.wireOp",EDGE,"c973f7c2-3bf7-4545-afce-7af64f458de9.2.0.0"),sQuery(id+"F0.wireOp",EDGE,"c973f7c2-3bf7-4545-afce-7af64f458de9.2.0.1"),sQuery(id+"F0.wireOp",EDGE,"c973f7c2-3bf7-4545-afce-7af64f458de9.2.0.2"),sQuery(id+"F0.wireOp",EDGE,"c973f7c2-3bf7-4545-afce-7af64f458de9.2.0.4"),sQuery(id+"F0.wireOp",EDGE,"c973f7c2-3bf7-4545-afce-7af64f458de9.2.0.6"),sQuery(id+"F0.wireOp",EDGE,"c973f7c2-3bf7-4545-afce-7af64f458de9.2.0.7"),sQuery(id+"F0.wireOp",EDGE,"c973f7c2-3bf7-4545-afce-7af64f458de9.2.0.9"),sQuery(id+"F0.wireOp",EDGE,"c973f7c2-3bf7-4545-afce-7af64f458de9.2.0.10"),sQuery(id+"F0.wireOp",EDGE,"c973f7c2-3bf7-4545-afce-7af64f458de9.2.0.12"),sQuery(id+"F0.wireOp",EDGE,"c973f7c2-3bf7-4545-afce-7af64f458de9.2.0.14"),sQuery(id+"F0.wireOp",EDGE,"c973f7c2-3bf7-4545-afce-7af64f458de9.2.0.16"),sQuery(id+"F0.wireOp",EDGE,"c973f7c2-3bf7-4545-afce-7af64f458de9.2.0.18"),sQuery(id+"F0.wireOp",EDGE,"c973f7c2-3bf7-4545-afce-7af64f458de9.2.0.19"),sQuery(id+"F0.wireOp",EDGE,"c973f7c2-3bf7-4545-afce-7af64f458de9.2.0.20"),sQuery(id+"F0.wireOp",EDGE,"c973f7c2-3bf7-4545-afce-7af64f458de9.2.0.26"),sQuery(id+"F0.wireOp",EDGE,"c973f7c2-3bf7-4545-afce-7af64f458de9.2.0.28"),sQuery(id+"F0.wireOp",EDGE,"c973f7c2-3bf7-4545-afce-7af64f458de9.2.0.29"),sQuery(id+"F0.wireOp",EDGE,"c973f7c2-3bf7-4545-afce-7af64f458de9.2.0.30"),sQuery(id+"F0.wireOp",EDGE,"E44.left"),sQuery(id+"F0.wireOp",EDGE,"E44.right"),sQuery(id+"F0.wireOp",EDGE,"E45.left"),sQuery(id+"F0.wireOp",EDGE,"E45.right"),sQuery(id+"F0.wireOp",EDGE,"E46"),sQuery(id+"F0.wireOp",EDGE,"E47"),sQuery(id+"F0.wireOp",EDGE,"E48"),sQuery(id+"F0.wireOp",EDGE,"E49")])],"isStart":false});
            var sketch = newSketch(context, id + "F24", { "sketchPlane" : qUnion([Q0])});
            skLineSegment(sketch, "E172.bottom", {"start": v(-149.5, 17.96) * mm, "end": v(-139.5, 17.96) * mm});
            skLineSegment(sketch, "E172.top", {"start": v(-149.5, -57.04) * mm, "end": v(-139.5, -57.04) * mm});
            skLineSegment(sketch, "E172.left", {"start": v(-149.5, 17.96) * mm, "end": v(-149.5, -57.04) * mm});
            skLineSegment(sketch, "E172.right", {"start": v(-139.5, 17.96) * mm, "end": v(-139.5, -57.04) * mm});
            skLineSegment(sketch, "E173.bottom", {"start": v(0.5, -57.04) * mm, "end": v(-9.5, -57.04) * mm});
            skLineSegment(sketch, "E173.top", {"start": v(0.5, 17.96) * mm, "end": v(-9.5, 17.96) * mm});
            skLineSegment(sketch, "E173.left", {"start": v(0.5, -57.04) * mm, "end": v(0.5, 17.96) * mm});
            skLineSegment(sketch, "E173.right", {"start": v(-9.5, -57.04) * mm, "end": v(-9.5, 17.96) * mm});
            skSolve(sketch);
        }
        {
            var Q0;
            Q0=makeQuery(id+"F24.imprint","IMPRINT",FACE,{"disambiguationData":[TD([[makeQuery(id+"F24.imprint","IMPRINT",EDGE,{"derivedFrom":sQuery(id+"F24.wireOp",EDGE,"E173.bottom")}),-1.0]])]});
            var Q1;
            Q1=makeQuery(id+"F24.imprint","IMPRINT",FACE,{"disambiguationData":[TD([[makeQuery(id+"F24.imprint","IMPRINT",EDGE,{"derivedFrom":sQuery(id+"F24.wireOp",EDGE,"E172.bottom")}),1.0]])]});
            extrude(context, id + "F25", {"entities" : qUnion([Q0, Q1]), "operationType" : NewBodyOperationType.ADD, "depth" : 4 * mm});
        }
        {
            var Q0;
            {var subQ0=sQuery(id+"F0.wireOp",EDGE,"E0.bottom");Q0=makeQuery(id+"F25.boolean.opBoolean","MERGE",FACE,{"derivedFrom":[makeQuery(id+"FcxvOkpkAmDw7ie_3.boolean.opBoolean","MERGE",FACE,{"derivedFrom":[makeQuery(id+"F3.boolean.opBoolean","MERGE",FACE,{"derivedFrom":[makeQuery(id+"F2.opExtrude","SWEPT_FACE",FACE,{"disambiguationData":[OSD([subQ0])]}),makeQuery(id+"F3.opExtrude","SWEPT_FACE",FACE,{"disambiguationData":[OSD([subQ0])]})]}),makeQuery(id+"FcxvOkpkAmDw7ie_3.opExtrude","SWEPT_FACE",FACE,{"disambiguationData":[OSD([sQuery(id+"FNICA6uDXxchBR6_3.wireOp",EDGE,"OznuT0um-5Ypx-SHlm-bkf4-iYFOqL2Sfz4i.bottom")])]})]}),makeQuery(id+"F25.opExtrude","SWEPT_FACE",FACE,{"disambiguationData":[OSD([sQuery(id+"F24.wireOp",EDGE,"E172.top")])]}),makeQuery(id+"F25.opExtrude","SWEPT_FACE",FACE,{"disambiguationData":[OSD([sQuery(id+"F24.wireOp",EDGE,"E173.bottom")])]})]});}
            var sketch = newSketch(context, id + "F26", { "sketchPlane" : qUnion([Q0])});
            skLineSegment(sketch, "E174.bottom", {"start": v(-149.5, 0) * mm, "end": v(-141.5, 0) * mm});
            skLineSegment(sketch, "E174.top", {"start": v(-149.5, 7) * mm, "end": v(-141.5, 7) * mm});
            skLineSegment(sketch, "E174.left", {"start": v(-149.5, 0) * mm, "end": v(-149.5, 7) * mm});
            skLineSegment(sketch, "E174.right", {"start": v(-141.5, 0) * mm, "end": v(-141.5, 7) * mm});
            skLineSegment(sketch, "E175.bottom", {"start": v(0.5, 0) * mm, "end": v(-7.5, 0) * mm});
            skLineSegment(sketch, "E175.top", {"start": v(0.5, 7) * mm, "end": v(-7.5, 7) * mm});
            skLineSegment(sketch, "E175.left", {"start": v(0.5, 0) * mm, "end": v(0.5, 7) * mm});
            skLineSegment(sketch, "E175.right", {"start": v(-7.5, 0) * mm, "end": v(-7.5, 7) * mm});
            skSolve(sketch);
        }
        {
            var Q0;
            Q0=qSketchRegion(id+"F26",true);
            extrude(context, id + "F27", {"entities" : qUnion([Q0]), "operationType" : NewBodyOperationType.REMOVE, "oppositeDirection" : true, "depth" : 77.8 * mm});
        }
        {
            var Q0;
            {var subQ0=sQuery(id+"F0.wireOp",EDGE,"E0.right");var subQ1=sQuery(id+"F0.wireOp",EDGE,"E0.top");var subQ3=sQuery(id+"F0.wireOp",EDGE,"E0.bottom");var subQ5=sQuery(id+"F0.wireOp",EDGE,"E47");var subQ6=sQuery(id+"F0.wireOp",EDGE,"E46");var subQ7=sQuery(id+"F0.wireOp",EDGE,"E45.right");var subQ8=sQuery(id+"F0.wireOp",EDGE,"E45.left");var subQ9=sQuery(id+"F0.wireOp",EDGE,"E44.right");var subQ10=sQuery(id+"F0.wireOp",EDGE,"E44.left");var subQ11=sQuery(id+"F0.wireOp",EDGE,"c973f7c2-3bf7-4545-afce-7af64f458de9.2.0.30");var subQ12=sQuery(id+"F0.wireOp",EDGE,"c973f7c2-3bf7-4545-afce-7af64f458de9.2.0.0");var subQ13=sQuery(id+"F0.wireOp",EDGE,"c973f7c2-3bf7-4545-afce-7af64f458de9.2.0.29");var subQ16=sQuery(id+"F0.wireOp",EDGE,"c973f7c2-3bf7-4545-afce-7af64f458de9.2.0.10");var subQ17=sQuery(id+"F0.wireOp",EDGE,"c973f7c2-3bf7-4545-afce-7af64f458de9.2.0.28");var subQ20=sQuery(id+"F0.wireOp",EDGE,"c973f7c2-3bf7-4545-afce-7af64f458de9.2.0.18");var subQ21=sQuery(id+"F0.wireOp",EDGE,"c973f7c2-3bf7-4545-afce-7af64f458de9.2.0.26");var subQ24=sQuery(id+"F0.wireOp",EDGE,"c973f7c2-3bf7-4545-afce-7af64f458de9.2.0.1");var subQ25=sQuery(id+"F0.wireOp",EDGE,"c973f7c2-3bf7-4545-afce-7af64f458de9.2.0.19");var subQ27=sQuery(id+"F0.wireOp",EDGE,"c973f7c2-3bf7-4545-afce-7af64f458de9.2.0.9");var subQ30=sQuery(id+"F0.wireOp",EDGE,"c973f7c2-3bf7-4545-afce-7af64f458de9.2.0.4");var subQ34=sQuery(id+"F0.wireOp",EDGE,"c973f7c2-3bf7-4545-afce-7af64f458de9.2.0.2");var subQ35=sQuery(id+"F0.wireOp",EDGE,"c973f7c2-3bf7-4545-afce-7af64f458de9.2.0.7");var subQ37=sQuery(id+"F0.wireOp",EDGE,"c973f7c2-3bf7-4545-afce-7af64f458de9.2.0.16");var subQ39=sQuery(id+"F0.wireOp",EDGE,"c973f7c2-3bf7-4545-afce-7af64f458de9.2.0.20");var subQ41=sQuery(id+"F0.wireOp",EDGE,"c973f7c2-3bf7-4545-afce-7af64f458de9.2.0.12");var subQ43=sQuery(id+"F0.wireOp",EDGE,"c973f7c2-3bf7-4545-afce-7af64f458de9.2.0.14");var subQ44=sQuery(id+"F0.wireOp",EDGE,"c973f7c2-3bf7-4545-afce-7af64f458de9.2.0.6");var subQ45=sQuery(id+"F0.wireOp",EDGE,"c973f7c2-3bf7-4545-afce-7af64f458de9.1.0.30");var subQ46=sQuery(id+"F0.wireOp",EDGE,"c973f7c2-3bf7-4545-afce-7af64f458de9.1.0.0");var subQ47=sQuery(id+"F0.wireOp",EDGE,"c973f7c2-3bf7-4545-afce-7af64f458de9.1.0.29");var subQ50=sQuery(id+"F0.wireOp",EDGE,"c973f7c2-3bf7-4545-afce-7af64f458de9.1.0.10");var subQ51=sQuery(id+"F0.wireOp",EDGE,"c973f7c2-3bf7-4545-afce-7af64f458de9.1.0.28");var subQ54=sQuery(id+"F0.wireOp",EDGE,"c973f7c2-3bf7-4545-afce-7af64f458de9.1.0.18");var subQ55=sQuery(id+"F0.wireOp",EDGE,"c973f7c2-3bf7-4545-afce-7af64f458de9.1.0.26");var subQ58=sQuery(id+"F0.wireOp",EDGE,"c973f7c2-3bf7-4545-afce-7af64f458de9.1.0.1");var subQ59=sQuery(id+"F0.wireOp",EDGE,"c973f7c2-3bf7-4545-afce-7af64f458de9.1.0.19");var subQ61=sQuery(id+"F0.wireOp",EDGE,"c973f7c2-3bf7-4545-afce-7af64f458de9.1.0.9");var subQ64=sQuery(id+"F0.wireOp",EDGE,"c973f7c2-3bf7-4545-afce-7af64f458de9.1.0.4");var subQ68=sQuery(id+"F0.wireOp",EDGE,"c973f7c2-3bf7-4545-afce-7af64f458de9.1.0.2");var subQ69=sQuery(id+"F0.wireOp",EDGE,"c973f7c2-3bf7-4545-afce-7af64f458de9.1.0.7");var subQ71=sQuery(id+"F0.wireOp",EDGE,"c973f7c2-3bf7-4545-afce-7af64f458de9.1.0.16");var subQ73=sQuery(id+"F0.wireOp",EDGE,"c973f7c2-3bf7-4545-afce-7af64f458de9.1.0.20");var subQ75=sQuery(id+"F0.wireOp",EDGE,"c973f7c2-3bf7-4545-afce-7af64f458de9.1.0.12");var subQ77=sQuery(id+"F0.wireOp",EDGE,"c973f7c2-3bf7-4545-afce-7af64f458de9.1.0.14");var subQ78=sQuery(id+"F0.wireOp",EDGE,"c973f7c2-3bf7-4545-afce-7af64f458de9.1.0.6");var subQ79=sQuery(id+"F0.wireOp",EDGE,"7093700b-8509-4908-bad7-ce82e1b1d340.2.0.21");var subQ81=sQuery(id+"F0.wireOp",EDGE,"7093700b-8509-4908-bad7-ce82e1b1d340.2.0.20");var subQ82=sQuery(id+"F0.wireOp",EDGE,"7093700b-8509-4908-bad7-ce82e1b1d340.2.0.12");var subQ83=sQuery(id+"F0.wireOp",EDGE,"7093700b-8509-4908-bad7-ce82e1b1d340.2.0.15");var subQ86=sQuery(id+"F0.wireOp",EDGE,"7093700b-8509-4908-bad7-ce82e1b1d340.2.0.13");var subQ87=sQuery(id+"F0.wireOp",EDGE,"7093700b-8509-4908-bad7-ce82e1b1d340.2.0.17");var subQ90=sQuery(id+"F0.wireOp",EDGE,"7093700b-8509-4908-bad7-ce82e1b1d340.2.0.19");var subQ91=sQuery(id+"F0.wireOp",EDGE,"7093700b-8509-4908-bad7-ce82e1b1d340.2.0.18");var subQ93=sQuery(id+"F0.wireOp",EDGE,"7093700b-8509-4908-bad7-ce82e1b1d340.2.0.16");var subQ97=sQuery(id+"F0.wireOp",EDGE,"7093700b-8509-4908-bad7-ce82e1b1d340.2.0.2");var subQ99=sQuery(id+"F0.wireOp",EDGE,"7093700b-8509-4908-bad7-ce82e1b1d340.2.0.3");var subQ102=sQuery(id+"F0.wireOp",EDGE,"7093700b-8509-4908-bad7-ce82e1b1d340.2.0.0");var subQ104=sQuery(id+"F0.wireOp",EDGE,"7093700b-8509-4908-bad7-ce82e1b1d340.2.0.5");var subQ105=sQuery(id+"F0.wireOp",EDGE,"7093700b-8509-4908-bad7-ce82e1b1d340.2.0.14");var subQ108=sQuery(id+"F0.wireOp",EDGE,"7093700b-8509-4908-bad7-ce82e1b1d340.2.0.6");var subQ110=sQuery(id+"F0.wireOp",EDGE,"7093700b-8509-4908-bad7-ce82e1b1d340.2.0.9");var subQ111=sQuery(id+"F0.wireOp",EDGE,"7093700b-8509-4908-bad7-ce82e1b1d340.2.0.8");var subQ112=sQuery(id+"F0.wireOp",EDGE,"7093700b-8509-4908-bad7-ce82e1b1d340.2.0.7");var subQ113=sQuery(id+"F0.wireOp",EDGE,"E33.left");var subQ114=sQuery(id+"F0.wireOp",EDGE,"E32.right");var subQ115=sQuery(id+"F0.wireOp",EDGE,"E32.left");var subQ116=sQuery(id+"F0.wireOp",EDGE,"E31.top");var subQ117=sQuery(id+"F0.wireOp",EDGE,"E31.bottom");var subQ118=sQuery(id+"F0.wireOp",EDGE,"E19.right");var subQ119=sQuery(id+"F0.wireOp",EDGE,"E19.top");var subQ121=sQuery(id+"F0.wireOp",EDGE,"E35.trimOffspring");var subQ124=sQuery(id+"F0.wireOp",EDGE,"E19.bottom");var subQ126=sQuery(id+"F0.wireOp",EDGE,"E37.trimOffspring");var subQ128=sQuery(id+"F0.wireOp",EDGE,"E19.left");var subQ132=sQuery(id+"F0.wireOp",EDGE,"E34.trimOffspring");var subQ135=sQuery(id+"F0.wireOp",EDGE,"E27.trimOffspring");var subQ136=sQuery(id+"F0.wireOp",EDGE,"E40.trimOffspring");var subQ139=sQuery(id+"F0.wireOp",EDGE,"E26.trimOffspring");var subQ142=sQuery(id+"F0.wireOp",EDGE,"E24.trimOffspring");var subQ146=sQuery(id+"F0.wireOp",EDGE,"E23.trimOffspring");var subQ147=sQuery(id+"F0.wireOp",EDGE,"E30.trimOffspring");var subQ148=sQuery(id+"F0.wireOp",EDGE,"E22.right");var subQ149=sQuery(id+"F0.wireOp",EDGE,"E29.trimOffspring");var subQ150=sQuery(id+"F0.wireOp",EDGE,"E22.left");var subQ151=sQuery(id+"F0.wireOp",EDGE,"E28.trimOffspring");var subQ152=sQuery(id+"F0.wireOp",EDGE,"E21.right");var subQ153=sQuery(id+"F0.wireOp",EDGE,"E21.left");var subQ154=sQuery(id+"F0.wireOp",EDGE,"E20.top");var subQ155=sQuery(id+"F0.wireOp",EDGE,"E25.trimOffspring");var subQ156=sQuery(id+"F0.wireOp",EDGE,"E20.bottom");var subQ157=sQuery(id+"F0.wireOp",EDGE,"E18.right");var subQ158=sQuery(id+"F0.wireOp",EDGE,"E18.top");var subQ162=sQuery(id+"F0.wireOp",EDGE,"E18.bottom");var subQ165=sQuery(id+"F0.wireOp",EDGE,"E14.top");var subQ168=sQuery(id+"F0.wireOp",EDGE,"E14.bottom");var subQ171=sQuery(id+"F0.wireOp",EDGE,"E33.right");var subQ174=sQuery(id+"F0.wireOp",EDGE,"7093700b-8509-4908-bad7-ce82e1b1d340.1.0.16");var subQ175=sQuery(id+"F0.wireOp",EDGE,"E14.right");var subQ176=sQuery(id+"F0.wireOp",EDGE,"E14.left");var subQ177=sQuery(id+"F0.wireOp",EDGE,"E18.left");var subQ180=sQuery(id+"F0.wireOp",EDGE,"E36.trimOffspring");var subQ181=sQuery(id+"F0.wireOp",EDGE,"E38.trimOffspring");var subQ185=sQuery(id+"F0.wireOp",EDGE,"7093700b-8509-4908-bad7-ce82e1b1d340.1.0.17");var subQ186=sQuery(id+"F0.wireOp",EDGE,"7093700b-8509-4908-bad7-ce82e1b1d340.1.0.20");var subQ193=sQuery(id+"F0.wireOp",EDGE,"7093700b-8509-4908-bad7-ce82e1b1d340.1.0.19");var subQ200=sQuery(id+"F0.wireOp",EDGE,"E39.trimOffspring");var subQ201=sQuery(id+"F0.wireOp",EDGE,"E41.trimOffspring");var subQ202=sQuery(id+"F0.wireOp",EDGE,"E42.left");var subQ203=sQuery(id+"F0.wireOp",EDGE,"E42.bottom");var subQ206=sQuery(id+"F0.wireOp",EDGE,"E42.right");var subQ208=sQuery(id+"F0.wireOp",EDGE,"E42.top");var subQ212=sQuery(id+"F0.wireOp",EDGE,"E43.left");var subQ213=sQuery(id+"F0.wireOp",EDGE,"E43.bottom");var subQ216=sQuery(id+"F0.wireOp",EDGE,"E43.right");var subQ218=sQuery(id+"F0.wireOp",EDGE,"E43.top");var subQ222=sQuery(id+"F0.wireOp",EDGE,"7093700b-8509-4908-bad7-ce82e1b1d340.1.0.0");var subQ223=sQuery(id+"F0.wireOp",EDGE,"7093700b-8509-4908-bad7-ce82e1b1d340.1.0.2");var subQ226=sQuery(id+"F0.wireOp",EDGE,"7093700b-8509-4908-bad7-ce82e1b1d340.1.0.9");var subQ228=sQuery(id+"F0.wireOp",EDGE,"7093700b-8509-4908-bad7-ce82e1b1d340.1.0.15");var subQ230=sQuery(id+"F0.wireOp",EDGE,"7093700b-8509-4908-bad7-ce82e1b1d340.1.0.8");var subQ232=sQuery(id+"F0.wireOp",EDGE,"7093700b-8509-4908-bad7-ce82e1b1d340.1.0.3");var subQ233=sQuery(id+"F0.wireOp",EDGE,"7093700b-8509-4908-bad7-ce82e1b1d340.1.0.5");var subQ234=sQuery(id+"F0.wireOp",EDGE,"7093700b-8509-4908-bad7-ce82e1b1d340.1.0.6");var subQ235=sQuery(id+"F0.wireOp",EDGE,"7093700b-8509-4908-bad7-ce82e1b1d340.1.0.7");var subQ236=sQuery(id+"F0.wireOp",EDGE,"7093700b-8509-4908-bad7-ce82e1b1d340.1.0.12");var subQ237=sQuery(id+"F0.wireOp",EDGE,"7093700b-8509-4908-bad7-ce82e1b1d340.1.0.13");var subQ238=sQuery(id+"F0.wireOp",EDGE,"7093700b-8509-4908-bad7-ce82e1b1d340.1.0.14");var subQ246=sQuery(id+"F0.wireOp",EDGE,"7093700b-8509-4908-bad7-ce82e1b1d340.1.0.18");var subQ251=sQuery(id+"F0.wireOp",EDGE,"7093700b-8509-4908-bad7-ce82e1b1d340.1.0.21");var subQ255=sQuery(id+"F0.wireOp",EDGE,"E49");var subQ256=sQuery(id+"F0.wireOp",EDGE,"E48");var subQ257=sQuery(id+"F0.wireOp",EDGE,"E0.left");var subQ258=makeQuery(id+"F2.opExtrude","CAP_FACE",FACE,{"disambiguationData":[OSD([subQ3,subQ1,subQ257,subQ0,sQuery(id+"F0.wireOp",EDGE,"6XQCNLW2-68Wz-nC9p-wT4x-b90YEvEmSNLj"),sQuery(id+"F0.wireOp",EDGE,"E3"),sQuery(id+"F0.wireOp",EDGE,"E4"),sQuery(id+"F0.wireOp",EDGE,"E7"),sQuery(id+"F0.wireOp",EDGE,"E8"),sQuery(id+"F0.wireOp",EDGE,"E9"),sQuery(id+"F0.wireOp",EDGE,"E10"),sQuery(id+"F0.wireOp",EDGE,"E11"),sQuery(id+"F0.wireOp",EDGE,"E12"),sQuery(id+"F0.wireOp",EDGE,"E13"),subQ168,subQ165,subQ176,subQ175,sQuery(id+"F0.wireOp",EDGE,"E15"),sQuery(id+"F0.wireOp",EDGE,"E16"),subQ162,subQ158,subQ177,subQ157,subQ156,subQ154,subQ153,subQ152,subQ150,subQ148,subQ146,subQ142,subQ155,subQ139,subQ135,subQ151,subQ149,subQ147,subQ124,subQ119,subQ128,subQ118,subQ117,subQ116,subQ115,subQ114,subQ113,subQ171,subQ132,subQ121,subQ180,subQ126,subQ181,subQ200,subQ136,subQ201,subQ203,subQ208,subQ202,subQ206,subQ213,subQ218,subQ212,subQ216,subQ222,subQ223,subQ232,subQ233,subQ234,subQ235,subQ230,subQ226,subQ236,subQ237,subQ238,subQ228,subQ174,subQ185,subQ246,subQ193,subQ186,subQ251,subQ102,subQ97,subQ99,subQ104,subQ108,subQ112,subQ111,subQ110,subQ82,subQ86,subQ105,subQ83,subQ93,subQ87,subQ91,subQ90,subQ81,subQ79,subQ46,subQ58,subQ68,subQ64,subQ78,subQ69,subQ61,subQ50,subQ75,subQ77,subQ71,subQ54,subQ59,subQ73,subQ55,subQ51,subQ47,subQ45,subQ12,subQ24,subQ34,subQ30,subQ44,subQ35,subQ27,subQ16,subQ41,subQ43,subQ37,subQ20,subQ25,subQ39,subQ21,subQ17,subQ13,subQ11,subQ10,subQ9,subQ8,subQ7,subQ6,subQ5,subQ256,subQ255])],"isStart":true});Q0=makeQuery(id+"FcxvOkpkAmDw7ie_3.boolean.opBoolean","MERGE",FACE,{"derivedFrom":[makeQuery(id+"F22.boolean.opBoolean","SPLIT",FACE,{"disambiguationData":[TD([makeQuery(id+"F2.opExtrude","SWEPT_FACE",FACE,{"disambiguationData":[OSD([subQ257])]})])],"derivedFrom":subQ258}),makeQuery(id+"F22.boolean.opBoolean","SPLIT",FACE,{"disambiguationData":[TD([makeQuery(id+"F2.opExtrude","SWEPT_FACE",FACE,{"disambiguationData":[OSD([subQ0])]})])],"derivedFrom":subQ258}),makeQuery(id+"FcxvOkpkAmDw7ie_3.opExtrude","CAP_FACE",FACE,{"disambiguationData":[OSD([sQuery(id+"FNICA6uDXxchBR6_3.wireOp",EDGE,"OznuT0um-5Ypx-SHlm-bkf4-iYFOqL2Sfz4i.bottom"),sQuery(id+"FNICA6uDXxchBR6_3.wireOp",EDGE,"OznuT0um-5Ypx-SHlm-bkf4-iYFOqL2Sfz4i.top"),sQuery(id+"FNICA6uDXxchBR6_3.wireOp",EDGE,"OznuT0um-5Ypx-SHlm-bkf4-iYFOqL2Sfz4i.left"),sQuery(id+"FNICA6uDXxchBR6_3.wireOp",EDGE,"OznuT0um-5Ypx-SHlm-bkf4-iYFOqL2Sfz4i.right")])],"isStart":false}),makeQuery(id+"FcxvOkpkAmDw7ie_3.opExtrude","CAP_FACE",FACE,{"disambiguationData":[OSD([sQuery(id+"FNICA6uDXxchBR6_3.wireOp",EDGE,"YSd4T3NJ-1L5Y-MwVD-52kg-DvB7oUMf2wlW.bottom"),sQuery(id+"FNICA6uDXxchBR6_3.wireOp",EDGE,"YSd4T3NJ-1L5Y-MwVD-52kg-DvB7oUMf2wlW.top"),sQuery(id+"FNICA6uDXxchBR6_3.wireOp",EDGE,"YSd4T3NJ-1L5Y-MwVD-52kg-DvB7oUMf2wlW.left"),sQuery(id+"FNICA6uDXxchBR6_3.wireOp",EDGE,"YSd4T3NJ-1L5Y-MwVD-52kg-DvB7oUMf2wlW.right")])],"isStart":false}),makeQuery(id+"FcxvOkpkAmDw7ie_3.opExtrude","CAP_FACE",FACE,{"disambiguationData":[OSD([sQuery(id+"FNICA6uDXxchBR6_3.wireOp",EDGE,"awoJ12up-LfxG-riiH-PCTd-TFvWrLSTyvKZ.bottom"),sQuery(id+"FNICA6uDXxchBR6_3.wireOp",EDGE,"awoJ12up-LfxG-riiH-PCTd-TFvWrLSTyvKZ.top"),sQuery(id+"FNICA6uDXxchBR6_3.wireOp",EDGE,"awoJ12up-LfxG-riiH-PCTd-TFvWrLSTyvKZ.left"),sQuery(id+"FNICA6uDXxchBR6_3.wireOp",EDGE,"awoJ12up-LfxG-riiH-PCTd-TFvWrLSTyvKZ.right")])],"isStart":false}),makeQuery(id+"FcxvOkpkAmDw7ie_3.opExtrude","CAP_FACE",FACE,{"disambiguationData":[OSD([sQuery(id+"FNICA6uDXxchBR6_3.wireOp",EDGE,"WfW6qyGR-5Y5B-en90-Dwp4-fLCMDk8WttTC.bottom"),sQuery(id+"FNICA6uDXxchBR6_3.wireOp",EDGE,"WfW6qyGR-5Y5B-en90-Dwp4-fLCMDk8WttTC.top"),sQuery(id+"FNICA6uDXxchBR6_3.wireOp",EDGE,"WfW6qyGR-5Y5B-en90-Dwp4-fLCMDk8WttTC.left"),sQuery(id+"FNICA6uDXxchBR6_3.wireOp",EDGE,"WfW6qyGR-5Y5B-en90-Dwp4-fLCMDk8WttTC.right")])],"isStart":false})]});}
            var sketch = newSketch(context, id + "F28", { "sketchPlane" : qUnion([Q0])});
            skLineSegment(sketch, "E176.bottom", {"start": v(-141.5, -17.96) * mm, "end": v(-7.5, -17.96) * mm});
            skLineSegment(sketch, "E176.top", {"start": v(-141.5, -15.46) * mm, "end": v(-7.5, -15.46) * mm});
            skLineSegment(sketch, "E176.left", {"start": v(-141.5, -17.96) * mm, "end": v(-141.5, -15.46) * mm});
            skLineSegment(sketch, "E176.right", {"start": v(-7.5, -17.96) * mm, "end": v(-7.5, -15.46) * mm});
            skSolve(sketch);
        }
        {
            var Q0;
            Q0=qSketchRegion(id+"F28",true);
            extrude(context, id + "F29", {"entities" : qUnion([Q0]), "operationType" : NewBodyOperationType.REMOVE, "oppositeDirection" : true, "depth" : 3 * mm});
        }
        {
            var Q0;
            Q0=qCreatedBy(makeId("Top.planeOp"),FACE);
            var sketch = newSketch(context, id + "F30", { "sketchPlane" : qUnion([Q0])});
            skCircle(sketch, "E177", {"center": v(-177.94, 31.78) * mm, "radius": 4.9 * mm});
            skSolve(sketch);
        }
        {
            var Q0;
            Q0=makeQuery(id+"F30.imprint","IMPRINT",FACE,{"disambiguationData":[TD([[makeQuery(id+"F30.imprint","IMPRINT",EDGE,{"derivedFrom":sQuery(id+"F30.wireOp",EDGE,"E177")}),1.0]])]});
            extrude(context, id + "F31", {"entities" : qUnion([Q0]), "depth" : 4 * mm});
        }
        {
            var Q0;
            Q0=makeQuery(id+"F31.opExtrude","CAP_FACE",FACE,{"disambiguationData":[OSD([sQuery(id+"F30.wireOp",EDGE,"E177")])],"isStart":false});
            var sketch = newSketch(context, id + "F32", { "sketchPlane" : qUnion([Q0])});
            skCircle(sketch, "E178", {"center": v(-177.94, 31.78) * mm, "radius": 3.5 * mm});
            skSolve(sketch);
        }
        {
            var Q0;
            Q0=makeQuery(id+"F32.imprint","IMPRINT",FACE,{"disambiguationData":[TD([[makeQuery(id+"F32.imprint","IMPRINT",EDGE,{"derivedFrom":sQuery(id+"F32.wireOp",EDGE,"E178")}),1.0]])]});
            extrude(context, id + "F33", {"entities" : qUnion([Q0]), "operationType" : NewBodyOperationType.ADD, "depth" : 6 * mm});
        }
        {
            var Q0;
            Q0=makeQuery(id+"F31.opExtrude","CAP_FACE",FACE,{"disambiguationData":[OSD([sQuery(id+"F30.wireOp",EDGE,"E177")])],"isStart":true});
            var sketch = newSketch(context, id + "F34", { "sketchPlane" : qUnion([Q0])});
            skCircle(sketch, "E179", {"center": v(-177.94, -31.78) * mm, "radius": 6 * mm});
            skSolve(sketch);
        }
        {
            var Q0;
            Q0=makeQuery(id+"F34.imprint","IMPRINT",FACE,{"disambiguationData":[TD([[makeQuery(id+"F34.imprint","IMPRINT",EDGE,{"derivedFrom":sQuery(id+"F34.wireOp",EDGE,"E179")}),1.0]])]});
            extrude(context, id + "F35", {"entities" : qUnion([Q0]), "operationType" : NewBodyOperationType.ADD, "oppositeDirection" : true, "depth" : 1 * mm});
        }
        {
            var Q0;
            Q0=makeQuery(id+"F31.opExtrude","CAP_FACE",FACE,{"disambiguationData":[OSD([sQuery(id+"F30.wireOp",EDGE,"E177")])],"isStart":true});
            var sketch = newSketch(context, id + "F36", { "sketchPlane" : qUnion([Q0])});
            skLineSegment(sketch, "E180.bottom", {"start": v(-176.94, -33.03) * mm, "end": v(-178.94, -33.03) * mm});
            skLineSegment(sketch, "E180.top", {"start": v(-176.94, -30.53) * mm, "end": v(-178.94, -30.53) * mm});
            skLineSegment(sketch, "E180.left", {"start": v(-176.94, -33.03) * mm, "end": v(-176.94, -30.53) * mm});
            skLineSegment(sketch, "E180.right", {"start": v(-178.94, -33.03) * mm, "end": v(-178.94, -30.53) * mm});
            skPoint(sketch, "E180.middle", {"position": v(-177.94, -31.78) * mm});
            skSolve(sketch);
        }
        {
            var Q0;
            Q0=makeQuery(id+"F36.imprint","IMPRINT",FACE,{"disambiguationData":[TD([[makeQuery(id+"F36.imprint","IMPRINT",EDGE,{"derivedFrom":sQuery(id+"F36.wireOp",EDGE,"E180.bottom")}),-1.0]])]});
            extrude(context, id + "F37", {"entities" : qUnion([Q0]), "operationType" : NewBodyOperationType.REMOVE, "oppositeDirection" : true, "depth" : 2.5 * mm});
        }
        {
            var Q0;
            Q0=makeQuery(id+"F31.opExtrude","CAP_EDGE",EDGE,{"disambiguationData":[OSD([sQuery(id+"F30.wireOp",EDGE,"E177")])],"isStart":false});
            fillet(context, id + "F38", {"entities" : qUnion([Q0]), "radius" : 1 * mm, "tangentPropagation" : true, "allowEdgeOverflow" : false});
        }
        {
            var Q0;
            Q0=makeQuery(id+"F33.opExtrude","CAP_EDGE",EDGE,{"disambiguationData":[OSD([sQuery(id+"F32.wireOp",EDGE,"E178")])],"isStart":false});
            fillet(context, id + "F39", {"entities" : qUnion([Q0]), "radius" : 0.5 * mm, "tangentPropagation" : true, "allowEdgeOverflow" : false});
        }
        {
            var Q0;
            Q0=qCreatedBy(makeId("Top.planeOp"),FACE);
            var sketch = newSketch(context, id + "F40", { "sketchPlane" : qUnion([Q0])});
            skCircle(sketch, "E181", {"center": v(-112.45, -89.06) * mm, "radius": 3.1 * mm});
            skCircle(sketch, "E182", {"center": v(-112.45, -89.06) * mm, "radius": 3.75 * mm});
            skSolve(sketch);
        }
        {
            var Q0;
            Q0=makeQuery(id+"F40.imprint","IMPRINT",FACE,{"disambiguationData":[TD([[makeQuery(id+"F40.imprint","IMPRINT",EDGE,{"derivedFrom":sQuery(id+"F40.wireOp",EDGE,"E181")}),-1.0]])]});
            extrude(context, id + "F41", {"entities" : qUnion([Q0]), "depth" : 12 * mm});
        }
        {
            var Q0;
            Q0=makeQuery(id+"F41.opExtrude","CAP_FACE",FACE,{"disambiguationData":[OSD([sQuery(id+"F40.wireOp",EDGE,"E181"),sQuery(id+"F40.wireOp",EDGE,"E182")])],"isStart":true});
            var sketch = newSketch(context, id + "F42", { "sketchPlane" : qUnion([Q0])});
            skCircle(sketch, "E183", {"center": v(-112.45, 89.06) * mm, "radius": 4.5 * mm});
            skSolve(sketch);
        }
        {
            var Q0;
            Q0=makeQuery(id+"F42.imprint","IMPRINT",FACE,{"disambiguationData":[TD([[makeQuery(id+"F42.imprint","IMPRINT",EDGE,{"derivedFrom":sQuery(id+"F42.wireOp",EDGE,"E183")}),1.0]])]});
            extrude(context, id + "F43", {"entities" : qUnion([Q0]), "operationType" : NewBodyOperationType.ADD, "oppositeDirection" : true, "depth" : 13 * mm});
        }
        {
            var Q0;
            {var subQ0=sQuery(id+"F40.wireOp",EDGE,"E182");Q0=makeQuery(id+"F43.boolean.opBoolean","MERGE",FACE,{"derivedFrom":[makeQuery(id+"F41.opExtrude","CAP_FACE",FACE,{"disambiguationData":[OSD([sQuery(id+"F40.wireOp",EDGE,"E181"),subQ0])],"isStart":true}),makeQuery(id+"F43.opExtrude","CAP_FACE",FACE,{"disambiguationData":[OSD([subQ0,sQuery(id+"F42.wireOp",EDGE,"E183")])],"isStart":true})]});}
            var sketch = newSketch(context, id + "F44", { "sketchPlane" : qUnion([Q0])});
            skLineSegment(sketch, "E184.bottom", {"start": v(-102.45, 84.06) * mm, "end": v(-122.45, 84.06) * mm});
            skLineSegment(sketch, "E184.top", {"start": v(-102.45, 94.06) * mm, "end": v(-122.45, 94.06) * mm});
            skLineSegment(sketch, "E184.left", {"start": v(-102.45, 84.06) * mm, "end": v(-102.45, 94.06) * mm});
            skLineSegment(sketch, "E184.right", {"start": v(-122.45, 84.06) * mm, "end": v(-122.45, 94.06) * mm});
            skPoint(sketch, "E184.middle", {"position": v(-112.45, 89.06) * mm});
            skCircle(sketch, "E185", {"center": v(-119.45, 89.06) * mm, "radius": 1 * mm});
            skPoint(sketch, "E185.centerSnap0", {"position": v(-122.45, 89.06) * mm});
            skCircle(sketch, "E186", {"center": v(-105.45, 89.06) * mm, "radius": 1 * mm});
            skSolve(sketch);
        }
        {
            var Q0;
            Q0=makeQuery(id+"F44.imprint","IMPRINT",FACE,{"disambiguationData":[TD([[makeQuery(id+"F44.imprint","IMPRINT",EDGE,{"derivedFrom":sQuery(id+"F44.wireOp",EDGE,"E184.bottom")}),-1.0]])]});
            extrude(context, id + "F45", {"entities" : qUnion([Q0]), "operationType" : NewBodyOperationType.ADD, "oppositeDirection" : true, "depth" : 2 * mm});
        }
        {
            var Q0;
            Q0=makeQuery(id+"F3.opExtrude","CAP_FACE",FACE,{"disambiguationData":[OSD([sQuery(id+"F0.wireOp",EDGE,"E0.bottom"),sQuery(id+"F0.wireOp",EDGE,"E0.top"),sQuery(id+"F0.wireOp",EDGE,"E0.left"),sQuery(id+"F0.wireOp",EDGE,"E0.right"),sQuery(id+"F0.wireOp",EDGE,"6XQCNLW2-68Wz-nC9p-wT4x-b90YEvEmSNLj"),sQuery(id+"F0.wireOp",EDGE,"E3"),sQuery(id+"F0.wireOp",EDGE,"E4"),sQuery(id+"F0.wireOp",EDGE,"E7"),sQuery(id+"F0.wireOp",EDGE,"E8"),sQuery(id+"F0.wireOp",EDGE,"E9"),sQuery(id+"F0.wireOp",EDGE,"E10"),sQuery(id+"F0.wireOp",EDGE,"E11"),sQuery(id+"F0.wireOp",EDGE,"E12"),sQuery(id+"F0.wireOp",EDGE,"E13"),sQuery(id+"F0.wireOp",EDGE,"E14.bottom"),sQuery(id+"F0.wireOp",EDGE,"E14.top"),sQuery(id+"F0.wireOp",EDGE,"E14.left"),sQuery(id+"F0.wireOp",EDGE,"E14.right"),sQuery(id+"F0.wireOp",EDGE,"E15"),sQuery(id+"F0.wireOp",EDGE,"E16"),sQuery(id+"F0.wireOp",EDGE,"E18.bottom"),sQuery(id+"F0.wireOp",EDGE,"E18.top"),sQuery(id+"F0.wireOp",EDGE,"E18.left"),sQuery(id+"F0.wireOp",EDGE,"E18.right"),sQuery(id+"F0.wireOp",EDGE,"E20.bottom"),sQuery(id+"F0.wireOp",EDGE,"E20.top"),sQuery(id+"F0.wireOp",EDGE,"E21.left"),sQuery(id+"F0.wireOp",EDGE,"E21.right"),sQuery(id+"F0.wireOp",EDGE,"E22.left"),sQuery(id+"F0.wireOp",EDGE,"E22.right"),sQuery(id+"F0.wireOp",EDGE,"E23.trimOffspring"),sQuery(id+"F0.wireOp",EDGE,"E24.trimOffspring"),sQuery(id+"F0.wireOp",EDGE,"E25.trimOffspring"),sQuery(id+"F0.wireOp",EDGE,"E26.trimOffspring"),sQuery(id+"F0.wireOp",EDGE,"E27.trimOffspring"),sQuery(id+"F0.wireOp",EDGE,"E28.trimOffspring"),sQuery(id+"F0.wireOp",EDGE,"E29.trimOffspring"),sQuery(id+"F0.wireOp",EDGE,"E30.trimOffspring"),sQuery(id+"F0.wireOp",EDGE,"E19.bottom"),sQuery(id+"F0.wireOp",EDGE,"E19.top"),sQuery(id+"F0.wireOp",EDGE,"E19.left"),sQuery(id+"F0.wireOp",EDGE,"E19.right"),sQuery(id+"F0.wireOp",EDGE,"E31.bottom"),sQuery(id+"F0.wireOp",EDGE,"E31.top"),sQuery(id+"F0.wireOp",EDGE,"E32.left"),sQuery(id+"F0.wireOp",EDGE,"E32.right"),sQuery(id+"F0.wireOp",EDGE,"E33.left"),sQuery(id+"F0.wireOp",EDGE,"E33.right"),sQuery(id+"F0.wireOp",EDGE,"E34.trimOffspring"),sQuery(id+"F0.wireOp",EDGE,"E35.trimOffspring"),sQuery(id+"F0.wireOp",EDGE,"E36.trimOffspring"),sQuery(id+"F0.wireOp",EDGE,"E37.trimOffspring"),sQuery(id+"F0.wireOp",EDGE,"E38.trimOffspring"),sQuery(id+"F0.wireOp",EDGE,"E39.trimOffspring"),sQuery(id+"F0.wireOp",EDGE,"E40.trimOffspring"),sQuery(id+"F0.wireOp",EDGE,"E41.trimOffspring"),sQuery(id+"F0.wireOp",EDGE,"E44.left"),sQuery(id+"F0.wireOp",EDGE,"E44.right"),sQuery(id+"F0.wireOp",EDGE,"E45.left"),sQuery(id+"F0.wireOp",EDGE,"E45.right"),sQuery(id+"F0.wireOp",EDGE,"E46"),sQuery(id+"F0.wireOp",EDGE,"E47"),sQuery(id+"F0.wireOp",EDGE,"E48"),sQuery(id+"F0.wireOp",EDGE,"E49"),sQuery(id+"F0.wireOp",EDGE,"E50.1.0.8"),sQuery(id+"F0.wireOp",EDGE,"E50.1.0.22"),sQuery(id+"F0.wireOp",EDGE,"E50.1.0.29"),sQuery(id+"F0.wireOp",EDGE,"E50.1.0.40"),sQuery(id+"F0.wireOp",EDGE,"E50.1.0.46"),sQuery(id+"F0.wireOp",EDGE,"E50.1.0.47"),sQuery(id+"F0.wireOp",EDGE,"E50.1.0.48"),sQuery(id+"F0.wireOp",EDGE,"E50.1.0.52"),sQuery(id+"F0.wireOp",EDGE,"E50.1.0.54"),sQuery(id+"F0.wireOp",EDGE,"E50.1.0.55"),sQuery(id+"F0.wireOp",EDGE,"E50.1.0.56"),sQuery(id+"F0.wireOp",EDGE,"E50.1.0.57"),sQuery(id+"F0.wireOp",EDGE,"E50.1.0.58"),sQuery(id+"F0.wireOp",EDGE,"E50.1.0.59"),sQuery(id+"F0.wireOp",EDGE,"E50.1.0.61"),sQuery(id+"F0.wireOp",EDGE,"E50.1.0.64"),sQuery(id+"F0.wireOp",EDGE,"E50.1.0.65"),sQuery(id+"F0.wireOp",EDGE,"E50.1.0.67"),sQuery(id+"F0.wireOp",EDGE,"E50.1.0.68"),sQuery(id+"F0.wireOp",EDGE,"E50.1.0.70"),sQuery(id+"F0.wireOp",EDGE,"E50.2.0.8"),sQuery(id+"F0.wireOp",EDGE,"E50.2.0.22"),sQuery(id+"F0.wireOp",EDGE,"E50.2.0.29"),sQuery(id+"F0.wireOp",EDGE,"E50.2.0.40"),sQuery(id+"F0.wireOp",EDGE,"E50.2.0.46"),sQuery(id+"F0.wireOp",EDGE,"E50.2.0.47"),sQuery(id+"F0.wireOp",EDGE,"E50.2.0.48"),sQuery(id+"F0.wireOp",EDGE,"E50.2.0.52"),sQuery(id+"F0.wireOp",EDGE,"E50.2.0.54"),sQuery(id+"F0.wireOp",EDGE,"E50.2.0.55"),sQuery(id+"F0.wireOp",EDGE,"E50.2.0.56"),sQuery(id+"F0.wireOp",EDGE,"E50.2.0.57"),sQuery(id+"F0.wireOp",EDGE,"E50.2.0.58"),sQuery(id+"F0.wireOp",EDGE,"E50.2.0.59"),sQuery(id+"F0.wireOp",EDGE,"E50.2.0.61"),sQuery(id+"F0.wireOp",EDGE,"E50.2.0.64"),sQuery(id+"F0.wireOp",EDGE,"E50.2.0.65"),sQuery(id+"F0.wireOp",EDGE,"E50.2.0.67"),sQuery(id+"F0.wireOp",EDGE,"E50.2.0.68"),sQuery(id+"F0.wireOp",EDGE,"E50.2.0.70"),sQuery(id+"F0.wireOp",EDGE,"E51"),sQuery(id+"F0.wireOp",EDGE,"E52")])],"isStart":false});
            var sketch = newSketch(context, id + "F46", { "sketchPlane" : qUnion([Q0])});
            skLineSegment(sketch, "E187.left", {"start": v(-114.5, -48.28) * mm, "end": v(-114.5, -39.8) * mm});
            skLineSegment(sketch, "E187.right", {"start": v(-117.5, -48.28) * mm, "end": v(-117.5, -39.8) * mm});
            skPoint(sketch, "E187.middle", {"position": v(-116, -44.04) * mm});
            skLineSegment(sketch, "E188.left", {"start": v(-74.5, -48.28) * mm, "end": v(-74.5, -39.8) * mm});
            skLineSegment(sketch, "E188.right", {"start": v(-77.5, -48.28) * mm, "end": v(-77.5, -39.8) * mm});
            skPoint(sketch, "E188.middle", {"position": v(-76, -44.04) * mm});
            skLineSegment(sketch, "E189.left", {"start": v(-45.5, -48.28) * mm, "end": v(-45.5, -39.8) * mm});
            skLineSegment(sketch, "E189.right", {"start": v(-48.5, -48.28) * mm, "end": v(-48.5, -39.8) * mm});
            skPoint(sketch, "E189.middle", {"position": v(-47, -44.04) * mm});
            skLineSegment(sketch, "E190.left", {"start": v(-32.5, -48.28) * mm, "end": v(-32.5, -39.8) * mm});
            skLineSegment(sketch, "E190.right", {"start": v(-35.5, -48.28) * mm, "end": v(-35.5, -39.8) * mm});
            skPoint(sketch, "E190.middle", {"position": v(-34, -44.04) * mm});
            skSolve(sketch);
        }
        {
            var Q0;
            {var subQ0=sQuery(id+"F46.wireOp",EDGE,"E187.left");Q0=makeQuery(id+"F46.imprint","IMPRINT",FACE,{"disambiguationData":[TD([[makeQuery(id+"F46.imprint","IMPRINT",EDGE,{"derivedFrom":subQ0}),1.0]])]});}
            var Q1;
            {var subQ0=sQuery(id+"F46.wireOp",EDGE,"E188.left");Q1=makeQuery(id+"F46.imprint","IMPRINT",FACE,{"disambiguationData":[TD([[makeQuery(id+"F46.imprint","IMPRINT",EDGE,{"derivedFrom":subQ0}),1.0]])]});}
            var Q2;
            {var subQ0=sQuery(id+"F46.wireOp",EDGE,"E189.left");Q2=makeQuery(id+"F46.imprint","IMPRINT",FACE,{"disambiguationData":[TD([[makeQuery(id+"F46.imprint","IMPRINT",EDGE,{"derivedFrom":subQ0}),1.0]])]});}
            var Q3;
            {var subQ0=sQuery(id+"F46.wireOp",EDGE,"E190.left");Q3=makeQuery(id+"F46.imprint","IMPRINT",FACE,{"disambiguationData":[TD([[makeQuery(id+"F46.imprint","IMPRINT",EDGE,{"derivedFrom":subQ0}),1.0]])]});}
            extrude(context, id + "F47", {"entities" : qUnion([Q0, Q1, Q2, Q3]), "operationType" : NewBodyOperationType.ADD, "oppositeDirection" : true, "depth" : 1 * mm});
        }
        {
            var Q0;
            Q0=makeQuery(id+"F23.opExtrude","CAP_FACE",FACE,{"disambiguationData":[OSD([sQuery(id+"F1.wireOp",EDGE,"E73.bottom"),sQuery(id+"F1.wireOp",EDGE,"E73.top"),sQuery(id+"F1.wireOp",EDGE,"E73.left"),sQuery(id+"F1.wireOp",EDGE,"E73.right"),sQuery(id+"F1.wireOp",EDGE,"E74.bottom"),sQuery(id+"F1.wireOp",EDGE,"E74.top"),sQuery(id+"F1.wireOp",EDGE,"E74.left"),sQuery(id+"F1.wireOp",EDGE,"E74.right"),sQuery(id+"F1.wireOp",EDGE,"E75.bottom"),sQuery(id+"F1.wireOp",EDGE,"E75.top"),sQuery(id+"F1.wireOp",EDGE,"E75.left"),sQuery(id+"F1.wireOp",EDGE,"E75.right"),sQuery(id+"F1.wireOp",EDGE,"E80"),sQuery(id+"F1.wireOp",EDGE,"E81"),sQuery(id+"F1.wireOp",EDGE,"E83"),sQuery(id+"F1.wireOp",EDGE,"E84"),sQuery(id+"F1.wireOp",EDGE,"E87.bottom"),sQuery(id+"F1.wireOp",EDGE,"E87.top"),sQuery(id+"F1.wireOp",EDGE,"E87.left"),sQuery(id+"F1.wireOp",EDGE,"E87.right"),sQuery(id+"F1.wireOp",EDGE,"E89"),sQuery(id+"F1.wireOp",EDGE,"E92"),sQuery(id+"F1.wireOp",EDGE,"E93"),sQuery(id+"F1.wireOp",EDGE,"CoPGjB9w-zRhk-UiIu-dCG4-BhNkDkZw4NkV"),sQuery(id+"F1.wireOp",EDGE,"XJoTFQyA-9xYx-y9zl-Xs7Z-xe6QLGOleBae"),sQuery(id+"F1.wireOp",EDGE,"E94"),sQuery(id+"F1.wireOp",EDGE,"E95"),sQuery(id+"F1.wireOp",EDGE,"E96"),sQuery(id+"F1.wireOp",EDGE,"E97"),sQuery(id+"F1.wireOp",EDGE,"E98"),sQuery(id+"F1.wireOp",EDGE,"E99"),sQuery(id+"F1.wireOp",EDGE,"E100"),sQuery(id+"F1.wireOp",EDGE,"E101"),sQuery(id+"F1.wireOp",EDGE,"E102"),sQuery(id+"F1.wireOp",EDGE,"E105.1.0.0"),sQuery(id+"F1.wireOp",EDGE,"E105.1.0.1"),sQuery(id+"F1.wireOp",EDGE,"E105.1.0.2"),sQuery(id+"F1.wireOp",EDGE,"E105.1.0.3"),sQuery(id+"F1.wireOp",EDGE,"E105.2.0.0"),sQuery(id+"F1.wireOp",EDGE,"E105.2.0.1"),sQuery(id+"F1.wireOp",EDGE,"E105.2.0.2"),sQuery(id+"F1.wireOp",EDGE,"E105.2.0.3"),sQuery(id+"F1.wireOp",EDGE,"E106.1.0.0"),sQuery(id+"F1.wireOp",EDGE,"E106.1.0.1"),sQuery(id+"F1.wireOp",EDGE,"E106.1.0.2"),sQuery(id+"F1.wireOp",EDGE,"E106.1.0.3"),sQuery(id+"F1.wireOp",EDGE,"E106.2.0.0"),sQuery(id+"F1.wireOp",EDGE,"E106.2.0.1"),sQuery(id+"F1.wireOp",EDGE,"E106.2.0.2"),sQuery(id+"F1.wireOp",EDGE,"E106.2.0.3")])],"isStart":true});
            var sketch = newSketch(context, id + "F48", { "sketchPlane" : qUnion([Q0])});
            skLineSegment(sketch, "E191.bottom", {"start": v(60.16, 138.23) * mm, "end": v(48.16, 138.23) * mm});
            skLineSegment(sketch, "E191.top", {"start": v(60.16, 118.23) * mm, "end": v(48.16, 118.23) * mm});
            skLineSegment(sketch, "E191.left", {"start": v(60.16, 138.23) * mm, "end": v(60.16, 118.23) * mm});
            skLineSegment(sketch, "E191.right", {"start": v(48.16, 138.23) * mm, "end": v(48.16, 118.23) * mm});
            skLineSegment(sketch, "E192.0", {"start": v(59.66, 137.73) * mm, "end": v(59.66, 118.73) * mm});
            skLineSegment(sketch, "E192.1", {"start": v(59.66, 137.73) * mm, "end": v(48.66, 137.73) * mm});
            skLineSegment(sketch, "E192.2", {"start": v(48.66, 137.73) * mm, "end": v(48.66, 118.73) * mm});
            skLineSegment(sketch, "E192.3", {"start": v(59.66, 118.73) * mm, "end": v(48.66, 118.73) * mm});
            skSolve(sketch);
        }
        {
            var Q0;
            Q0=qSketchRegion(id+"F48",true);
            extrude(context, id + "F49", {"entities" : qUnion([Q0]), "operationType" : NewBodyOperationType.ADD, "oppositeDirection" : true, "depth" : 1 * mm});
        }
        {
            var Q0;
            {var subQ0=sQuery(id+"F0.wireOp",EDGE,"E11");var subQ1=sQuery(id+"F0.wireOp",EDGE,"E10");var subQ2=sQuery(id+"F0.wireOp",EDGE,"E8");var subQ3=sQuery(id+"F0.wireOp",EDGE,"E7");Q0=makeQuery(id+"F47.boolean.opBoolean","MERGE",FACE,{"derivedFrom":[makeQuery(id+"F3.opExtrude","CAP_FACE",FACE,{"disambiguationData":[OSD([sQuery(id+"F0.wireOp",EDGE,"E0.bottom"),sQuery(id+"F0.wireOp",EDGE,"E0.top"),sQuery(id+"F0.wireOp",EDGE,"E0.left"),sQuery(id+"F0.wireOp",EDGE,"E0.right"),sQuery(id+"F0.wireOp",EDGE,"6XQCNLW2-68Wz-nC9p-wT4x-b90YEvEmSNLj"),sQuery(id+"F0.wireOp",EDGE,"E3"),sQuery(id+"F0.wireOp",EDGE,"E4"),subQ3,subQ2,sQuery(id+"F0.wireOp",EDGE,"E9"),subQ1,subQ0,sQuery(id+"F0.wireOp",EDGE,"E12"),sQuery(id+"F0.wireOp",EDGE,"E13"),sQuery(id+"F0.wireOp",EDGE,"E14.bottom"),sQuery(id+"F0.wireOp",EDGE,"E14.top"),sQuery(id+"F0.wireOp",EDGE,"E14.left"),sQuery(id+"F0.wireOp",EDGE,"E14.right"),sQuery(id+"F0.wireOp",EDGE,"E15"),sQuery(id+"F0.wireOp",EDGE,"E16"),sQuery(id+"F0.wireOp",EDGE,"E18.bottom"),sQuery(id+"F0.wireOp",EDGE,"E18.top"),sQuery(id+"F0.wireOp",EDGE,"E18.left"),sQuery(id+"F0.wireOp",EDGE,"E18.right"),sQuery(id+"F0.wireOp",EDGE,"E20.bottom"),sQuery(id+"F0.wireOp",EDGE,"E20.top"),sQuery(id+"F0.wireOp",EDGE,"E21.left"),sQuery(id+"F0.wireOp",EDGE,"E21.right"),sQuery(id+"F0.wireOp",EDGE,"E22.left"),sQuery(id+"F0.wireOp",EDGE,"E22.right"),sQuery(id+"F0.wireOp",EDGE,"E23.trimOffspring"),sQuery(id+"F0.wireOp",EDGE,"E24.trimOffspring"),sQuery(id+"F0.wireOp",EDGE,"E25.trimOffspring"),sQuery(id+"F0.wireOp",EDGE,"E26.trimOffspring"),sQuery(id+"F0.wireOp",EDGE,"E27.trimOffspring"),sQuery(id+"F0.wireOp",EDGE,"E28.trimOffspring"),sQuery(id+"F0.wireOp",EDGE,"E29.trimOffspring"),sQuery(id+"F0.wireOp",EDGE,"E30.trimOffspring"),sQuery(id+"F0.wireOp",EDGE,"E19.bottom"),sQuery(id+"F0.wireOp",EDGE,"E19.top"),sQuery(id+"F0.wireOp",EDGE,"E19.left"),sQuery(id+"F0.wireOp",EDGE,"E19.right"),sQuery(id+"F0.wireOp",EDGE,"E31.bottom"),sQuery(id+"F0.wireOp",EDGE,"E31.top"),sQuery(id+"F0.wireOp",EDGE,"E32.left"),sQuery(id+"F0.wireOp",EDGE,"E32.right"),sQuery(id+"F0.wireOp",EDGE,"E33.left"),sQuery(id+"F0.wireOp",EDGE,"E33.right"),sQuery(id+"F0.wireOp",EDGE,"E34.trimOffspring"),sQuery(id+"F0.wireOp",EDGE,"E35.trimOffspring"),sQuery(id+"F0.wireOp",EDGE,"E36.trimOffspring"),sQuery(id+"F0.wireOp",EDGE,"E37.trimOffspring"),sQuery(id+"F0.wireOp",EDGE,"E38.trimOffspring"),sQuery(id+"F0.wireOp",EDGE,"E39.trimOffspring"),sQuery(id+"F0.wireOp",EDGE,"E40.trimOffspring"),sQuery(id+"F0.wireOp",EDGE,"E41.trimOffspring"),sQuery(id+"F0.wireOp",EDGE,"E44.left"),sQuery(id+"F0.wireOp",EDGE,"E44.right"),sQuery(id+"F0.wireOp",EDGE,"E45.left"),sQuery(id+"F0.wireOp",EDGE,"E45.right"),sQuery(id+"F0.wireOp",EDGE,"E46"),sQuery(id+"F0.wireOp",EDGE,"E47"),sQuery(id+"F0.wireOp",EDGE,"E48"),sQuery(id+"F0.wireOp",EDGE,"E49"),sQuery(id+"F0.wireOp",EDGE,"E50.1.0.0"),sQuery(id+"F0.wireOp",EDGE,"E50.1.0.1"),sQuery(id+"F0.wireOp",EDGE,"E50.1.0.2"),sQuery(id+"F0.wireOp",EDGE,"E50.1.0.3"),sQuery(id+"F0.wireOp",EDGE,"E50.1.0.8"),sQuery(id+"F0.wireOp",EDGE,"E50.1.0.9"),sQuery(id+"F0.wireOp",EDGE,"E50.1.0.10"),sQuery(id+"F0.wireOp",EDGE,"E50.1.0.11"),sQuery(id+"F0.wireOp",EDGE,"E50.1.0.12"),sQuery(id+"F0.wireOp",EDGE,"E50.1.0.13"),sQuery(id+"F0.wireOp",EDGE,"E50.1.0.14"),sQuery(id+"F0.wireOp",EDGE,"E50.1.0.15"),sQuery(id+"F0.wireOp",EDGE,"E50.1.0.16"),sQuery(id+"F0.wireOp",EDGE,"E50.1.0.18"),sQuery(id+"F0.wireOp",EDGE,"E50.1.0.19"),sQuery(id+"F0.wireOp",EDGE,"E50.1.0.21"),sQuery(id+"F0.wireOp",EDGE,"E50.1.0.22"),sQuery(id+"F0.wireOp",EDGE,"E50.1.0.25"),sQuery(id+"F0.wireOp",EDGE,"E50.1.0.27"),sQuery(id+"F0.wireOp",EDGE,"E50.1.0.29"),sQuery(id+"F0.wireOp",EDGE,"E50.1.0.31"),sQuery(id+"F0.wireOp",EDGE,"E50.1.0.32"),sQuery(id+"F0.wireOp",EDGE,"E50.1.0.33"),sQuery(id+"F0.wireOp",EDGE,"E50.1.0.34"),sQuery(id+"F0.wireOp",EDGE,"E50.1.0.36"),sQuery(id+"F0.wireOp",EDGE,"E50.1.0.37"),sQuery(id+"F0.wireOp",EDGE,"E50.1.0.38"),sQuery(id+"F0.wireOp",EDGE,"E50.1.0.40"),sQuery(id+"F0.wireOp",EDGE,"E50.1.0.41"),sQuery(id+"F0.wireOp",EDGE,"E50.1.0.44"),sQuery(id+"F0.wireOp",EDGE,"E50.1.0.45"),sQuery(id+"F0.wireOp",EDGE,"E50.1.0.46"),sQuery(id+"F0.wireOp",EDGE,"E50.1.0.47"),sQuery(id+"F0.wireOp",EDGE,"E50.1.0.48"),sQuery(id+"F0.wireOp",EDGE,"E50.1.0.51"),sQuery(id+"F0.wireOp",EDGE,"E50.1.0.52"),sQuery(id+"F0.wireOp",EDGE,"E50.2.0.0"),sQuery(id+"F0.wireOp",EDGE,"E50.2.0.1"),sQuery(id+"F0.wireOp",EDGE,"E50.2.0.2"),sQuery(id+"F0.wireOp",EDGE,"E50.2.0.3"),sQuery(id+"F0.wireOp",EDGE,"E50.2.0.8"),sQuery(id+"F0.wireOp",EDGE,"E50.2.0.9"),sQuery(id+"F0.wireOp",EDGE,"E50.2.0.10"),sQuery(id+"F0.wireOp",EDGE,"E50.2.0.11"),sQuery(id+"F0.wireOp",EDGE,"E50.2.0.12"),sQuery(id+"F0.wireOp",EDGE,"E50.2.0.13"),sQuery(id+"F0.wireOp",EDGE,"E50.2.0.14"),sQuery(id+"F0.wireOp",EDGE,"E50.2.0.15"),sQuery(id+"F0.wireOp",EDGE,"E50.2.0.16"),sQuery(id+"F0.wireOp",EDGE,"E50.2.0.18"),sQuery(id+"F0.wireOp",EDGE,"E50.2.0.19"),sQuery(id+"F0.wireOp",EDGE,"E50.2.0.21"),sQuery(id+"F0.wireOp",EDGE,"E50.2.0.22"),sQuery(id+"F0.wireOp",EDGE,"E50.2.0.25"),sQuery(id+"F0.wireOp",EDGE,"E50.2.0.27"),sQuery(id+"F0.wireOp",EDGE,"E50.2.0.29"),sQuery(id+"F0.wireOp",EDGE,"E50.2.0.31"),sQuery(id+"F0.wireOp",EDGE,"E50.2.0.32"),sQuery(id+"F0.wireOp",EDGE,"E50.2.0.33"),sQuery(id+"F0.wireOp",EDGE,"E50.2.0.34"),sQuery(id+"F0.wireOp",EDGE,"E50.2.0.36"),sQuery(id+"F0.wireOp",EDGE,"E50.2.0.37"),sQuery(id+"F0.wireOp",EDGE,"E50.2.0.38"),sQuery(id+"F0.wireOp",EDGE,"E50.2.0.40"),sQuery(id+"F0.wireOp",EDGE,"E50.2.0.41"),sQuery(id+"F0.wireOp",EDGE,"E50.2.0.44"),sQuery(id+"F0.wireOp",EDGE,"E50.2.0.45"),sQuery(id+"F0.wireOp",EDGE,"E50.2.0.46"),sQuery(id+"F0.wireOp",EDGE,"E50.2.0.47"),sQuery(id+"F0.wireOp",EDGE,"E50.2.0.48"),sQuery(id+"F0.wireOp",EDGE,"E50.2.0.51"),sQuery(id+"F0.wireOp",EDGE,"E50.2.0.52"),sQuery(id+"F0.wireOp",EDGE,"E51"),sQuery(id+"F0.wireOp",EDGE,"E52"),sQuery(id+"F0.wireOp",EDGE,"E53.left"),sQuery(id+"F0.wireOp",EDGE,"E53.right")])],"isStart":false}),makeQuery(id+"F47.opExtrude","CAP_FACE",FACE,{"disambiguationData":[OSD([subQ3,sQuery(id+"F46.wireOp",EDGE,"E187.left"),sQuery(id+"F46.wireOp",EDGE,"E187.right")])],"isStart":true}),makeQuery(id+"F47.opExtrude","CAP_FACE",FACE,{"disambiguationData":[OSD([subQ2,sQuery(id+"F46.wireOp",EDGE,"E188.left"),sQuery(id+"F46.wireOp",EDGE,"E188.right")])],"isStart":true}),makeQuery(id+"F47.opExtrude","CAP_FACE",FACE,{"disambiguationData":[OSD([subQ1,sQuery(id+"F46.wireOp",EDGE,"E189.left"),sQuery(id+"F46.wireOp",EDGE,"E189.right")])],"isStart":true}),makeQuery(id+"F47.opExtrude","CAP_FACE",FACE,{"disambiguationData":[OSD([subQ0,sQuery(id+"F46.wireOp",EDGE,"E190.left"),sQuery(id+"F46.wireOp",EDGE,"E190.right")])],"isStart":true})]});}
            var sketch = newSketch(context, id + "F50", { "sketchPlane" : qUnion([Q0])});
            skLineSegment(sketch, "E193.bottom", {"start": v(-40, -8.04) * mm, "end": v(-28, -8.04) * mm});
            skLineSegment(sketch, "E193.top", {"start": v(-40, 11.96) * mm, "end": v(-28, 11.96) * mm});
            skLineSegment(sketch, "E193.left", {"start": v(-40, -8.04) * mm, "end": v(-40, 11.96) * mm});
            skLineSegment(sketch, "E193.right", {"start": v(-28, -8.04) * mm, "end": v(-28, 11.96) * mm});
            skSolve(sketch);
        }
        {
            var Q0;
            Q0=qSketchRegion(id+"F50",true);
            extrude(context, id + "F51", {"entities" : qUnion([Q0]), "operationType" : NewBodyOperationType.REMOVE, "oppositeDirection" : true, "depth" : 3 * mm});
        }
        {
            var Q0;
            {var subQ0=sQuery(id+"F0.wireOp",EDGE,"E11");var subQ1=sQuery(id+"F0.wireOp",EDGE,"E10");var subQ2=sQuery(id+"F0.wireOp",EDGE,"E8");var subQ3=sQuery(id+"F0.wireOp",EDGE,"E7");Q0=makeQuery(id+"F47.boolean.opBoolean","MERGE",FACE,{"derivedFrom":[makeQuery(id+"F3.opExtrude","CAP_FACE",FACE,{"disambiguationData":[OSD([sQuery(id+"F0.wireOp",EDGE,"E0.bottom"),sQuery(id+"F0.wireOp",EDGE,"E0.top"),sQuery(id+"F0.wireOp",EDGE,"E0.left"),sQuery(id+"F0.wireOp",EDGE,"E0.right"),sQuery(id+"F0.wireOp",EDGE,"6XQCNLW2-68Wz-nC9p-wT4x-b90YEvEmSNLj"),sQuery(id+"F0.wireOp",EDGE,"E3"),sQuery(id+"F0.wireOp",EDGE,"E4"),subQ3,subQ2,sQuery(id+"F0.wireOp",EDGE,"E9"),subQ1,subQ0,sQuery(id+"F0.wireOp",EDGE,"E12"),sQuery(id+"F0.wireOp",EDGE,"E13"),sQuery(id+"F0.wireOp",EDGE,"E14.bottom"),sQuery(id+"F0.wireOp",EDGE,"E14.top"),sQuery(id+"F0.wireOp",EDGE,"E14.left"),sQuery(id+"F0.wireOp",EDGE,"E14.right"),sQuery(id+"F0.wireOp",EDGE,"E15"),sQuery(id+"F0.wireOp",EDGE,"E18.bottom"),sQuery(id+"F0.wireOp",EDGE,"E18.top"),sQuery(id+"F0.wireOp",EDGE,"E18.left"),sQuery(id+"F0.wireOp",EDGE,"E18.right"),sQuery(id+"F0.wireOp",EDGE,"E20.bottom"),sQuery(id+"F0.wireOp",EDGE,"E20.top"),sQuery(id+"F0.wireOp",EDGE,"E21.left"),sQuery(id+"F0.wireOp",EDGE,"E21.right"),sQuery(id+"F0.wireOp",EDGE,"E22.left"),sQuery(id+"F0.wireOp",EDGE,"E22.right"),sQuery(id+"F0.wireOp",EDGE,"E23.trimOffspring"),sQuery(id+"F0.wireOp",EDGE,"E24.trimOffspring"),sQuery(id+"F0.wireOp",EDGE,"E25.trimOffspring"),sQuery(id+"F0.wireOp",EDGE,"E26.trimOffspring"),sQuery(id+"F0.wireOp",EDGE,"E27.trimOffspring"),sQuery(id+"F0.wireOp",EDGE,"E28.trimOffspring"),sQuery(id+"F0.wireOp",EDGE,"E29.trimOffspring"),sQuery(id+"F0.wireOp",EDGE,"E30.trimOffspring"),sQuery(id+"F0.wireOp",EDGE,"E19.bottom"),sQuery(id+"F0.wireOp",EDGE,"E19.top"),sQuery(id+"F0.wireOp",EDGE,"E19.left"),sQuery(id+"F0.wireOp",EDGE,"E19.right"),sQuery(id+"F0.wireOp",EDGE,"E31.bottom"),sQuery(id+"F0.wireOp",EDGE,"E31.top"),sQuery(id+"F0.wireOp",EDGE,"E32.left"),sQuery(id+"F0.wireOp",EDGE,"E32.right"),sQuery(id+"F0.wireOp",EDGE,"E33.left"),sQuery(id+"F0.wireOp",EDGE,"E33.right"),sQuery(id+"F0.wireOp",EDGE,"E34.trimOffspring"),sQuery(id+"F0.wireOp",EDGE,"E35.trimOffspring"),sQuery(id+"F0.wireOp",EDGE,"E36.trimOffspring"),sQuery(id+"F0.wireOp",EDGE,"E37.trimOffspring"),sQuery(id+"F0.wireOp",EDGE,"E38.trimOffspring"),sQuery(id+"F0.wireOp",EDGE,"E39.trimOffspring"),sQuery(id+"F0.wireOp",EDGE,"E40.trimOffspring"),sQuery(id+"F0.wireOp",EDGE,"E41.trimOffspring"),sQuery(id+"F0.wireOp",EDGE,"E44.left"),sQuery(id+"F0.wireOp",EDGE,"E44.right"),sQuery(id+"F0.wireOp",EDGE,"E45.left"),sQuery(id+"F0.wireOp",EDGE,"E45.right"),sQuery(id+"F0.wireOp",EDGE,"E46"),sQuery(id+"F0.wireOp",EDGE,"E47"),sQuery(id+"F0.wireOp",EDGE,"E48"),sQuery(id+"F0.wireOp",EDGE,"E49"),sQuery(id+"F0.wireOp",EDGE,"E50.1.0.0"),sQuery(id+"F0.wireOp",EDGE,"E50.1.0.1"),sQuery(id+"F0.wireOp",EDGE,"E50.1.0.2"),sQuery(id+"F0.wireOp",EDGE,"E50.1.0.3"),sQuery(id+"F0.wireOp",EDGE,"E50.1.0.8"),sQuery(id+"F0.wireOp",EDGE,"E50.1.0.9"),sQuery(id+"F0.wireOp",EDGE,"E50.1.0.10"),sQuery(id+"F0.wireOp",EDGE,"E50.1.0.11"),sQuery(id+"F0.wireOp",EDGE,"E50.1.0.12"),sQuery(id+"F0.wireOp",EDGE,"E50.1.0.13"),sQuery(id+"F0.wireOp",EDGE,"E50.1.0.14"),sQuery(id+"F0.wireOp",EDGE,"E50.1.0.15"),sQuery(id+"F0.wireOp",EDGE,"E50.1.0.16"),sQuery(id+"F0.wireOp",EDGE,"E50.1.0.18"),sQuery(id+"F0.wireOp",EDGE,"E50.1.0.19"),sQuery(id+"F0.wireOp",EDGE,"E50.1.0.21"),sQuery(id+"F0.wireOp",EDGE,"E50.1.0.22"),sQuery(id+"F0.wireOp",EDGE,"E50.1.0.25"),sQuery(id+"F0.wireOp",EDGE,"E50.1.0.27"),sQuery(id+"F0.wireOp",EDGE,"E50.1.0.29"),sQuery(id+"F0.wireOp",EDGE,"E50.1.0.31"),sQuery(id+"F0.wireOp",EDGE,"E50.1.0.32"),sQuery(id+"F0.wireOp",EDGE,"E50.1.0.33"),sQuery(id+"F0.wireOp",EDGE,"E50.1.0.34"),sQuery(id+"F0.wireOp",EDGE,"E50.1.0.36"),sQuery(id+"F0.wireOp",EDGE,"E50.1.0.37"),sQuery(id+"F0.wireOp",EDGE,"E50.1.0.38"),sQuery(id+"F0.wireOp",EDGE,"E50.1.0.40"),sQuery(id+"F0.wireOp",EDGE,"E50.1.0.41"),sQuery(id+"F0.wireOp",EDGE,"E50.1.0.44"),sQuery(id+"F0.wireOp",EDGE,"E50.1.0.45"),sQuery(id+"F0.wireOp",EDGE,"E50.1.0.46"),sQuery(id+"F0.wireOp",EDGE,"E50.1.0.47"),sQuery(id+"F0.wireOp",EDGE,"E50.1.0.48"),sQuery(id+"F0.wireOp",EDGE,"E50.1.0.51"),sQuery(id+"F0.wireOp",EDGE,"E50.1.0.52"),sQuery(id+"F0.wireOp",EDGE,"E50.2.0.0"),sQuery(id+"F0.wireOp",EDGE,"E50.2.0.1"),sQuery(id+"F0.wireOp",EDGE,"E50.2.0.2"),sQuery(id+"F0.wireOp",EDGE,"E50.2.0.3"),sQuery(id+"F0.wireOp",EDGE,"E50.2.0.8"),sQuery(id+"F0.wireOp",EDGE,"E50.2.0.9"),sQuery(id+"F0.wireOp",EDGE,"E50.2.0.10"),sQuery(id+"F0.wireOp",EDGE,"E50.2.0.11"),sQuery(id+"F0.wireOp",EDGE,"E50.2.0.12"),sQuery(id+"F0.wireOp",EDGE,"E50.2.0.13"),sQuery(id+"F0.wireOp",EDGE,"E50.2.0.14"),sQuery(id+"F0.wireOp",EDGE,"E50.2.0.15"),sQuery(id+"F0.wireOp",EDGE,"E50.2.0.16"),sQuery(id+"F0.wireOp",EDGE,"E50.2.0.18"),sQuery(id+"F0.wireOp",EDGE,"E50.2.0.19"),sQuery(id+"F0.wireOp",EDGE,"E50.2.0.21"),sQuery(id+"F0.wireOp",EDGE,"E50.2.0.22"),sQuery(id+"F0.wireOp",EDGE,"E50.2.0.25"),sQuery(id+"F0.wireOp",EDGE,"E50.2.0.27"),sQuery(id+"F0.wireOp",EDGE,"E50.2.0.29"),sQuery(id+"F0.wireOp",EDGE,"E50.2.0.31"),sQuery(id+"F0.wireOp",EDGE,"E50.2.0.32"),sQuery(id+"F0.wireOp",EDGE,"E50.2.0.33"),sQuery(id+"F0.wireOp",EDGE,"E50.2.0.34"),sQuery(id+"F0.wireOp",EDGE,"E50.2.0.36"),sQuery(id+"F0.wireOp",EDGE,"E50.2.0.37"),sQuery(id+"F0.wireOp",EDGE,"E50.2.0.38"),sQuery(id+"F0.wireOp",EDGE,"E50.2.0.40"),sQuery(id+"F0.wireOp",EDGE,"E50.2.0.41"),sQuery(id+"F0.wireOp",EDGE,"E50.2.0.44"),sQuery(id+"F0.wireOp",EDGE,"E50.2.0.45"),sQuery(id+"F0.wireOp",EDGE,"E50.2.0.46"),sQuery(id+"F0.wireOp",EDGE,"E50.2.0.47"),sQuery(id+"F0.wireOp",EDGE,"E50.2.0.48"),sQuery(id+"F0.wireOp",EDGE,"E50.2.0.51"),sQuery(id+"F0.wireOp",EDGE,"E50.2.0.52"),sQuery(id+"F0.wireOp",EDGE,"E51"),sQuery(id+"F0.wireOp",EDGE,"E52"),sQuery(id+"F0.wireOp",EDGE,"E53.left"),sQuery(id+"F0.wireOp",EDGE,"E53.right"),sQuery(id+"F0.wireOp",EDGE,"E54.bottom"),sQuery(id+"F0.wireOp",EDGE,"E54.top"),sQuery(id+"F0.wireOp",EDGE,"E54.left"),sQuery(id+"F0.wireOp",EDGE,"E54.right"),sQuery(id+"F0.wireOp",EDGE,"E55.bottom"),sQuery(id+"F0.wireOp",EDGE,"E55.top")])],"isStart":false}),makeQuery(id+"F47.opExtrude","CAP_FACE",FACE,{"disambiguationData":[OSD([subQ3,sQuery(id+"F46.wireOp",EDGE,"E187.left"),sQuery(id+"F46.wireOp",EDGE,"E187.right")])],"isStart":true}),makeQuery(id+"F47.opExtrude","CAP_FACE",FACE,{"disambiguationData":[OSD([subQ2,sQuery(id+"F46.wireOp",EDGE,"E188.left"),sQuery(id+"F46.wireOp",EDGE,"E188.right")])],"isStart":true}),makeQuery(id+"F47.opExtrude","CAP_FACE",FACE,{"disambiguationData":[OSD([subQ1,sQuery(id+"F46.wireOp",EDGE,"E189.left"),sQuery(id+"F46.wireOp",EDGE,"E189.right")])],"isStart":true}),makeQuery(id+"F47.opExtrude","CAP_FACE",FACE,{"disambiguationData":[OSD([subQ0,sQuery(id+"F46.wireOp",EDGE,"E190.left"),sQuery(id+"F46.wireOp",EDGE,"E190.right")])],"isStart":true})]});}
            var sketch = newSketch(context, id + "F52", { "sketchPlane" : qUnion([Q0])});
            skLineSegment(sketch, "E194.bottom", {"start": v(-24.5, -13.04) * mm, "end": v(-10.5, -13.04) * mm});
            skLineSegment(sketch, "E194.top", {"start": v(-24.5, -29.04) * mm, "end": v(-10.5, -29.04) * mm});
            skLineSegment(sketch, "E194.left", {"start": v(-24.5, -13.04) * mm, "end": v(-24.5, -29.04) * mm});
            skLineSegment(sketch, "E194.right", {"start": v(-10.5, -13.04) * mm, "end": v(-10.5, -29.04) * mm});
            skSolve(sketch);
        }
        {
            var Q0;
            Q0=qSketchRegion(id+"F52",true);
            extrude(context, id + "F53", {"entities" : qUnion([Q0]), "operationType" : NewBodyOperationType.REMOVE, "oppositeDirection" : true, "depth" : 5 * mm});
        }
        {
            var Q0;
            Q0=qCreatedBy(makeId("Top.planeOp"),FACE);
            var sketch = newSketch(context, id + "F54", { "sketchPlane" : qUnion([Q0])});
            skLineSegment(sketch, "E195.bottom", {"start": v(-122.3, 89.38) * mm, "end": v(-140.3, 89.38) * mm});
            skLineSegment(sketch, "E195.top", {"start": v(-122.3, 107.38) * mm, "end": v(-140.3, 107.38) * mm});
            skLineSegment(sketch, "E195.left", {"start": v(-122.3, 89.38) * mm, "end": v(-122.3, 107.38) * mm});
            skLineSegment(sketch, "E195.right", {"start": v(-140.3, 89.38) * mm, "end": v(-140.3, 107.38) * mm});
            skPoint(sketch, "E195.middle", {"position": v(-131.3, 98.38) * mm});
            skLineSegment(sketch, "E196.bottom", {"start": v(57.55, -103.78) * mm, "end": v(45.75, -103.78) * mm});
            skLineSegment(sketch, "E196.top", {"start": v(57.55, -83.98) * mm, "end": v(45.75, -83.98) * mm});
            skLineSegment(sketch, "E196.left", {"start": v(57.55, -103.78) * mm, "end": v(57.55, -83.98) * mm});
            skLineSegment(sketch, "E196.right", {"start": v(45.75, -103.78) * mm, "end": v(45.75, -83.98) * mm});
            skPoint(sketch, "E196.middle", {"position": v(51.65, -93.88) * mm});
            skSolve(sketch);
        }
        {
            var Q0;
            Q0=makeQuery(id+"F54.imprint","IMPRINT",FACE,{"disambiguationData":[TD([[makeQuery(id+"F54.imprint","IMPRINT",EDGE,{"derivedFrom":sQuery(id+"F54.wireOp",EDGE,"E196.bottom")}),-1.0]])]});
            var Q1;
            Q1=makeQuery(id+"F54.imprint","IMPRINT",FACE,{"disambiguationData":[TD([[makeQuery(id+"F54.imprint","IMPRINT",EDGE,{"derivedFrom":sQuery(id+"F54.wireOp",EDGE,"E195.bottom")}),-1.0]])]});
            extrude(context, id + "F55", {"entities" : qUnion([Q0, Q1]), "depth" : 1 * mm});
        }
        {
            var Q0;
            Q0=makeQuery(id+"F23.opExtrude","SWEPT_EDGE",EDGE,{"disambiguationData":[OSD([sQuery(id+"F1.wireOp",EDGE,"E87.top"),sQuery(id+"F1.wireOp",EDGE,"E87.right")])]});
            var Q1;
            Q1=makeQuery(id+"F49.opExtrude","SWEPT_EDGE",EDGE,{"disambiguationData":[OSD([sQuery(id+"F48.wireOp",EDGE,"E192.2"),sQuery(id+"F48.wireOp",EDGE,"E192.3")])]});
            var Q2;
            Q2=makeQuery(id+"F49.opExtrude","SWEPT_EDGE",EDGE,{"disambiguationData":[OSD([sQuery(id+"F48.wireOp",EDGE,"E192.0"),sQuery(id+"F48.wireOp",EDGE,"E192.3")])]});
            var Q3;
            Q3=makeQuery(id+"F23.opExtrude","SWEPT_EDGE",EDGE,{"disambiguationData":[OSD([sQuery(id+"F1.wireOp",EDGE,"E87.top"),sQuery(id+"F1.wireOp",EDGE,"E87.left")])]});
            var Q4;
            Q4=makeQuery(id+"F49.opExtrude","SWEPT_EDGE",EDGE,{"disambiguationData":[OSD([sQuery(id+"F48.wireOp",EDGE,"E192.0"),sQuery(id+"F48.wireOp",EDGE,"E192.1")])]});
            var Q5;
            Q5=makeQuery(id+"F23.opExtrude","SWEPT_EDGE",EDGE,{"disambiguationData":[OSD([sQuery(id+"F1.wireOp",EDGE,"E87.bottom"),sQuery(id+"F1.wireOp",EDGE,"E87.left")])]});
            var Q6;
            Q6=makeQuery(id+"F49.opExtrude","SWEPT_EDGE",EDGE,{"disambiguationData":[OSD([sQuery(id+"F48.wireOp",EDGE,"E192.1"),sQuery(id+"F48.wireOp",EDGE,"E192.2")])]});
            var Q7;
            Q7=makeQuery(id+"F23.opExtrude","SWEPT_EDGE",EDGE,{"disambiguationData":[OSD([sQuery(id+"F1.wireOp",EDGE,"E87.bottom"),sQuery(id+"F1.wireOp",EDGE,"E87.right")])]});
            var Q8;
            Q8=makeQuery(id+"F55.opExtrude","SWEPT_EDGE",EDGE,{"disambiguationData":[OSD([sQuery(id+"F54.wireOp",EDGE,"E196.bottom"),sQuery(id+"F54.wireOp",EDGE,"E196.right")])]});
            var Q9;
            Q9=makeQuery(id+"F55.opExtrude","SWEPT_EDGE",EDGE,{"disambiguationData":[OSD([sQuery(id+"F54.wireOp",EDGE,"E196.bottom"),sQuery(id+"F54.wireOp",EDGE,"E196.left")])]});
            var Q10;
            Q10=makeQuery(id+"F55.opExtrude","SWEPT_EDGE",EDGE,{"disambiguationData":[OSD([sQuery(id+"F54.wireOp",EDGE,"E196.top"),sQuery(id+"F54.wireOp",EDGE,"E196.right")])]});
            var Q11;
            Q11=makeQuery(id+"F55.opExtrude","SWEPT_EDGE",EDGE,{"disambiguationData":[OSD([sQuery(id+"F54.wireOp",EDGE,"E196.top"),sQuery(id+"F54.wireOp",EDGE,"E196.left")])]});
            fillet(context, id + "F56", {"entities" : qUnion([Q0, Q1, Q2, Q3, Q4, Q5, Q6, Q7, Q8, Q9, Q10, Q11]), "radius" : 1 * mm, "tangentPropagation" : true, "allowEdgeOverflow" : false});
        }
        {
            var Q0;
            Q0=makeQuery(id+"F23.opExtrude","CAP_FACE",FACE,{"disambiguationData":[OSD([sQuery(id+"F1.wireOp",EDGE,"E73.bottom"),sQuery(id+"F1.wireOp",EDGE,"E73.top"),sQuery(id+"F1.wireOp",EDGE,"E73.left"),sQuery(id+"F1.wireOp",EDGE,"E73.right"),sQuery(id+"F1.wireOp",EDGE,"E74.bottom"),sQuery(id+"F1.wireOp",EDGE,"E74.top"),sQuery(id+"F1.wireOp",EDGE,"E74.left"),sQuery(id+"F1.wireOp",EDGE,"E74.right"),sQuery(id+"F1.wireOp",EDGE,"E75.bottom"),sQuery(id+"F1.wireOp",EDGE,"E75.top"),sQuery(id+"F1.wireOp",EDGE,"E75.left"),sQuery(id+"F1.wireOp",EDGE,"E75.right"),sQuery(id+"F1.wireOp",EDGE,"E80"),sQuery(id+"F1.wireOp",EDGE,"E81"),sQuery(id+"F1.wireOp",EDGE,"E83"),sQuery(id+"F1.wireOp",EDGE,"E84"),sQuery(id+"F1.wireOp",EDGE,"E87.bottom"),sQuery(id+"F1.wireOp",EDGE,"E87.top"),sQuery(id+"F1.wireOp",EDGE,"E87.left"),sQuery(id+"F1.wireOp",EDGE,"E87.right"),sQuery(id+"F1.wireOp",EDGE,"E89"),sQuery(id+"F1.wireOp",EDGE,"E92"),sQuery(id+"F1.wireOp",EDGE,"E93"),sQuery(id+"F1.wireOp",EDGE,"CoPGjB9w-zRhk-UiIu-dCG4-BhNkDkZw4NkV"),sQuery(id+"F1.wireOp",EDGE,"XJoTFQyA-9xYx-y9zl-Xs7Z-xe6QLGOleBae"),sQuery(id+"F1.wireOp",EDGE,"E94"),sQuery(id+"F1.wireOp",EDGE,"E95"),sQuery(id+"F1.wireOp",EDGE,"E96"),sQuery(id+"F1.wireOp",EDGE,"E97"),sQuery(id+"F1.wireOp",EDGE,"E98"),sQuery(id+"F1.wireOp",EDGE,"E99"),sQuery(id+"F1.wireOp",EDGE,"E100"),sQuery(id+"F1.wireOp",EDGE,"E101"),sQuery(id+"F1.wireOp",EDGE,"E102"),sQuery(id+"F1.wireOp",EDGE,"E105.1.0.0"),sQuery(id+"F1.wireOp",EDGE,"E105.1.0.1"),sQuery(id+"F1.wireOp",EDGE,"E105.1.0.2"),sQuery(id+"F1.wireOp",EDGE,"E105.1.0.3"),sQuery(id+"F1.wireOp",EDGE,"E105.2.0.0"),sQuery(id+"F1.wireOp",EDGE,"E105.2.0.1"),sQuery(id+"F1.wireOp",EDGE,"E105.2.0.2"),sQuery(id+"F1.wireOp",EDGE,"E105.2.0.3"),sQuery(id+"F1.wireOp",EDGE,"E106.1.0.0"),sQuery(id+"F1.wireOp",EDGE,"E106.1.0.1"),sQuery(id+"F1.wireOp",EDGE,"E106.1.0.2"),sQuery(id+"F1.wireOp",EDGE,"E106.1.0.3"),sQuery(id+"F1.wireOp",EDGE,"E106.2.0.0"),sQuery(id+"F1.wireOp",EDGE,"E106.2.0.1"),sQuery(id+"F1.wireOp",EDGE,"E106.2.0.2"),sQuery(id+"F1.wireOp",EDGE,"E106.2.0.3")])],"isStart":false});
            var sketch = newSketch(context, id + "F57", { "sketchPlane" : qUnion([Q0])});
            skCircle(sketch, "E197", {"center": v(-56.34, -124.73) * mm, "radius": 5 * mm});
            skCircle(sketch, "E198", {"center": v(-56.34, -174.73) * mm, "radius": 5 * mm});
            skCircle(sketch, "E199", {"center": v(83.66, -124.73) * mm, "radius": 5 * mm});
            skCircle(sketch, "E200", {"center": v(83.66, -174.73) * mm, "radius": 5 * mm});
            skLineSegment(sketch, "E201.bottom", {"start": v(-66.34, -129.73) * mm, "end": v(-56.34, -129.73) * mm});
            skLineSegment(sketch, "E201.top", {"start": v(-66.34, -119.73) * mm, "end": v(-56.34, -119.73) * mm});
            skLineSegment(sketch, "E201.left", {"start": v(-66.34, -129.73) * mm, "end": v(-66.34, -119.73) * mm});
            skLineSegment(sketch, "E202.bottom", {"start": v(-56.34, -179.73) * mm, "end": v(-66.34, -179.73) * mm});
            skLineSegment(sketch, "E202.top", {"start": v(-56.34, -169.73) * mm, "end": v(-66.34, -169.73) * mm});
            skLineSegment(sketch, "E202.right", {"start": v(-66.34, -179.73) * mm, "end": v(-66.34, -169.73) * mm});
            skLineSegment(sketch, "E203.bottom", {"start": v(98.24, -129.73) * mm, "end": v(83.66, -129.73) * mm});
            skLineSegment(sketch, "E203.top", {"start": v(98.24, -119.73) * mm, "end": v(83.66, -119.73) * mm});
            skLineSegment(sketch, "E203.left", {"start": v(98.24, -129.73) * mm, "end": v(98.24, -119.73) * mm});
            skLineSegment(sketch, "E204.bottom", {"start": v(93.66, -179.73) * mm, "end": v(83.66, -179.73) * mm});
            skLineSegment(sketch, "E204.top", {"start": v(93.66, -169.73) * mm, "end": v(83.66, -169.73) * mm});
            skLineSegment(sketch, "E204.left", {"start": v(93.66, -179.73) * mm, "end": v(93.66, -169.73) * mm});
            skSolve(sketch);
        }
        {
            var Q0;
            Q0=qSketchRegion(id+"F57",true);
            extrude(context, id + "F58", {"entities" : qUnion([Q0]), "operationType" : NewBodyOperationType.REMOVE, "oppositeDirection" : true, "depth" : 1 * mm});
        }
        {
            var Q0;
            Q0=makeQuery(id+"F10.opExtrude","CAP_EDGE",EDGE,{"disambiguationData":[OSD([sQuery(id+"F9.wireOp",EDGE,"E141.0")])],"isStart":false});
            var Q1;
            Q1=makeQuery(id+"F10.opExtrude","CAP_EDGE",EDGE,{"disambiguationData":[OSD([sQuery(id+"F9.wireOp",EDGE,"E141.3")])],"isStart":false});
            var Q2;
            Q2=makeQuery(id+"F10.opExtrude","CAP_EDGE",EDGE,{"disambiguationData":[OSD([sQuery(id+"F9.wireOp",EDGE,"E141.2")])],"isStart":false});
            var Q3;
            Q3=makeQuery(id+"F10.opExtrude","CAP_EDGE",EDGE,{"disambiguationData":[OSD([sQuery(id+"F9.wireOp",EDGE,"E141.1")])],"isStart":false});
            var Q4;
            {var subQ0=sQuery(id+"F1.wireOp",EDGE,"E73.right");var subQ1=sQuery(id+"F1.wireOp",EDGE,"E73.top");Q4=makeQuery(id+"F58.boolean.opBoolean","SPLIT",EDGE,{"disambiguationData":[TD([makeQuery(id+"F23.opExtrude","SWEPT_FACE",FACE,{"disambiguationData":[OSD([subQ1])]})])],"derivedFrom":makeQuery(id+"F23.opExtrude","CAP_EDGE",EDGE,{"disambiguationData":[OSD([subQ0])],"isStart":false})});}
            var Q5;
            Q5=makeQuery(id+"F23.opExtrude","CAP_EDGE",EDGE,{"disambiguationData":[OSD([sQuery(id+"F1.wireOp",EDGE,"E73.top")])],"isStart":false});
            var Q6;
            Q6=makeQuery(id+"F58.boolean.opBoolean","COPY",EDGE,{"derivedFrom":makeQuery(id+"F58.opExtrude","CAP_EDGE",EDGE,{"disambiguationData":[OSD([sQuery(id+"F57.wireOp",EDGE,"E201.top")])],"isStart":true})});
            var Q7;
            {var subQ0=sQuery(id+"F1.wireOp",EDGE,"E73.right");Q7=makeQuery(id+"F58.boolean.opBoolean","SPLIT",EDGE,{"disambiguationData":[TD([makeQuery(id+"F58.opExtrude","SWEPT_FACE",FACE,{"disambiguationData":[OSD([sQuery(id+"F57.wireOp",EDGE,"E201.bottom")])]})])],"derivedFrom":makeQuery(id+"F23.opExtrude","CAP_EDGE",EDGE,{"disambiguationData":[OSD([subQ0])],"isStart":false})});}
            var Q8;
            Q8=makeQuery(id+"F58.boolean.opBoolean","COPY",EDGE,{"derivedFrom":makeQuery(id+"F58.opExtrude","CAP_EDGE",EDGE,{"disambiguationData":[OSD([sQuery(id+"F57.wireOp",EDGE,"E202.top")])],"isStart":true})});
            var Q9;
            {var subQ0=sQuery(id+"F1.wireOp",EDGE,"E73.bottom");var subQ1=sQuery(id+"F1.wireOp",EDGE,"E73.right");Q9=makeQuery(id+"F58.boolean.opBoolean","SPLIT",EDGE,{"disambiguationData":[TD([makeQuery(id+"F23.opExtrude","SWEPT_FACE",FACE,{"disambiguationData":[OSD([subQ0])]})])],"derivedFrom":makeQuery(id+"F23.opExtrude","CAP_EDGE",EDGE,{"disambiguationData":[OSD([subQ1])],"isStart":false})});}
            var Q10;
            Q10=makeQuery(id+"F23.opExtrude","CAP_EDGE",EDGE,{"disambiguationData":[OSD([sQuery(id+"F1.wireOp",EDGE,"E73.bottom")])],"isStart":false});
            var Q11;
            {var subQ0=sQuery(id+"F1.wireOp",EDGE,"E73.bottom");var subQ1=sQuery(id+"F1.wireOp",EDGE,"E73.left");Q11=makeQuery(id+"F58.boolean.opBoolean","SPLIT",EDGE,{"disambiguationData":[TD([makeQuery(id+"F23.opExtrude","SWEPT_FACE",FACE,{"disambiguationData":[OSD([subQ0])]})])],"derivedFrom":makeQuery(id+"F23.opExtrude","CAP_EDGE",EDGE,{"disambiguationData":[OSD([subQ1])],"isStart":false})});}
            var Q12;
            Q12=makeQuery(id+"F58.boolean.opBoolean","COPY",EDGE,{"derivedFrom":makeQuery(id+"F58.opExtrude","CAP_EDGE",EDGE,{"disambiguationData":[OSD([sQuery(id+"F57.wireOp",EDGE,"E204.bottom")])],"isStart":true})});
            var Q13;
            {var subQ0=sQuery(id+"F1.wireOp",EDGE,"E73.left");Q13=makeQuery(id+"F58.boolean.opBoolean","SPLIT",EDGE,{"disambiguationData":[TD([makeQuery(id+"F58.opExtrude","SWEPT_FACE",FACE,{"disambiguationData":[OSD([sQuery(id+"F57.wireOp",EDGE,"E203.bottom")])]})])],"derivedFrom":makeQuery(id+"F23.opExtrude","CAP_EDGE",EDGE,{"disambiguationData":[OSD([subQ0])],"isStart":false})});}
            var Q14;
            Q14=makeQuery(id+"F58.boolean.opBoolean","COPY",EDGE,{"derivedFrom":makeQuery(id+"F58.opExtrude","CAP_EDGE",EDGE,{"disambiguationData":[OSD([sQuery(id+"F57.wireOp",EDGE,"E203.bottom")])],"isStart":true})});
            var Q15;
            {var subQ0=sQuery(id+"F1.wireOp",EDGE,"E73.left");var subQ1=sQuery(id+"F1.wireOp",EDGE,"E73.top");Q15=makeQuery(id+"F58.boolean.opBoolean","SPLIT",EDGE,{"disambiguationData":[TD([makeQuery(id+"F23.opExtrude","SWEPT_FACE",FACE,{"disambiguationData":[OSD([subQ1])]})])],"derivedFrom":makeQuery(id+"F23.opExtrude","CAP_EDGE",EDGE,{"disambiguationData":[OSD([subQ0])],"isStart":false})});}
            fillet(context, id + "F59", {"entities" : qUnion([Q0, Q1, Q2, Q3, Q4, Q5, Q6, Q7, Q8, Q9, Q10, Q11, Q12, Q13, Q14, Q15]), "radius" : 0.5 * mm, "tangentPropagation" : true, "allowEdgeOverflow" : false});
        }
    });
